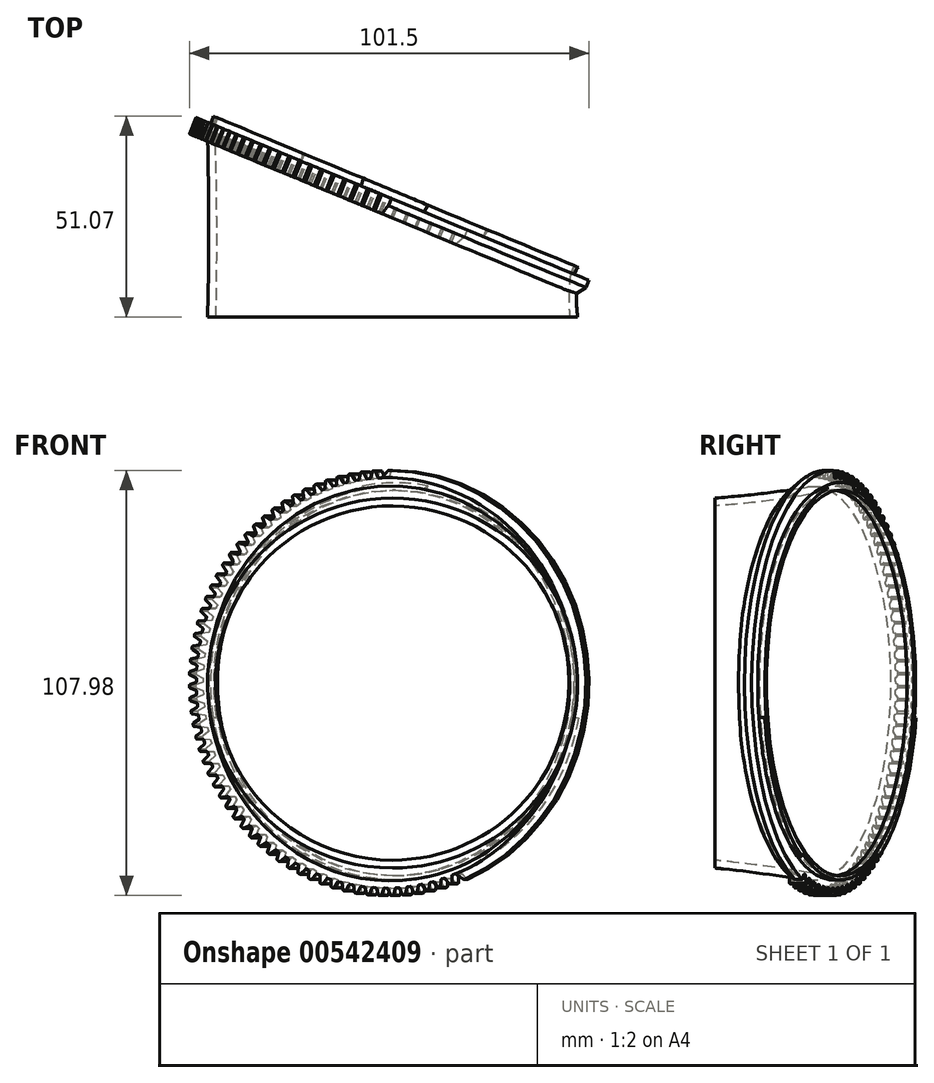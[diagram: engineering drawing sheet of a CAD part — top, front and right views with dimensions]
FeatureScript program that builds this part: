
annotation { "Feature Type Name" : "Feature", "Feature Type Description" : "" }
export const myFeature = defineFeature(function(context is Context, id is Id, definition is map)
    precondition{}
    {
        {
            var Q0;
            Q0=qCreatedBy(makeId("Front.planeOp"),FACE);
            var sketch = newSketch(context, id + "F0", { "sketchPlane" : qUnion([Q0])});
            skCircle(sketch, "E0", {"center": v(0, 0) * mm, "radius": 47 * mm});
            skSolve(sketch);
        }
        {
            var Q0;
            Q0=qCreatedBy(makeId("Top.planeOp"),FACE);
            var sketch = newSketch(context, id + "F1", { "sketchPlane" : qUnion([Q0])});
            skLineSegment(sketch, "E1", {"start": v(23.1, 20.43) * mm, "end": v(-23.1, 39.57) * mm});
            skLineSegment(sketch, "E2", {"start": v(25, 0) * mm, "end": v(-25, 0) * mm});
            skLineSegment(sketch, "E3", {"start": v(0, 30) * mm, "end": v(0, 0) * mm});
            skPoint(sketch, "E4", {"position": v(0, 30) * mm});
            skSolve(sketch);
        }
        {
            var Q0;
            Q0=sQuery(id+"F1.wireOp",EDGE,"E1");
            cPlane(context, id + "F2", {"entities" : qUnion([Q0]), "cplaneType" : CPlaneType.LINE_ANGLE, "offset" : 25 * mm, "angle" : 0 * degree, "width" : 150 * mm, "height" : 150 * mm});
        }
        {
            var Q0;
            Q0=qCreatedBy(id+"F2.planeOp",FACE);
            var sketch = newSketch(context, id + "F3", { "sketchPlane" : qUnion([Q0])});
            skCircle(sketch, "E5", {"center": v(-11.48, 0) * mm, "radius": 51 * mm});
            skSolve(sketch);
        }
        {
            var Q0;
            Q0=makeQuery(id+"F0.imprint","IMPRINT",FACE,{"disambiguationData":[TD([[makeQuery(id+"F0.imprint","IMPRINT",EDGE,{"derivedFrom":sQuery(id+"F0.wireOp",EDGE,"E0")}),1.0]])]});
            var Q1;
            Q1=makeQuery(id+"F3.imprint","IMPRINT",FACE,{"disambiguationData":[TD([[makeQuery(id+"F3.imprint","IMPRINT",EDGE,{"derivedFrom":sQuery(id+"F3.wireOp",EDGE,"E5")}),1.0]])]});
            loft(context, id + "F4", {"sheetProfilesArray" : [{ "sheetProfileEntities" : qUnion([Q0]) }, { "sheetProfileEntities" : qUnion([Q1]) }]});
        }
        {
            var Q0;
            Q0=makeQuery(id+"F4.opLoft","CAP_FACE",FACE,{"disambiguationData":[OSD([makeQuery(id+"F3.imprint","IMPRINT",FACE,{"disambiguationData":[TD([[makeQuery(id+"F3.imprint","IMPRINT",EDGE,{"derivedFrom":sQuery(id+"F3.wireOp",EDGE,"E5")}),1.0]])]})])],"isStart":true});
            var sketch = newSketch(context, id + "F5", { "sketchPlane" : qUnion([Q0])});
            skCircle(sketch, "E6", {"center": v(11.48, 0) * mm, "radius": 49 * mm});
            skSolve(sketch);
        }
        {
            var Q0;
            Q0=makeQuery(id+"F4.opLoft","CAP_FACE",FACE,{"disambiguationData":[OSD([makeQuery(id+"F0.imprint","IMPRINT",FACE,{"disambiguationData":[TD([[makeQuery(id+"F0.imprint","IMPRINT",EDGE,{"derivedFrom":sQuery(id+"F0.wireOp",EDGE,"E0")}),1.0]])]})])],"isStart":true});
            var sketch = newSketch(context, id + "F6", { "sketchPlane" : qUnion([Q0])});
            skCircle(sketch, "E7", {"center": v(0, 0) * mm, "radius": 45 * mm});
            skSolve(sketch);
        }
        {
            var Q0;
            Q0=makeQuery(id+"F4.opLoft","CAP_FACE",FACE,{"disambiguationData":[OSD([makeQuery(id+"F3.imprint","IMPRINT",FACE,{"disambiguationData":[TD([[makeQuery(id+"F3.imprint","IMPRINT",EDGE,{"derivedFrom":sQuery(id+"F3.wireOp",EDGE,"E5")}),1.0]])]})])],"isStart":true});
            var sketch = newSketch(context, id + "F7", { "sketchPlane" : qUnion([Q0])});
            skCircle(sketch, "E8", {"center": v(11.48, 0) * mm, "radius": 54 * mm});
            skCircle(sketch, "E9", {"center": v(11.48, 0) * mm, "radius": 50.9 * mm});
            skSolve(sketch);
        }
        {
            var Q0;
            Q0=makeQuery(id+"F7.imprint","IMPRINT",FACE,{"disambiguationData":[TD([[makeQuery(id+"F7.imprint","IMPRINT",EDGE,{"derivedFrom":sQuery(id+"F7.wireOp",EDGE,"E8")}),1.0]])]});
            var Q1;
            Q1=makeQuery(id+"F7.imprint","IMPRINT",FACE,{"disambiguationData":[TD([[makeQuery(id+"F7.imprint","IMPRINT",EDGE,{"derivedFrom":sQuery(id+"F7.wireOp",EDGE,"E9")}),-1.0]])]});
            var Q2;
            Q2=makeQuery(id+"F7.imprint","IMPRINT",FACE,{"disambiguationData":[TD([[makeQuery(id+"F7.imprint","IMPRINT",EDGE,{"derivedFrom":sQuery(id+"F7.wireOp",EDGE,"E9")}),1.0]])]});
            extrude(context, id + "F8", {"entities" : qUnion([Q0, Q1, Q2]), "operationType" : NewBodyOperationType.ADD, "oppositeDirection" : true, "depth" : 4.5 * mm, "offsetDistance" : 25 * mm});
        }
        {
            var Q0;
            Q0=makeQuery(id+"F8.boolean.opBoolean","MERGE",FACE,{"derivedFrom":[makeQuery(id+"F4.opLoft","CAP_FACE",FACE,{"disambiguationData":[OSD([makeQuery(id+"F3.imprint","IMPRINT",FACE,{"disambiguationData":[TD([[makeQuery(id+"F3.imprint","IMPRINT",EDGE,{"derivedFrom":sQuery(id+"F3.wireOp",EDGE,"E5")}),1.0]])]})])],"isStart":true}),makeQuery(id+"F8.opExtrude","CAP_FACE",FACE,{"disambiguationData":[OSD([sQuery(id+"F7.wireOp",EDGE,"E8"),sQuery(id+"F7.wireOp",EDGE,"E9")])],"isStart":true})]});
            var sketch = newSketch(context, id + "F9", { "sketchPlane" : qUnion([Q0])});
            skCircle(sketch, "E10", {"center": v(11.48, 0) * mm, "radius": 51 * mm});
            skCircle(sketch, "E11", {"center": v(11.48, 0) * mm, "radius": 49 * mm});
            skSolve(sketch);
        }
        {
            var Q1;
            Q1=makeQuery(id+"F6.imprint","IMPRINT",FACE,{"disambiguationData":[TD([[makeQuery(id+"F6.imprint","IMPRINT",EDGE,{"derivedFrom":sQuery(id+"F6.wireOp",EDGE,"E7")}),1.0]])]});
            var Q2;
            Q2=makeQuery(id+"F5.imprint","IMPRINT",FACE,{"disambiguationData":[TD([[makeQuery(id+"F5.imprint","IMPRINT",EDGE,{"derivedFrom":sQuery(id+"F5.wireOp",EDGE,"E6")}),1.0]])]});
            loft(context, id + "F10", {"operationType" : NewBodyOperationType.REMOVE, "sheetProfilesArray" : [{ "sheetProfileEntities" : qUnion([Q1]) }, { "sheetProfileEntities" : qUnion([Q2]) }]});
        }
        {
            var Q0;
            Q0=makeQuery(id+"F9.imprint","IMPRINT",FACE,{"disambiguationData":[TD([[makeQuery(id+"F9.imprint","IMPRINT",EDGE,{"derivedFrom":sQuery(id+"F9.wireOp",EDGE,"E10")}),1.0]])]});
            extrude(context, id + "F11", {"entities" : qUnion([Q0]), "operationType" : NewBodyOperationType.ADD, "depth" : 2 * mm, "offsetDistance" : 25 * mm});
        }
        {
            var Q0;
            Q0=makeQuery(id+"F11.opExtrude","CAP_EDGE",EDGE,{"disambiguationData":[OSD([sQuery(id+"F9.wireOp",EDGE,"E10")])],"isStart":false});
            chamfer(context, id + "F12", {"entities" : qUnion([Q0]), "chamferType" : ChamferType.OFFSET_ANGLE, "width" : 2 * mm, "oppositeDirection" : true, "angle" : 5 * degree, "tangentPropagation" : true});
        }
        {
            var Q0;
            Q0=makeQuery(id+"F8.boolean.opBoolean","MERGE",FACE,{"derivedFrom":[makeQuery(id+"F4.opLoft","CAP_FACE",FACE,{"disambiguationData":[OSD([makeQuery(id+"F3.imprint","IMPRINT",FACE,{"disambiguationData":[TD([[makeQuery(id+"F3.imprint","IMPRINT",EDGE,{"derivedFrom":sQuery(id+"F3.wireOp",EDGE,"E5")}),1.0]])]})])],"isStart":true}),makeQuery(id+"F8.opExtrude","CAP_FACE",FACE,{"disambiguationData":[OSD([sQuery(id+"F7.wireOp",EDGE,"E8"),sQuery(id+"F7.wireOp",EDGE,"E9")])],"isStart":true})]});
            var sketch = newSketch(context, id + "F13", { "sketchPlane" : qUnion([Q0])});
            skLineSegment(sketch, "E12", {"start": v(11.48, 0) * mm, "end": v(11.48, 54) * mm});
            skLineSegment(sketch, "E13", {"start": v(11.48, 0) * mm, "end": v(14.8, 53.9) * mm});
            skLineSegment(sketch, "E14", {"start": v(11.48, 54) * mm, "end": v(11.74, 54) * mm});
            skLineSegment(sketch, "E15", {"start": v(14.8, 53.9) * mm, "end": v(14.54, 53.91) * mm});
            skLineSegment(sketch, "E16", {"start": v(12.7, 52.09) * mm, "end": v(13.47, 52.07) * mm});
            skLineSegment(sketch, "E17", {"start": v(11.93, 53.87) * mm, "end": v(12.5, 52.22) * mm});
            skLineSegment(sketch, "E18", {"start": v(13.66, 52.2) * mm, "end": v(14.34, 53.8) * mm});
            skPoint(sketch, "E19.visualSharp", {"position": v(11.88, 54) * mm});
            skArc(sketch, "E19.filletArc", {"start": v(11.93, 53.87) * mm, "mid": v(11.85, 53.96) * mm, "end": v(11.74, 54) * mm});
            skPoint(sketch, "E20.visualSharp", {"position": v(12.56, 52.09) * mm});
            skArc(sketch, "E20.filletArc", {"start": v(12.5, 52.22) * mm, "mid": v(12.58, 52.12) * mm, "end": v(12.7, 52.09) * mm});
            skPoint(sketch, "E21.visualSharp", {"position": v(13.6, 52.07) * mm});
            skArc(sketch, "E21.filletArc", {"start": v(13.47, 52.07) * mm, "mid": v(13.58, 52.1) * mm, "end": v(13.66, 52.2) * mm});
            skPoint(sketch, "E22.visualSharp", {"position": v(14.4, 53.92) * mm});
            skArc(sketch, "E22.filletArc", {"start": v(14.54, 53.91) * mm, "mid": v(14.42, 53.88) * mm, "end": v(14.34, 53.8) * mm});
            skLineSegment(sketch, "E23", {"start": v(11.74, 54) * mm, "end": v(14.54, 53.91) * mm});
            skLineSegment(sketch, "E24.1.0", {"start": v(11.5, 54) * mm, "end": v(11.25, 54) * mm});
            skPoint(sketch, "E24.1.1", {"position": v(9.38, 52.06) * mm});
            skLineSegment(sketch, "E24.1.2", {"start": v(8.64, 53.8) * mm, "end": v(9.32, 52.19) * mm});
            skPoint(sketch, "E24.1.3", {"position": v(10.43, 52.1) * mm});
            skPoint(sketch, "E24.1.4", {"position": v(8.59, 53.92) * mm});
            skLineSegment(sketch, "E24.1.5", {"start": v(8.19, 53.9) * mm, "end": v(8.45, 53.92) * mm});
            skLineSegment(sketch, "E24.1.6", {"start": v(9.52, 52.06) * mm, "end": v(10.3, 52.1) * mm});
            skPoint(sketch, "E24.1.7", {"position": v(11.1, 54) * mm});
            skLineSegment(sketch, "E24.1.8", {"start": v(8.45, 53.92) * mm, "end": v(11.25, 54) * mm});
            skLineSegment(sketch, "E24.1.9", {"start": v(10.47, 52.23) * mm, "end": v(11.06, 53.87) * mm});
            skArc(sketch, "E24.1.10", {"start": v(9.32, 52.19) * mm, "mid": v(9.4, 52.1) * mm, "end": v(9.52, 52.06) * mm});
            skArc(sketch, "E24.1.11", {"start": v(10.3, 52.1) * mm, "mid": v(10.4, 52.13) * mm, "end": v(10.47, 52.23) * mm});
            skArc(sketch, "E24.1.12", {"start": v(11.25, 54) * mm, "mid": v(11.13, 53.96) * mm, "end": v(11.06, 53.87) * mm});
            skArc(sketch, "E24.1.13", {"start": v(8.64, 53.8) * mm, "mid": v(8.56, 53.89) * mm, "end": v(8.45, 53.92) * mm});
            skLineSegment(sketch, "E24.2.0", {"start": v(8.21, 53.9) * mm, "end": v(7.95, 53.89) * mm});
            skPoint(sketch, "E24.2.1", {"position": v(6.2, 51.83) * mm});
            skLineSegment(sketch, "E24.2.2", {"start": v(5.37, 53.52) * mm, "end": v(6.15, 51.96) * mm});
            skPoint(sketch, "E24.2.3", {"position": v(7.25, 51.94) * mm});
            skPoint(sketch, "E24.2.4", {"position": v(5.3, 53.65) * mm});
            skLineSegment(sketch, "E24.2.5", {"start": v(4.9, 53.6) * mm, "end": v(5.17, 53.63) * mm});
            skLineSegment(sketch, "E24.2.6", {"start": v(6.35, 51.85) * mm, "end": v(7.12, 51.93) * mm});
            skPoint(sketch, "E24.2.7", {"position": v(7.81, 53.88) * mm});
            skLineSegment(sketch, "E24.2.8", {"start": v(5.17, 53.63) * mm, "end": v(7.95, 53.89) * mm});
            skLineSegment(sketch, "E24.2.9", {"start": v(7.3, 52.07) * mm, "end": v(7.77, 53.74) * mm});
            skArc(sketch, "E24.2.10", {"start": v(6.15, 51.96) * mm, "mid": v(6.23, 51.87) * mm, "end": v(6.35, 51.85) * mm});
            skArc(sketch, "E24.2.11", {"start": v(7.12, 51.93) * mm, "mid": v(7.23, 51.97) * mm, "end": v(7.3, 52.07) * mm});
            skArc(sketch, "E24.2.12", {"start": v(7.95, 53.89) * mm, "mid": v(7.84, 53.84) * mm, "end": v(7.77, 53.74) * mm});
            skArc(sketch, "E24.2.13", {"start": v(5.37, 53.52) * mm, "mid": v(5.28, 53.6) * mm, "end": v(5.17, 53.63) * mm});
            skLineSegment(sketch, "E24.3.0", {"start": v(4.93, 53.6) * mm, "end": v(4.68, 53.57) * mm});
            skPoint(sketch, "E24.3.1", {"position": v(3.06, 51.41) * mm});
            skLineSegment(sketch, "E24.3.2", {"start": v(2.12, 53.05) * mm, "end": v(2.99, 51.53) * mm});
            skPoint(sketch, "E24.3.3", {"position": v(4.1, 51.58) * mm});
            skPoint(sketch, "E24.3.4", {"position": v(2.05, 53.17) * mm});
            skLineSegment(sketch, "E24.3.5", {"start": v(1.65, 53.1) * mm, "end": v(1.9, 53.15) * mm});
            skLineSegment(sketch, "E24.3.6", {"start": v(3.2, 51.44) * mm, "end": v(3.96, 51.56) * mm});
            skPoint(sketch, "E24.3.7", {"position": v(4.53, 53.55) * mm});
            skLineSegment(sketch, "E24.3.8", {"start": v(1.9, 53.15) * mm, "end": v(4.68, 53.57) * mm});
            skLineSegment(sketch, "E24.3.9", {"start": v(4.12, 51.72) * mm, "end": v(4.5, 53.42) * mm});
            skArc(sketch, "E24.3.10", {"start": v(2.99, 51.53) * mm, "mid": v(3.08, 51.45) * mm, "end": v(3.2, 51.44) * mm});
            skArc(sketch, "E24.3.11", {"start": v(3.96, 51.56) * mm, "mid": v(4.07, 51.61) * mm, "end": v(4.12, 51.72) * mm});
            skArc(sketch, "E24.3.12", {"start": v(4.68, 53.57) * mm, "mid": v(4.56, 53.52) * mm, "end": v(4.5, 53.42) * mm});
            skArc(sketch, "E24.3.13", {"start": v(2.12, 53.05) * mm, "mid": v(2.03, 53.13) * mm, "end": v(1.9, 53.15) * mm});
            skLineSegment(sketch, "E24.4.0", {"start": v(1.68, 53.1) * mm, "end": v(1.42, 53.06) * mm});
            skPoint(sketch, "E24.4.1", {"position": v(-0.06, 50.8) * mm});
            skLineSegment(sketch, "E24.4.2", {"start": v(-1.1, 52.38) * mm, "end": v(-0.14, 50.92) * mm});
            skPoint(sketch, "E24.4.3", {"position": v(0.96, 51.04) * mm});
            skPoint(sketch, "E24.4.4", {"position": v(-1.18, 52.5) * mm});
            skLineSegment(sketch, "E24.4.5", {"start": v(-1.57, 52.4) * mm, "end": v(-1.31, 52.46) * mm});
            skLineSegment(sketch, "E24.4.6", {"start": v(0.07, 50.84) * mm, "end": v(0.83, 51) * mm});
            skPoint(sketch, "E24.4.7", {"position": v(1.28, 53.03) * mm});
            skLineSegment(sketch, "E24.4.8", {"start": v(-1.31, 52.46) * mm, "end": v(1.42, 53.06) * mm});
            skLineSegment(sketch, "E24.4.9", {"start": v(0.99, 51.17) * mm, "end": v(1.26, 52.9) * mm});
            skArc(sketch, "E24.4.10", {"start": v(-0.14, 50.92) * mm, "mid": v(-0.04, 50.85) * mm, "end": v(0.07, 50.84) * mm});
            skArc(sketch, "E24.4.11", {"start": v(0.83, 51) * mm, "mid": v(0.93, 51.07) * mm, "end": v(0.99, 51.17) * mm});
            skArc(sketch, "E24.4.12", {"start": v(1.42, 53.06) * mm, "mid": v(1.32, 53) * mm, "end": v(1.26, 52.9) * mm});
            skArc(sketch, "E24.4.13", {"start": v(-1.1, 52.38) * mm, "mid": v(-1.2, 52.46) * mm, "end": v(-1.31, 52.46) * mm});
            skLineSegment(sketch, "E24.5.0", {"start": v(-1.54, 52.4) * mm, "end": v(-1.8, 52.34) * mm});
            skPoint(sketch, "E24.5.1", {"position": v(-3.14, 50) * mm});
            skLineSegment(sketch, "E24.5.2", {"start": v(-4.27, 51.51) * mm, "end": v(-3.22, 50.12) * mm});
            skPoint(sketch, "E24.5.3", {"position": v(-2.13, 50.3) * mm});
            skPoint(sketch, "E24.5.4", {"position": v(-4.35, 51.63) * mm});
            skLineSegment(sketch, "E24.5.5", {"start": v(-4.74, 51.5) * mm, "end": v(-4.49, 51.59) * mm});
            skLineSegment(sketch, "E24.5.6", {"start": v(-3, 50.05) * mm, "end": v(-2.26, 50.26) * mm});
            skPoint(sketch, "E24.5.7", {"position": v(-1.93, 52.3) * mm});
            skLineSegment(sketch, "E24.5.8", {"start": v(-4.49, 51.59) * mm, "end": v(-1.8, 52.34) * mm});
            skLineSegment(sketch, "E24.5.9", {"start": v(-2.11, 50.44) * mm, "end": v(-1.94, 52.17) * mm});
            skArc(sketch, "E24.5.10", {"start": v(-3.22, 50.12) * mm, "mid": v(-3.12, 50.05) * mm, "end": v(-3, 50.05) * mm});
            skArc(sketch, "E24.5.11", {"start": v(-2.26, 50.26) * mm, "mid": v(-2.16, 50.33) * mm, "end": v(-2.11, 50.44) * mm});
            skArc(sketch, "E24.5.12", {"start": v(-1.8, 52.34) * mm, "mid": v(-1.9, 52.28) * mm, "end": v(-1.94, 52.17) * mm});
            skArc(sketch, "E24.5.13", {"start": v(-4.27, 51.51) * mm, "mid": v(-4.37, 51.58) * mm, "end": v(-4.49, 51.59) * mm});
            skLineSegment(sketch, "E24.6.0", {"start": v(-4.71, 51.51) * mm, "end": v(-4.96, 51.44) * mm});
            skPoint(sketch, "E24.6.1", {"position": v(-6.16, 49.02) * mm});
            skLineSegment(sketch, "E24.6.2", {"start": v(-7.38, 50.46) * mm, "end": v(-6.25, 49.13) * mm});
            skPoint(sketch, "E24.6.3", {"position": v(-5.17, 49.38) * mm});
            skPoint(sketch, "E24.6.4", {"position": v(-7.47, 50.57) * mm});
            skLineSegment(sketch, "E24.6.5", {"start": v(-7.85, 50.42) * mm, "end": v(-7.6, 50.52) * mm});
            skLineSegment(sketch, "E24.6.6", {"start": v(-6.03, 49.07) * mm, "end": v(-5.3, 49.33) * mm});
            skPoint(sketch, "E24.6.7", {"position": v(-5.1, 51.4) * mm});
            skLineSegment(sketch, "E24.6.8", {"start": v(-7.6, 50.52) * mm, "end": v(-4.96, 51.44) * mm});
            skLineSegment(sketch, "E24.6.9", {"start": v(-5.16, 49.51) * mm, "end": v(-5.1, 51.25) * mm});
            skArc(sketch, "E24.6.10", {"start": v(-6.25, 49.13) * mm, "mid": v(-6.15, 49.07) * mm, "end": v(-6.03, 49.07) * mm});
            skArc(sketch, "E24.6.11", {"start": v(-5.3, 49.33) * mm, "mid": v(-5.2, 49.4) * mm, "end": v(-5.16, 49.51) * mm});
            skArc(sketch, "E24.6.12", {"start": v(-4.96, 51.44) * mm, "mid": v(-5.06, 51.37) * mm, "end": v(-5.1, 51.25) * mm});
            skArc(sketch, "E24.6.13", {"start": v(-7.38, 50.46) * mm, "mid": v(-7.48, 50.52) * mm, "end": v(-7.6, 50.52) * mm});
            skLineSegment(sketch, "E24.7.0", {"start": v(-7.82, 50.43) * mm, "end": v(-8.07, 50.34) * mm});
            skPoint(sketch, "E24.7.1", {"position": v(-9.11, 47.86) * mm});
            skLineSegment(sketch, "E24.7.2", {"start": v(-10.42, 49.21) * mm, "end": v(-9.2, 47.96) * mm});
            skPoint(sketch, "E24.7.3", {"position": v(-8.15, 48.27) * mm});
            skPoint(sketch, "E24.7.4", {"position": v(-10.52, 49.32) * mm});
            skLineSegment(sketch, "E24.7.5", {"start": v(-10.88, 49.15) * mm, "end": v(-10.65, 49.26) * mm});
            skLineSegment(sketch, "E24.7.6", {"start": v(-8.99, 47.91) * mm, "end": v(-8.27, 48.22) * mm});
            skPoint(sketch, "E24.7.7", {"position": v(-8.2, 50.29) * mm});
            skLineSegment(sketch, "E24.7.8", {"start": v(-10.65, 49.26) * mm, "end": v(-8.07, 50.34) * mm});
            skLineSegment(sketch, "E24.7.9", {"start": v(-8.15, 48.4) * mm, "end": v(-8.2, 50.15) * mm});
            skArc(sketch, "E24.7.10", {"start": v(-9.2, 47.96) * mm, "mid": v(-9.1, 47.9) * mm, "end": v(-8.99, 47.91) * mm});
            skArc(sketch, "E24.7.11", {"start": v(-8.27, 48.22) * mm, "mid": v(-8.18, 48.3) * mm, "end": v(-8.15, 48.4) * mm});
            skArc(sketch, "E24.7.12", {"start": v(-8.07, 50.34) * mm, "mid": v(-8.16, 50.26) * mm, "end": v(-8.2, 50.15) * mm});
            skArc(sketch, "E24.7.13", {"start": v(-10.42, 49.21) * mm, "mid": v(-10.53, 49.27) * mm, "end": v(-10.65, 49.26) * mm});
            skLineSegment(sketch, "E24.8.0", {"start": v(-10.86, 49.16) * mm, "end": v(-11.1, 49.05) * mm});
            skPoint(sketch, "E24.8.1", {"position": v(-12, 46.51) * mm});
            skLineSegment(sketch, "E24.8.2", {"start": v(-13.38, 47.79) * mm, "end": v(-12.1, 46.6) * mm});
            skPoint(sketch, "E24.8.3", {"position": v(-11.05, 46.99) * mm});
            skPoint(sketch, "E24.8.4", {"position": v(-13.49, 47.88) * mm});
            skLineSegment(sketch, "E24.8.5", {"start": v(-13.84, 47.7) * mm, "end": v(-13.61, 47.82) * mm});
            skLineSegment(sketch, "E24.8.6", {"start": v(-11.87, 46.57) * mm, "end": v(-11.18, 46.93) * mm});
            skPoint(sketch, "E24.8.7", {"position": v(-11.23, 49) * mm});
            skLineSegment(sketch, "E24.8.8", {"start": v(-13.61, 47.82) * mm, "end": v(-11.1, 49.05) * mm});
            skLineSegment(sketch, "E24.8.9", {"start": v(-11.07, 47.12) * mm, "end": v(-11.21, 48.85) * mm});
            skArc(sketch, "E24.8.10", {"start": v(-12.1, 46.6) * mm, "mid": v(-11.99, 46.56) * mm, "end": v(-11.87, 46.57) * mm});
            skArc(sketch, "E24.8.11", {"start": v(-11.18, 46.93) * mm, "mid": v(-11.1, 47) * mm, "end": v(-11.07, 47.12) * mm});
            skArc(sketch, "E24.8.12", {"start": v(-11.1, 49.05) * mm, "mid": v(-11.19, 48.97) * mm, "end": v(-11.21, 48.85) * mm});
            skArc(sketch, "E24.8.13", {"start": v(-13.38, 47.79) * mm, "mid": v(-13.5, 47.84) * mm, "end": v(-13.61, 47.82) * mm});
            skLineSegment(sketch, "E24.9.0", {"start": v(-13.82, 47.7) * mm, "end": v(-14.05, 47.59) * mm});
            skPoint(sketch, "E24.9.1", {"position": v(-14.79, 45) * mm});
            skLineSegment(sketch, "E24.9.2", {"start": v(-16.25, 46.18) * mm, "end": v(-14.9, 45.08) * mm});
            skPoint(sketch, "E24.9.3", {"position": v(-13.88, 45.52) * mm});
            skPoint(sketch, "E24.9.4", {"position": v(-16.36, 46.27) * mm});
            skLineSegment(sketch, "E24.9.5", {"start": v(-16.7, 46.06) * mm, "end": v(-16.48, 46.2) * mm});
            skLineSegment(sketch, "E24.9.6", {"start": v(-14.67, 45.06) * mm, "end": v(-14, 45.46) * mm});
            skPoint(sketch, "E24.9.7", {"position": v(-14.17, 47.52) * mm});
            skLineSegment(sketch, "E24.9.8", {"start": v(-16.48, 46.2) * mm, "end": v(-14.05, 47.59) * mm});
            skLineSegment(sketch, "E24.9.9", {"start": v(-13.9, 45.66) * mm, "end": v(-14.15, 47.38) * mm});
            skArc(sketch, "E24.9.10", {"start": v(-14.9, 45.08) * mm, "mid": v(-14.78, 45.04) * mm, "end": v(-14.67, 45.06) * mm});
            skArc(sketch, "E24.9.11", {"start": v(-14, 45.46) * mm, "mid": v(-13.91, 45.54) * mm, "end": v(-13.9, 45.66) * mm});
            skArc(sketch, "E24.9.12", {"start": v(-14.05, 47.59) * mm, "mid": v(-14.13, 47.5) * mm, "end": v(-14.15, 47.38) * mm});
            skArc(sketch, "E24.9.13", {"start": v(-16.25, 46.18) * mm, "mid": v(-16.36, 46.23) * mm, "end": v(-16.48, 46.2) * mm});
            skLineSegment(sketch, "E24.10.0", {"start": v(-16.68, 46.08) * mm, "end": v(-16.9, 45.94) * mm});
            skPoint(sketch, "E24.10.1", {"position": v(-17.48, 43.3) * mm});
            skLineSegment(sketch, "E24.10.2", {"start": v(-19.01, 44.4) * mm, "end": v(-17.6, 43.4) * mm});
            skPoint(sketch, "E24.10.3", {"position": v(-16.6, 43.9) * mm});
            skPoint(sketch, "E24.10.4", {"position": v(-19.13, 44.49) * mm});
            skLineSegment(sketch, "E24.10.5", {"start": v(-19.46, 44.26) * mm, "end": v(-19.24, 44.4) * mm});
            skLineSegment(sketch, "E24.10.6", {"start": v(-17.36, 43.39) * mm, "end": v(-16.72, 43.82) * mm});
            skPoint(sketch, "E24.10.7", {"position": v(-17.02, 45.87) * mm});
            skLineSegment(sketch, "E24.10.8", {"start": v(-19.24, 44.4) * mm, "end": v(-16.9, 45.94) * mm});
            skLineSegment(sketch, "E24.10.9", {"start": v(-16.63, 44.03) * mm, "end": v(-17, 45.73) * mm});
            skArc(sketch, "E24.10.10", {"start": v(-17.6, 43.4) * mm, "mid": v(-17.48, 43.35) * mm, "end": v(-17.36, 43.39) * mm});
            skArc(sketch, "E24.10.11", {"start": v(-16.72, 43.82) * mm, "mid": v(-16.64, 43.9) * mm, "end": v(-16.63, 44.03) * mm});
            skArc(sketch, "E24.10.12", {"start": v(-16.9, 45.94) * mm, "mid": v(-16.98, 45.85) * mm, "end": v(-17, 45.73) * mm});
            skArc(sketch, "E24.10.13", {"start": v(-19.01, 44.4) * mm, "mid": v(-19.13, 44.44) * mm, "end": v(-19.24, 44.4) * mm});
            skLineSegment(sketch, "E24.11.0", {"start": v(-19.44, 44.27) * mm, "end": v(-19.65, 44.13) * mm});
            skPoint(sketch, "E24.11.1", {"position": v(-20.07, 41.46) * mm});
            skLineSegment(sketch, "E24.11.2", {"start": v(-21.66, 42.47) * mm, "end": v(-20.18, 41.54) * mm});
            skPoint(sketch, "E24.11.3", {"position": v(-19.23, 42.1) * mm});
            skPoint(sketch, "E24.11.4", {"position": v(-21.78, 42.54) * mm});
            skLineSegment(sketch, "E24.11.5", {"start": v(-22.1, 42.3) * mm, "end": v(-21.9, 42.45) * mm});
            skLineSegment(sketch, "E24.11.6", {"start": v(-19.96, 41.55) * mm, "end": v(-19.34, 42.02) * mm});
            skPoint(sketch, "E24.11.7", {"position": v(-19.76, 44.04) * mm});
            skLineSegment(sketch, "E24.11.8", {"start": v(-21.9, 42.45) * mm, "end": v(-19.65, 44.13) * mm});
            skLineSegment(sketch, "E24.11.9", {"start": v(-19.27, 42.23) * mm, "end": v(-19.73, 43.9) * mm});
            skArc(sketch, "E24.11.10", {"start": v(-20.18, 41.54) * mm, "mid": v(-20.07, 41.5) * mm, "end": v(-19.96, 41.55) * mm});
            skArc(sketch, "E24.11.11", {"start": v(-19.34, 42.02) * mm, "mid": v(-19.27, 42.11) * mm, "end": v(-19.27, 42.23) * mm});
            skArc(sketch, "E24.11.12", {"start": v(-19.65, 44.13) * mm, "mid": v(-19.72, 44.03) * mm, "end": v(-19.73, 43.9) * mm});
            skArc(sketch, "E24.11.13", {"start": v(-21.66, 42.47) * mm, "mid": v(-21.78, 42.5) * mm, "end": v(-21.9, 42.45) * mm});
            skLineSegment(sketch, "E24.12.0", {"start": v(-22.08, 42.3) * mm, "end": v(-22.28, 42.15) * mm});
            skPoint(sketch, "E24.12.1", {"position": v(-22.53, 39.46) * mm});
            skLineSegment(sketch, "E24.12.2", {"start": v(-24.19, 40.37) * mm, "end": v(-22.66, 39.53) * mm});
            skPoint(sketch, "E24.12.3", {"position": v(-21.74, 40.15) * mm});
            skPoint(sketch, "E24.12.4", {"position": v(-24.31, 40.43) * mm});
            skLineSegment(sketch, "E24.12.5", {"start": v(-24.61, 40.17) * mm, "end": v(-24.42, 40.34) * mm});
            skLineSegment(sketch, "E24.12.6", {"start": v(-22.43, 39.55) * mm, "end": v(-21.84, 40.06) * mm});
            skPoint(sketch, "E24.12.7", {"position": v(-22.4, 42.06) * mm});
            skLineSegment(sketch, "E24.12.8", {"start": v(-24.42, 40.34) * mm, "end": v(-22.28, 42.15) * mm});
            skLineSegment(sketch, "E24.12.9", {"start": v(-21.78, 40.28) * mm, "end": v(-22.35, 41.92) * mm});
            skArc(sketch, "E24.12.10", {"start": v(-22.66, 39.53) * mm, "mid": v(-22.54, 39.5) * mm, "end": v(-22.43, 39.55) * mm});
            skArc(sketch, "E24.12.11", {"start": v(-21.84, 40.06) * mm, "mid": v(-21.78, 40.16) * mm, "end": v(-21.78, 40.28) * mm});
            skArc(sketch, "E24.12.12", {"start": v(-22.28, 42.15) * mm, "mid": v(-22.35, 42.05) * mm, "end": v(-22.35, 41.92) * mm});
            skArc(sketch, "E24.12.13", {"start": v(-24.19, 40.37) * mm, "mid": v(-24.3, 40.39) * mm, "end": v(-24.42, 40.34) * mm});
            skLineSegment(sketch, "E24.13.0", {"start": v(-24.6, 40.18) * mm, "end": v(-24.79, 40) * mm});
            skPoint(sketch, "E24.13.1", {"position": v(-24.88, 37.32) * mm});
            skLineSegment(sketch, "E24.13.2", {"start": v(-26.58, 38.12) * mm, "end": v(-25, 37.38) * mm});
            skPoint(sketch, "E24.13.3", {"position": v(-24.12, 38.05) * mm});
            skPoint(sketch, "E24.13.4", {"position": v(-26.71, 38.18) * mm});
            skLineSegment(sketch, "E24.13.5", {"start": v(-27, 37.9) * mm, "end": v(-26.81, 38.08) * mm});
            skLineSegment(sketch, "E24.13.6", {"start": v(-24.78, 37.41) * mm, "end": v(-24.22, 37.96) * mm});
            skPoint(sketch, "E24.13.7", {"position": v(-24.9, 39.91) * mm});
            skLineSegment(sketch, "E24.13.8", {"start": v(-26.81, 38.08) * mm, "end": v(-24.79, 40) * mm});
            skLineSegment(sketch, "E24.13.9", {"start": v(-24.18, 38.17) * mm, "end": v(-24.84, 39.78) * mm});
            skArc(sketch, "E24.13.10", {"start": v(-25, 37.38) * mm, "mid": v(-24.88, 37.36) * mm, "end": v(-24.78, 37.41) * mm});
            skArc(sketch, "E24.13.11", {"start": v(-24.22, 37.96) * mm, "mid": v(-24.17, 38.06) * mm, "end": v(-24.18, 38.17) * mm});
            skArc(sketch, "E24.13.12", {"start": v(-24.79, 40) * mm, "mid": v(-24.85, 39.9) * mm, "end": v(-24.84, 39.78) * mm});
            skArc(sketch, "E24.13.13", {"start": v(-26.58, 38.12) * mm, "mid": v(-26.7, 38.13) * mm, "end": v(-26.81, 38.08) * mm});
            skLineSegment(sketch, "E24.14.0", {"start": v(-26.98, 37.9) * mm, "end": v(-27.16, 37.72) * mm});
            skPoint(sketch, "E24.14.1", {"position": v(-27.08, 35.03) * mm});
            skLineSegment(sketch, "E24.14.2", {"start": v(-28.84, 35.72) * mm, "end": v(-27.21, 35.08) * mm});
            skPoint(sketch, "E24.14.3", {"position": v(-26.38, 35.8) * mm});
            skPoint(sketch, "E24.14.4", {"position": v(-28.97, 35.78) * mm});
            skLineSegment(sketch, "E24.14.5", {"start": v(-29.23, 35.48) * mm, "end": v(-29.06, 35.67) * mm});
            skLineSegment(sketch, "E24.14.6", {"start": v(-27, 35.13) * mm, "end": v(-26.47, 35.7) * mm});
            skPoint(sketch, "E24.14.7", {"position": v(-27.26, 37.62) * mm});
            skLineSegment(sketch, "E24.14.8", {"start": v(-29.06, 35.67) * mm, "end": v(-27.16, 37.72) * mm});
            skLineSegment(sketch, "E24.14.9", {"start": v(-26.44, 35.93) * mm, "end": v(-27.2, 37.5) * mm});
            skArc(sketch, "E24.14.10", {"start": v(-27.21, 35.08) * mm, "mid": v(-27.1, 35.07) * mm, "end": v(-27, 35.13) * mm});
            skArc(sketch, "E24.14.11", {"start": v(-26.47, 35.7) * mm, "mid": v(-26.42, 35.81) * mm, "end": v(-26.44, 35.93) * mm});
            skArc(sketch, "E24.14.12", {"start": v(-27.16, 37.72) * mm, "mid": v(-27.21, 37.62) * mm, "end": v(-27.2, 37.5) * mm});
            skArc(sketch, "E24.14.13", {"start": v(-28.84, 35.72) * mm, "mid": v(-28.96, 35.73) * mm, "end": v(-29.06, 35.67) * mm});
            skLineSegment(sketch, "E24.15.0", {"start": v(-29.22, 35.5) * mm, "end": v(-29.39, 35.3) * mm});
            skPoint(sketch, "E24.15.1", {"position": v(-29.15, 32.61) * mm});
            skLineSegment(sketch, "E24.15.2", {"start": v(-30.94, 33.2) * mm, "end": v(-29.28, 32.66) * mm});
            skPoint(sketch, "E24.15.3", {"position": v(-28.5, 33.43) * mm});
            skPoint(sketch, "E24.15.4", {"position": v(-31.07, 33.24) * mm});
            skLineSegment(sketch, "E24.15.5", {"start": v(-31.32, 32.93) * mm, "end": v(-31.16, 33.13) * mm});
            skLineSegment(sketch, "E24.15.6", {"start": v(-29.06, 32.72) * mm, "end": v(-28.58, 33.33) * mm});
            skPoint(sketch, "E24.15.7", {"position": v(-29.48, 35.2) * mm});
            skLineSegment(sketch, "E24.15.8", {"start": v(-31.16, 33.13) * mm, "end": v(-29.39, 35.3) * mm});
            skLineSegment(sketch, "E24.15.9", {"start": v(-28.56, 33.55) * mm, "end": v(-29.41, 35.07) * mm});
            skArc(sketch, "E24.15.10", {"start": v(-29.28, 32.66) * mm, "mid": v(-29.16, 32.66) * mm, "end": v(-29.06, 32.72) * mm});
            skArc(sketch, "E24.15.11", {"start": v(-28.58, 33.33) * mm, "mid": v(-28.53, 33.44) * mm, "end": v(-28.56, 33.55) * mm});
            skArc(sketch, "E24.15.12", {"start": v(-29.39, 35.3) * mm, "mid": v(-29.43, 35.19) * mm, "end": v(-29.41, 35.07) * mm});
            skArc(sketch, "E24.15.13", {"start": v(-30.94, 33.2) * mm, "mid": v(-31.06, 33.2) * mm, "end": v(-31.16, 33.13) * mm});
            skLineSegment(sketch, "E24.16.0", {"start": v(-31.3, 32.95) * mm, "end": v(-31.46, 32.74) * mm});
            skPoint(sketch, "E24.16.1", {"position": v(-31.06, 30.08) * mm});
            skLineSegment(sketch, "E24.16.2", {"start": v(-32.89, 30.55) * mm, "end": v(-31.2, 30.11) * mm});
            skPoint(sketch, "E24.16.3", {"position": v(-30.45, 30.93) * mm});
            skPoint(sketch, "E24.16.4", {"position": v(-33.02, 30.59) * mm});
            skLineSegment(sketch, "E24.16.5", {"start": v(-33.25, 30.26) * mm, "end": v(-33.1, 30.47) * mm});
            skLineSegment(sketch, "E24.16.6", {"start": v(-30.98, 30.19) * mm, "end": v(-30.53, 30.82) * mm});
            skPoint(sketch, "E24.16.7", {"position": v(-31.55, 32.63) * mm});
            skLineSegment(sketch, "E24.16.8", {"start": v(-33.1, 30.47) * mm, "end": v(-31.46, 32.74) * mm});
            skLineSegment(sketch, "E24.16.9", {"start": v(-30.53, 31.05) * mm, "end": v(-31.47, 32.51) * mm});
            skArc(sketch, "E24.16.10", {"start": v(-31.2, 30.11) * mm, "mid": v(-31.08, 30.12) * mm, "end": v(-30.98, 30.19) * mm});
            skArc(sketch, "E24.16.11", {"start": v(-30.53, 30.82) * mm, "mid": v(-30.5, 30.94) * mm, "end": v(-30.53, 31.05) * mm});
            skArc(sketch, "E24.16.12", {"start": v(-31.46, 32.74) * mm, "mid": v(-31.5, 32.63) * mm, "end": v(-31.47, 32.51) * mm});
            skArc(sketch, "E24.16.13", {"start": v(-32.89, 30.55) * mm, "mid": v(-33, 30.55) * mm, "end": v(-33.1, 30.47) * mm});
            skLineSegment(sketch, "E24.17.0", {"start": v(-33.23, 30.28) * mm, "end": v(-33.38, 30.06) * mm});
            skPoint(sketch, "E24.17.1", {"position": v(-32.82, 27.43) * mm});
            skLineSegment(sketch, "E24.17.2", {"start": v(-34.67, 27.8) * mm, "end": v(-32.95, 27.45) * mm});
            skPoint(sketch, "E24.17.3", {"position": v(-32.26, 28.32) * mm});
            skPoint(sketch, "E24.17.4", {"position": v(-34.8, 27.82) * mm});
            skLineSegment(sketch, "E24.17.5", {"start": v(-35, 27.47) * mm, "end": v(-34.88, 27.7) * mm});
            skLineSegment(sketch, "E24.17.6", {"start": v(-32.74, 27.54) * mm, "end": v(-32.33, 28.2) * mm});
            skPoint(sketch, "E24.17.7", {"position": v(-33.46, 29.95) * mm});
            skLineSegment(sketch, "E24.17.8", {"start": v(-34.88, 27.7) * mm, "end": v(-33.38, 30.06) * mm});
            skLineSegment(sketch, "E24.17.9", {"start": v(-32.34, 28.43) * mm, "end": v(-33.37, 29.83) * mm});
            skArc(sketch, "E24.17.10", {"start": v(-32.95, 27.45) * mm, "mid": v(-32.83, 27.47) * mm, "end": v(-32.74, 27.54) * mm});
            skArc(sketch, "E24.17.11", {"start": v(-32.33, 28.2) * mm, "mid": v(-32.3, 28.32) * mm, "end": v(-32.34, 28.43) * mm});
            skArc(sketch, "E24.17.12", {"start": v(-33.38, 30.06) * mm, "mid": v(-33.41, 29.95) * mm, "end": v(-33.37, 29.83) * mm});
            skArc(sketch, "E24.17.13", {"start": v(-34.67, 27.8) * mm, "mid": v(-34.79, 27.78) * mm, "end": v(-34.88, 27.7) * mm});
            skLineSegment(sketch, "E24.18.0", {"start": v(-35, 27.5) * mm, "end": v(-35.13, 27.27) * mm});
            skPoint(sketch, "E24.18.1", {"position": v(-34.4, 24.68) * mm});
            skLineSegment(sketch, "E24.18.2", {"start": v(-36.27, 24.93) * mm, "end": v(-34.54, 24.7) * mm});
            skPoint(sketch, "E24.18.3", {"position": v(-33.9, 25.6) * mm});
            skPoint(sketch, "E24.18.4", {"position": v(-36.41, 24.94) * mm});
            skLineSegment(sketch, "E24.18.5", {"start": v(-36.6, 24.59) * mm, "end": v(-36.48, 24.82) * mm});
            skLineSegment(sketch, "E24.18.6", {"start": v(-34.34, 24.8) * mm, "end": v(-33.97, 25.48) * mm});
            skPoint(sketch, "E24.18.7", {"position": v(-35.2, 27.15) * mm});
            skLineSegment(sketch, "E24.18.8", {"start": v(-36.48, 24.82) * mm, "end": v(-35.13, 27.27) * mm});
            skLineSegment(sketch, "E24.18.9", {"start": v(-34, 25.7) * mm, "end": v(-35.1, 27.04) * mm});
            skArc(sketch, "E24.18.10", {"start": v(-34.54, 24.7) * mm, "mid": v(-34.43, 24.71) * mm, "end": v(-34.34, 24.8) * mm});
            skArc(sketch, "E24.18.11", {"start": v(-33.97, 25.48) * mm, "mid": v(-33.95, 25.6) * mm, "end": v(-34, 25.7) * mm});
            skArc(sketch, "E24.18.12", {"start": v(-35.13, 27.27) * mm, "mid": v(-35.16, 27.15) * mm, "end": v(-35.1, 27.04) * mm});
            skArc(sketch, "E24.18.13", {"start": v(-36.27, 24.93) * mm, "mid": v(-36.4, 24.9) * mm, "end": v(-36.48, 24.82) * mm});
            skLineSegment(sketch, "E24.19.0", {"start": v(-36.59, 24.6) * mm, "end": v(-36.7, 24.38) * mm});
            skPoint(sketch, "E24.19.1", {"position": v(-35.82, 21.83) * mm});
            skLineSegment(sketch, "E24.19.2", {"start": v(-37.7, 21.97) * mm, "end": v(-35.96, 21.84) * mm});
            skPoint(sketch, "E24.19.3", {"position": v(-35.38, 22.79) * mm});
            skPoint(sketch, "E24.19.4", {"position": v(-37.85, 21.98) * mm});
            skLineSegment(sketch, "E24.19.5", {"start": v(-38, 21.61) * mm, "end": v(-37.9, 21.85) * mm});
            skLineSegment(sketch, "E24.19.6", {"start": v(-35.77, 21.96) * mm, "end": v(-35.44, 22.66) * mm});
            skPoint(sketch, "E24.19.7", {"position": v(-36.77, 24.25) * mm});
            skLineSegment(sketch, "E24.19.8", {"start": v(-37.9, 21.85) * mm, "end": v(-36.7, 24.38) * mm});
            skLineSegment(sketch, "E24.19.9", {"start": v(-35.48, 22.89) * mm, "end": v(-36.67, 24.15) * mm});
            skArc(sketch, "E24.19.10", {"start": v(-35.96, 21.84) * mm, "mid": v(-35.85, 21.87) * mm, "end": v(-35.77, 21.96) * mm});
            skArc(sketch, "E24.19.11", {"start": v(-35.44, 22.66) * mm, "mid": v(-35.42, 22.78) * mm, "end": v(-35.48, 22.89) * mm});
            skArc(sketch, "E24.19.12", {"start": v(-36.7, 24.38) * mm, "mid": v(-36.72, 24.26) * mm, "end": v(-36.67, 24.15) * mm});
            skArc(sketch, "E24.19.13", {"start": v(-37.7, 21.97) * mm, "mid": v(-37.82, 21.94) * mm, "end": v(-37.9, 21.85) * mm});
            skLineSegment(sketch, "E24.20.0", {"start": v(-38, 21.63) * mm, "end": v(-38.1, 21.4) * mm});
            skPoint(sketch, "E24.20.1", {"position": v(-37.07, 18.9) * mm});
            skLineSegment(sketch, "E24.20.2", {"start": v(-38.95, 18.93) * mm, "end": v(-37.2, 18.9) * mm});
            skPoint(sketch, "E24.20.3", {"position": v(-36.69, 19.89) * mm});
            skPoint(sketch, "E24.20.4", {"position": v(-39.1, 18.93) * mm});
            skLineSegment(sketch, "E24.20.5", {"start": v(-39.23, 18.56) * mm, "end": v(-39.14, 18.8) * mm});
            skLineSegment(sketch, "E24.20.6", {"start": v(-37.02, 19.04) * mm, "end": v(-36.74, 19.76) * mm});
            skPoint(sketch, "E24.20.7", {"position": v(-38.16, 21.27) * mm});
            skLineSegment(sketch, "E24.20.8", {"start": v(-39.14, 18.8) * mm, "end": v(-38.1, 21.4) * mm});
            skLineSegment(sketch, "E24.20.9", {"start": v(-36.78, 19.98) * mm, "end": v(-38.05, 21.17) * mm});
            skArc(sketch, "E24.20.10", {"start": v(-37.2, 18.9) * mm, "mid": v(-37.1, 18.94) * mm, "end": v(-37.02, 19.04) * mm});
            skArc(sketch, "E24.20.11", {"start": v(-36.74, 19.76) * mm, "mid": v(-36.73, 19.88) * mm, "end": v(-36.78, 19.98) * mm});
            skArc(sketch, "E24.20.12", {"start": v(-38.1, 21.4) * mm, "mid": v(-38.11, 21.28) * mm, "end": v(-38.05, 21.17) * mm});
            skArc(sketch, "E24.20.13", {"start": v(-38.95, 18.93) * mm, "mid": v(-39.07, 18.9) * mm, "end": v(-39.14, 18.8) * mm});
            skLineSegment(sketch, "E24.21.0", {"start": v(-39.22, 18.58) * mm, "end": v(-39.31, 18.33) * mm});
            skPoint(sketch, "E24.21.1", {"position": v(-38.13, 15.91) * mm});
            skLineSegment(sketch, "E24.21.2", {"start": v(-40.01, 15.82) * mm, "end": v(-38.27, 15.9) * mm});
            skPoint(sketch, "E24.21.3", {"position": v(-37.8, 16.91) * mm});
            skPoint(sketch, "E24.21.4", {"position": v(-40.15, 15.81) * mm});
            skLineSegment(sketch, "E24.21.5", {"start": v(-40.27, 15.43) * mm, "end": v(-40.2, 15.68) * mm});
            skLineSegment(sketch, "E24.21.6", {"start": v(-38.09, 16.04) * mm, "end": v(-37.85, 16.79) * mm});
            skPoint(sketch, "E24.21.7", {"position": v(-39.36, 18.2) * mm});
            skLineSegment(sketch, "E24.21.8", {"start": v(-40.2, 15.68) * mm, "end": v(-39.31, 18.33) * mm});
            skLineSegment(sketch, "E24.21.9", {"start": v(-37.91, 17) * mm, "end": v(-39.25, 18.11) * mm});
            skArc(sketch, "E24.21.10", {"start": v(-38.27, 15.9) * mm, "mid": v(-38.16, 15.95) * mm, "end": v(-38.09, 16.04) * mm});
            skArc(sketch, "E24.21.11", {"start": v(-37.85, 16.79) * mm, "mid": v(-37.85, 16.9) * mm, "end": v(-37.91, 17) * mm});
            skArc(sketch, "E24.21.12", {"start": v(-39.31, 18.33) * mm, "mid": v(-39.32, 18.21) * mm, "end": v(-39.25, 18.11) * mm});
            skArc(sketch, "E24.21.13", {"start": v(-40.01, 15.82) * mm, "mid": v(-40.13, 15.78) * mm, "end": v(-40.2, 15.68) * mm});
            skLineSegment(sketch, "E24.22.0", {"start": v(-40.26, 15.45) * mm, "end": v(-40.34, 15.2) * mm});
            skPoint(sketch, "E24.22.1", {"position": v(-39, 12.86) * mm});
            skLineSegment(sketch, "E24.22.2", {"start": v(-40.88, 12.65) * mm, "end": v(-39.15, 12.84) * mm});
            skPoint(sketch, "E24.22.3", {"position": v(-38.75, 13.88) * mm});
            skPoint(sketch, "E24.22.4", {"position": v(-41.02, 12.63) * mm});
            skLineSegment(sketch, "E24.22.5", {"start": v(-41.11, 12.25) * mm, "end": v(-41.05, 12.5) * mm});
            skLineSegment(sketch, "E24.22.6", {"start": v(-38.97, 13) * mm, "end": v(-38.78, 13.75) * mm});
            skPoint(sketch, "E24.22.7", {"position": v(-40.38, 15.07) * mm});
            skLineSegment(sketch, "E24.22.8", {"start": v(-41.05, 12.5) * mm, "end": v(-40.34, 15.2) * mm});
            skLineSegment(sketch, "E24.22.9", {"start": v(-38.86, 13.96) * mm, "end": v(-40.26, 14.98) * mm});
            skArc(sketch, "E24.22.10", {"start": v(-39.15, 12.84) * mm, "mid": v(-39.04, 12.9) * mm, "end": v(-38.97, 13) * mm});
            skArc(sketch, "E24.22.11", {"start": v(-38.78, 13.75) * mm, "mid": v(-38.79, 13.86) * mm, "end": v(-38.86, 13.96) * mm});
            skArc(sketch, "E24.22.12", {"start": v(-40.34, 15.2) * mm, "mid": v(-40.33, 15.08) * mm, "end": v(-40.26, 14.98) * mm});
            skArc(sketch, "E24.22.13", {"start": v(-40.88, 12.65) * mm, "mid": v(-41, 12.6) * mm, "end": v(-41.05, 12.5) * mm});
            skLineSegment(sketch, "E24.23.0", {"start": v(-41.1, 12.27) * mm, "end": v(-41.17, 12.02) * mm});
            skPoint(sketch, "E24.23.1", {"position": v(-39.7, 9.76) * mm});
            skLineSegment(sketch, "E24.23.2", {"start": v(-41.56, 9.43) * mm, "end": v(-39.83, 9.73) * mm});
            skPoint(sketch, "E24.23.3", {"position": v(-39.5, 10.79) * mm});
            skPoint(sketch, "E24.23.4", {"position": v(-41.7, 9.41) * mm});
            skLineSegment(sketch, "E24.23.5", {"start": v(-41.76, 9.02) * mm, "end": v(-41.72, 9.27) * mm});
            skLineSegment(sketch, "E24.23.6", {"start": v(-39.67, 9.9) * mm, "end": v(-39.53, 10.66) * mm});
            skPoint(sketch, "E24.23.7", {"position": v(-41.2, 11.88) * mm});
            skLineSegment(sketch, "E24.23.8", {"start": v(-41.72, 9.27) * mm, "end": v(-41.17, 12.02) * mm});
            skLineSegment(sketch, "E24.23.9", {"start": v(-39.61, 10.86) * mm, "end": v(-41.08, 11.8) * mm});
            skArc(sketch, "E24.23.10", {"start": v(-39.83, 9.73) * mm, "mid": v(-39.73, 9.79) * mm, "end": v(-39.67, 9.9) * mm});
            skArc(sketch, "E24.23.11", {"start": v(-39.53, 10.66) * mm, "mid": v(-39.54, 10.77) * mm, "end": v(-39.61, 10.86) * mm});
            skArc(sketch, "E24.23.12", {"start": v(-41.17, 12.02) * mm, "mid": v(-41.16, 11.9) * mm, "end": v(-41.08, 11.8) * mm});
            skArc(sketch, "E24.23.13", {"start": v(-41.56, 9.43) * mm, "mid": v(-41.66, 9.38) * mm, "end": v(-41.72, 9.27) * mm});
            skLineSegment(sketch, "E24.24.0", {"start": v(-41.76, 9.04) * mm, "end": v(-41.8, 8.78) * mm});
            skPoint(sketch, "E24.24.1", {"position": v(-40.2, 6.62) * mm});
            skLineSegment(sketch, "E24.24.2", {"start": v(-42.03, 6.18) * mm, "end": v(-40.33, 6.59) * mm});
            skPoint(sketch, "E24.24.3", {"position": v(-40.06, 7.66) * mm});
            skPoint(sketch, "E24.24.4", {"position": v(-42.17, 6.15) * mm});
            skLineSegment(sketch, "E24.24.5", {"start": v(-42.21, 5.75) * mm, "end": v(-42.18, 6.01) * mm});
            skLineSegment(sketch, "E24.24.6", {"start": v(-40.18, 6.76) * mm, "end": v(-40.08, 7.53) * mm});
            skPoint(sketch, "E24.24.7", {"position": v(-41.82, 8.65) * mm});
            skLineSegment(sketch, "E24.24.8", {"start": v(-42.18, 6.01) * mm, "end": v(-41.8, 8.78) * mm});
            skLineSegment(sketch, "E24.24.9", {"start": v(-40.18, 7.73) * mm, "end": v(-41.7, 8.58) * mm});
            skArc(sketch, "E24.24.10", {"start": v(-40.33, 6.59) * mm, "mid": v(-40.23, 6.65) * mm, "end": v(-40.18, 6.76) * mm});
            skArc(sketch, "E24.24.11", {"start": v(-40.08, 7.53) * mm, "mid": v(-40.1, 7.64) * mm, "end": v(-40.18, 7.73) * mm});
            skArc(sketch, "E24.24.12", {"start": v(-41.8, 8.78) * mm, "mid": v(-41.78, 8.66) * mm, "end": v(-41.7, 8.58) * mm});
            skArc(sketch, "E24.24.13", {"start": v(-42.03, 6.18) * mm, "mid": v(-42.14, 6.12) * mm, "end": v(-42.18, 6.01) * mm});
            skLineSegment(sketch, "E24.25.0", {"start": v(-42.2, 5.78) * mm, "end": v(-42.24, 5.52) * mm});
            skPoint(sketch, "E24.25.1", {"position": v(-40.5, 3.46) * mm});
            skLineSegment(sketch, "E24.25.2", {"start": v(-42.3, 2.91) * mm, "end": v(-40.64, 3.42) * mm});
            skPoint(sketch, "E24.25.3", {"position": v(-40.44, 4.5) * mm});
            skPoint(sketch, "E24.25.4", {"position": v(-42.44, 2.87) * mm});
            skLineSegment(sketch, "E24.25.5", {"start": v(-42.46, 2.47) * mm, "end": v(-42.45, 2.73) * mm});
            skLineSegment(sketch, "E24.25.6", {"start": v(-40.5, 3.6) * mm, "end": v(-40.44, 4.37) * mm});
            skPoint(sketch, "E24.25.7", {"position": v(-42.25, 5.38) * mm});
            skLineSegment(sketch, "E24.25.8", {"start": v(-42.45, 2.73) * mm, "end": v(-42.24, 5.52) * mm});
            skLineSegment(sketch, "E24.25.9", {"start": v(-40.56, 4.56) * mm, "end": v(-42.13, 5.32) * mm});
            skArc(sketch, "E24.25.10", {"start": v(-40.64, 3.42) * mm, "mid": v(-40.54, 3.48) * mm, "end": v(-40.5, 3.6) * mm});
            skArc(sketch, "E24.25.11", {"start": v(-40.44, 4.37) * mm, "mid": v(-40.47, 4.48) * mm, "end": v(-40.56, 4.56) * mm});
            skArc(sketch, "E24.25.12", {"start": v(-42.24, 5.52) * mm, "mid": v(-42.21, 5.4) * mm, "end": v(-42.13, 5.32) * mm});
            skArc(sketch, "E24.25.13", {"start": v(-42.3, 2.91) * mm, "mid": v(-42.4, 2.84) * mm, "end": v(-42.45, 2.73) * mm});
            skLineSegment(sketch, "E24.26.0", {"start": v(-42.46, 2.5) * mm, "end": v(-42.47, 2.23) * mm});
            skPoint(sketch, "E24.26.1", {"position": v(-40.62, 0.28) * mm});
            skLineSegment(sketch, "E24.26.2", {"start": v(-42.39, -0.37) * mm, "end": v(-40.75, 0.23) * mm});
            skPoint(sketch, "E24.26.3", {"position": v(-40.61, 1.33) * mm});
            skPoint(sketch, "E24.26.4", {"position": v(-42.52, -0.42) * mm});
            skLineSegment(sketch, "E24.26.5", {"start": v(-42.51, -0.82) * mm, "end": v(-42.52, -0.56) * mm});
            skLineSegment(sketch, "E24.26.6", {"start": v(-40.62, 0.42) * mm, "end": v(-40.61, 1.2) * mm});
            skPoint(sketch, "E24.26.7", {"position": v(-42.48, 2.1) * mm});
            skLineSegment(sketch, "E24.26.8", {"start": v(-42.52, -0.56) * mm, "end": v(-42.47, 2.23) * mm});
            skLineSegment(sketch, "E24.26.9", {"start": v(-40.74, 1.38) * mm, "end": v(-42.35, 2.04) * mm});
            skArc(sketch, "E24.26.10", {"start": v(-40.75, 0.23) * mm, "mid": v(-40.65, 0.3) * mm, "end": v(-40.62, 0.42) * mm});
            skArc(sketch, "E24.26.11", {"start": v(-40.61, 1.2) * mm, "mid": v(-40.65, 1.3) * mm, "end": v(-40.74, 1.38) * mm});
            skArc(sketch, "E24.26.12", {"start": v(-42.47, 2.23) * mm, "mid": v(-42.44, 2.12) * mm, "end": v(-42.35, 2.04) * mm});
            skArc(sketch, "E24.26.13", {"start": v(-42.39, -0.37) * mm, "mid": v(-42.48, -0.45) * mm, "end": v(-42.52, -0.56) * mm});
            skLineSegment(sketch, "E24.27.0", {"start": v(-42.51, -0.8) * mm, "end": v(-42.5, -1.06) * mm});
            skPoint(sketch, "E24.27.1", {"position": v(-40.54, -2.9) * mm});
            skLineSegment(sketch, "E24.27.2", {"start": v(-42.26, -3.66) * mm, "end": v(-40.67, -2.95) * mm});
            skPoint(sketch, "E24.27.3", {"position": v(-40.6, -1.85) * mm});
            skPoint(sketch, "E24.27.4", {"position": v(-42.4, -3.71) * mm});
            skLineSegment(sketch, "E24.27.5", {"start": v(-42.36, -4.11) * mm, "end": v(-42.38, -3.86) * mm});
            skLineSegment(sketch, "E24.27.6", {"start": v(-40.55, -2.76) * mm, "end": v(-40.59, -1.98) * mm});
            skPoint(sketch, "E24.27.7", {"position": v(-42.5, -1.2) * mm});
            skLineSegment(sketch, "E24.27.8", {"start": v(-42.38, -3.86) * mm, "end": v(-42.5, -1.06) * mm});
            skLineSegment(sketch, "E24.27.9", {"start": v(-40.73, -1.8) * mm, "end": v(-42.37, -1.25) * mm});
            skArc(sketch, "E24.27.10", {"start": v(-40.67, -2.95) * mm, "mid": v(-40.58, -2.87) * mm, "end": v(-40.55, -2.76) * mm});
            skArc(sketch, "E24.27.11", {"start": v(-40.59, -1.98) * mm, "mid": v(-40.63, -1.87) * mm, "end": v(-40.73, -1.8) * mm});
            skArc(sketch, "E24.27.12", {"start": v(-42.5, -1.06) * mm, "mid": v(-42.47, -1.17) * mm, "end": v(-42.37, -1.25) * mm});
            skArc(sketch, "E24.27.13", {"start": v(-42.26, -3.66) * mm, "mid": v(-42.35, -3.74) * mm, "end": v(-42.38, -3.86) * mm});
            skLineSegment(sketch, "E24.28.0", {"start": v(-42.36, -4.1) * mm, "end": v(-42.34, -4.35) * mm});
            skPoint(sketch, "E24.28.1", {"position": v(-40.27, -6.06) * mm});
            skLineSegment(sketch, "E24.28.2", {"start": v(-41.94, -6.93) * mm, "end": v(-40.39, -6.13) * mm});
            skPoint(sketch, "E24.28.3", {"position": v(-40.39, -5.02) * mm});
            skPoint(sketch, "E24.28.4", {"position": v(-42.07, -7) * mm});
            skLineSegment(sketch, "E24.28.5", {"start": v(-42.01, -7.39) * mm, "end": v(-42.05, -7.13) * mm});
            skLineSegment(sketch, "E24.28.6", {"start": v(-40.28, -5.92) * mm, "end": v(-40.37, -5.15) * mm});
            skPoint(sketch, "E24.28.7", {"position": v(-42.33, -4.49) * mm});
            skLineSegment(sketch, "E24.28.8", {"start": v(-42.05, -7.13) * mm, "end": v(-42.34, -4.35) * mm});
            skLineSegment(sketch, "E24.28.9", {"start": v(-40.52, -4.98) * mm, "end": v(-42.2, -4.53) * mm});
            skArc(sketch, "E24.28.10", {"start": v(-40.39, -6.13) * mm, "mid": v(-40.3, -6.04) * mm, "end": v(-40.28, -5.92) * mm});
            skArc(sketch, "E24.28.11", {"start": v(-40.37, -5.15) * mm, "mid": v(-40.42, -5.05) * mm, "end": v(-40.52, -4.98) * mm});
            skArc(sketch, "E24.28.12", {"start": v(-42.34, -4.35) * mm, "mid": v(-42.3, -4.46) * mm, "end": v(-42.2, -4.53) * mm});
            skArc(sketch, "E24.28.13", {"start": v(-41.94, -6.93) * mm, "mid": v(-42.03, -7.01) * mm, "end": v(-42.05, -7.13) * mm});
            skLineSegment(sketch, "E24.29.0", {"start": v(-42.01, -7.37) * mm, "end": v(-41.98, -7.62) * mm});
            skPoint(sketch, "E24.29.1", {"position": v(-39.8, -9.2) * mm});
            skLineSegment(sketch, "E24.29.2", {"start": v(-41.42, -10.17) * mm, "end": v(-39.92, -9.28) * mm});
            skPoint(sketch, "E24.29.3", {"position": v(-39.99, -8.17) * mm});
            skPoint(sketch, "E24.29.4", {"position": v(-41.54, -10.24) * mm});
            skLineSegment(sketch, "E24.29.5", {"start": v(-41.46, -10.64) * mm, "end": v(-41.51, -10.38) * mm});
            skLineSegment(sketch, "E24.29.6", {"start": v(-39.82, -9.07) * mm, "end": v(-39.96, -8.3) * mm});
            skPoint(sketch, "E24.29.7", {"position": v(-41.96, -7.76) * mm});
            skLineSegment(sketch, "E24.29.8", {"start": v(-41.51, -10.38) * mm, "end": v(-41.98, -7.62) * mm});
            skLineSegment(sketch, "E24.29.9", {"start": v(-40.12, -8.14) * mm, "end": v(-41.82, -7.8) * mm});
            skArc(sketch, "E24.29.10", {"start": v(-39.92, -9.28) * mm, "mid": v(-39.84, -9.19) * mm, "end": v(-39.82, -9.07) * mm});
            skArc(sketch, "E24.29.11", {"start": v(-39.96, -8.3) * mm, "mid": v(-40.02, -8.2) * mm, "end": v(-40.12, -8.14) * mm});
            skArc(sketch, "E24.29.12", {"start": v(-41.98, -7.62) * mm, "mid": v(-41.93, -7.73) * mm, "end": v(-41.82, -7.8) * mm});
            skArc(sketch, "E24.29.13", {"start": v(-41.42, -10.17) * mm, "mid": v(-41.5, -10.26) * mm, "end": v(-41.51, -10.38) * mm});
            skLineSegment(sketch, "E24.30.0", {"start": v(-41.47, -10.61) * mm, "end": v(-41.42, -10.87) * mm});
            skPoint(sketch, "E24.30.1", {"position": v(-39.14, -12.31) * mm});
            skLineSegment(sketch, "E24.30.2", {"start": v(-40.7, -13.38) * mm, "end": v(-39.26, -12.4) * mm});
            skPoint(sketch, "E24.30.3", {"position": v(-39.4, -11.3) * mm});
            skPoint(sketch, "E24.30.4", {"position": v(-40.82, -13.46) * mm});
            skLineSegment(sketch, "E24.30.5", {"start": v(-40.71, -13.84) * mm, "end": v(-40.78, -13.6) * mm});
            skLineSegment(sketch, "E24.30.6", {"start": v(-39.18, -12.18) * mm, "end": v(-39.36, -11.42) * mm});
            skPoint(sketch, "E24.30.7", {"position": v(-41.39, -11) * mm});
            skLineSegment(sketch, "E24.30.8", {"start": v(-40.78, -13.6) * mm, "end": v(-41.42, -10.87) * mm});
            skLineSegment(sketch, "E24.30.9", {"start": v(-39.53, -11.27) * mm, "end": v(-41.25, -11.03) * mm});
            skArc(sketch, "E24.30.10", {"start": v(-39.26, -12.4) * mm, "mid": v(-39.18, -12.3) * mm, "end": v(-39.18, -12.18) * mm});
            skArc(sketch, "E24.30.11", {"start": v(-39.36, -11.42) * mm, "mid": v(-39.42, -11.32) * mm, "end": v(-39.53, -11.27) * mm});
            skArc(sketch, "E24.30.12", {"start": v(-41.42, -10.87) * mm, "mid": v(-41.36, -10.97) * mm, "end": v(-41.25, -11.03) * mm});
            skArc(sketch, "E24.30.13", {"start": v(-40.7, -13.38) * mm, "mid": v(-40.78, -13.47) * mm, "end": v(-40.78, -13.6) * mm});
            skLineSegment(sketch, "E24.31.0", {"start": v(-40.72, -13.82) * mm, "end": v(-40.65, -14.07) * mm});
            skPoint(sketch, "E24.31.1", {"position": v(-38.3, -15.38) * mm});
            skLineSegment(sketch, "E24.31.2", {"start": v(-39.79, -16.53) * mm, "end": v(-38.4, -15.46) * mm});
            skPoint(sketch, "E24.31.3", {"position": v(-38.6, -14.37) * mm});
            skPoint(sketch, "E24.31.4", {"position": v(-39.9, -16.62) * mm});
            skLineSegment(sketch, "E24.31.5", {"start": v(-39.77, -17) * mm, "end": v(-39.86, -16.75) * mm});
            skLineSegment(sketch, "E24.31.6", {"start": v(-38.34, -15.25) * mm, "end": v(-38.57, -14.5) * mm});
            skPoint(sketch, "E24.31.7", {"position": v(-40.62, -14.2) * mm});
            skLineSegment(sketch, "E24.31.8", {"start": v(-39.86, -16.75) * mm, "end": v(-40.65, -14.07) * mm});
            skLineSegment(sketch, "E24.31.9", {"start": v(-38.74, -14.36) * mm, "end": v(-40.48, -14.22) * mm});
            skArc(sketch, "E24.31.10", {"start": v(-38.4, -15.46) * mm, "mid": v(-38.34, -15.36) * mm, "end": v(-38.34, -15.25) * mm});
            skArc(sketch, "E24.31.11", {"start": v(-38.57, -14.5) * mm, "mid": v(-38.63, -14.4) * mm, "end": v(-38.74, -14.36) * mm});
            skArc(sketch, "E24.31.12", {"start": v(-40.65, -14.07) * mm, "mid": v(-40.59, -14.17) * mm, "end": v(-40.48, -14.22) * mm});
            skArc(sketch, "E24.31.13", {"start": v(-39.79, -16.53) * mm, "mid": v(-39.86, -16.63) * mm, "end": v(-39.86, -16.75) * mm});
            skLineSegment(sketch, "E24.32.0", {"start": v(-39.78, -16.98) * mm, "end": v(-39.7, -17.22) * mm});
            skPoint(sketch, "E24.32.1", {"position": v(-37.27, -18.38) * mm});
            skLineSegment(sketch, "E24.32.2", {"start": v(-38.68, -19.63) * mm, "end": v(-37.37, -18.48) * mm});
            skPoint(sketch, "E24.32.3", {"position": v(-37.64, -17.4) * mm});
            skPoint(sketch, "E24.32.4", {"position": v(-38.8, -19.72) * mm});
            skLineSegment(sketch, "E24.32.5", {"start": v(-38.64, -20.1) * mm, "end": v(-38.74, -19.85) * mm});
            skLineSegment(sketch, "E24.32.6", {"start": v(-37.32, -18.25) * mm, "end": v(-37.6, -17.53) * mm});
            skPoint(sketch, "E24.32.7", {"position": v(-39.66, -17.36) * mm});
            skLineSegment(sketch, "E24.32.8", {"start": v(-38.74, -19.85) * mm, "end": v(-39.7, -17.22) * mm});
            skLineSegment(sketch, "E24.32.9", {"start": v(-37.77, -17.4) * mm, "end": v(-39.51, -17.36) * mm});
            skArc(sketch, "E24.32.10", {"start": v(-37.37, -18.48) * mm, "mid": v(-37.31, -18.37) * mm, "end": v(-37.32, -18.25) * mm});
            skArc(sketch, "E24.32.11", {"start": v(-37.6, -17.53) * mm, "mid": v(-37.66, -17.43) * mm, "end": v(-37.77, -17.4) * mm});
            skArc(sketch, "E24.32.12", {"start": v(-39.7, -17.22) * mm, "mid": v(-39.63, -17.32) * mm, "end": v(-39.51, -17.36) * mm});
            skArc(sketch, "E24.32.13", {"start": v(-38.68, -19.63) * mm, "mid": v(-38.75, -19.73) * mm, "end": v(-38.74, -19.85) * mm});
            skLineSegment(sketch, "E24.33.0", {"start": v(-38.65, -20.07) * mm, "end": v(-38.55, -20.31) * mm});
            skPoint(sketch, "E24.33.1", {"position": v(-36.06, -21.32) * mm});
            skLineSegment(sketch, "E24.33.2", {"start": v(-37.4, -22.65) * mm, "end": v(-36.15, -21.42) * mm});
            skPoint(sketch, "E24.33.3", {"position": v(-36.49, -20.36) * mm});
            skPoint(sketch, "E24.33.4", {"position": v(-37.5, -22.75) * mm});
            skLineSegment(sketch, "E24.33.5", {"start": v(-37.32, -23.11) * mm, "end": v(-37.43, -22.88) * mm});
            skLineSegment(sketch, "E24.33.6", {"start": v(-36.11, -21.2) * mm, "end": v(-36.43, -20.49) * mm});
            skPoint(sketch, "E24.33.7", {"position": v(-38.5, -20.44) * mm});
            skLineSegment(sketch, "E24.33.8", {"start": v(-37.43, -22.88) * mm, "end": v(-38.55, -20.31) * mm});
            skLineSegment(sketch, "E24.33.9", {"start": v(-36.62, -20.37) * mm, "end": v(-38.36, -20.44) * mm});
            skArc(sketch, "E24.33.10", {"start": v(-36.15, -21.42) * mm, "mid": v(-36.1, -21.31) * mm, "end": v(-36.11, -21.2) * mm});
            skArc(sketch, "E24.33.11", {"start": v(-36.43, -20.49) * mm, "mid": v(-36.5, -20.4) * mm, "end": v(-36.62, -20.37) * mm});
            skArc(sketch, "E24.33.12", {"start": v(-38.55, -20.31) * mm, "mid": v(-38.48, -20.4) * mm, "end": v(-38.36, -20.44) * mm});
            skArc(sketch, "E24.33.13", {"start": v(-37.4, -22.65) * mm, "mid": v(-37.45, -22.76) * mm, "end": v(-37.43, -22.88) * mm});
            skLineSegment(sketch, "E24.34.0", {"start": v(-37.33, -23.1) * mm, "end": v(-37.22, -23.32) * mm});
            skPoint(sketch, "E24.34.1", {"position": v(-34.67, -24.18) * mm});
            skLineSegment(sketch, "E24.34.2", {"start": v(-35.92, -25.59) * mm, "end": v(-34.76, -24.28) * mm});
            skPoint(sketch, "E24.34.3", {"position": v(-35.16, -23.25) * mm});
            skPoint(sketch, "E24.34.4", {"position": v(-36.02, -25.7) * mm});
            skLineSegment(sketch, "E24.34.5", {"start": v(-35.82, -26.04) * mm, "end": v(-35.95, -25.82) * mm});
            skLineSegment(sketch, "E24.34.6", {"start": v(-34.73, -24.06) * mm, "end": v(-35.1, -23.37) * mm});
            skPoint(sketch, "E24.34.7", {"position": v(-37.16, -23.45) * mm});
            skLineSegment(sketch, "E24.34.8", {"start": v(-35.95, -25.82) * mm, "end": v(-37.22, -23.32) * mm});
            skLineSegment(sketch, "E24.34.9", {"start": v(-35.3, -23.26) * mm, "end": v(-37.02, -23.44) * mm});
            skArc(sketch, "E24.34.10", {"start": v(-34.76, -24.28) * mm, "mid": v(-34.71, -24.17) * mm, "end": v(-34.73, -24.06) * mm});
            skArc(sketch, "E24.34.11", {"start": v(-35.1, -23.37) * mm, "mid": v(-35.18, -23.29) * mm, "end": v(-35.3, -23.26) * mm});
            skArc(sketch, "E24.34.12", {"start": v(-37.22, -23.32) * mm, "mid": v(-37.14, -23.41) * mm, "end": v(-37.02, -23.44) * mm});
            skArc(sketch, "E24.34.13", {"start": v(-35.92, -25.59) * mm, "mid": v(-35.97, -25.7) * mm, "end": v(-35.95, -25.82) * mm});
            skLineSegment(sketch, "E24.35.0", {"start": v(-35.84, -26.02) * mm, "end": v(-35.71, -26.25) * mm});
            skPoint(sketch, "E24.35.1", {"position": v(-33.1, -26.95) * mm});
            skLineSegment(sketch, "E24.35.2", {"start": v(-34.27, -28.43) * mm, "end": v(-33.2, -27.06) * mm});
            skPoint(sketch, "E24.35.3", {"position": v(-33.65, -26.05) * mm});
            skPoint(sketch, "E24.35.4", {"position": v(-34.36, -28.54) * mm});
            skLineSegment(sketch, "E24.35.5", {"start": v(-34.15, -28.88) * mm, "end": v(-34.29, -28.66) * mm});
            skLineSegment(sketch, "E24.35.6", {"start": v(-33.18, -26.83) * mm, "end": v(-33.58, -26.16) * mm});
            skPoint(sketch, "E24.35.7", {"position": v(-35.64, -26.37) * mm});
            skLineSegment(sketch, "E24.35.8", {"start": v(-34.29, -28.66) * mm, "end": v(-35.71, -26.25) * mm});
            skLineSegment(sketch, "E24.35.9", {"start": v(-33.79, -26.07) * mm, "end": v(-35.5, -26.35) * mm});
            skArc(sketch, "E24.35.10", {"start": v(-33.2, -27.06) * mm, "mid": v(-33.15, -26.95) * mm, "end": v(-33.18, -26.83) * mm});
            skArc(sketch, "E24.35.11", {"start": v(-33.58, -26.16) * mm, "mid": v(-33.67, -26.09) * mm, "end": v(-33.79, -26.07) * mm});
            skArc(sketch, "E24.35.12", {"start": v(-35.71, -26.25) * mm, "mid": v(-35.62, -26.33) * mm, "end": v(-35.5, -26.35) * mm});
            skArc(sketch, "E24.35.13", {"start": v(-34.27, -28.43) * mm, "mid": v(-34.32, -28.54) * mm, "end": v(-34.29, -28.66) * mm});
            skLineSegment(sketch, "E24.36.0", {"start": v(-34.16, -28.86) * mm, "end": v(-34.02, -29.08) * mm});
            skPoint(sketch, "E24.36.1", {"position": v(-31.38, -29.62) * mm});
            skLineSegment(sketch, "E24.36.2", {"start": v(-32.46, -31.17) * mm, "end": v(-31.46, -29.73) * mm});
            skPoint(sketch, "E24.36.3", {"position": v(-31.98, -28.75) * mm});
            skPoint(sketch, "E24.36.4", {"position": v(-32.54, -31.28) * mm});
            skLineSegment(sketch, "E24.36.5", {"start": v(-32.3, -31.6) * mm, "end": v(-32.45, -31.4) * mm});
            skLineSegment(sketch, "E24.36.6", {"start": v(-31.46, -29.5) * mm, "end": v(-31.9, -28.86) * mm});
            skPoint(sketch, "E24.36.7", {"position": v(-33.95, -29.2) * mm});
            skLineSegment(sketch, "E24.36.8", {"start": v(-32.45, -31.4) * mm, "end": v(-34.02, -29.08) * mm});
            skLineSegment(sketch, "E24.36.9", {"start": v(-32.11, -28.78) * mm, "end": v(-33.8, -29.17) * mm});
            skArc(sketch, "E24.36.10", {"start": v(-31.46, -29.73) * mm, "mid": v(-31.43, -29.62) * mm, "end": v(-31.46, -29.5) * mm});
            skArc(sketch, "E24.36.11", {"start": v(-31.9, -28.86) * mm, "mid": v(-32, -28.8) * mm, "end": v(-32.11, -28.78) * mm});
            skArc(sketch, "E24.36.12", {"start": v(-34.02, -29.08) * mm, "mid": v(-33.93, -29.16) * mm, "end": v(-33.8, -29.17) * mm});
            skArc(sketch, "E24.36.13", {"start": v(-32.46, -31.17) * mm, "mid": v(-32.5, -31.28) * mm, "end": v(-32.45, -31.4) * mm});
            skLineSegment(sketch, "E24.37.0", {"start": v(-32.32, -31.59) * mm, "end": v(-32.17, -31.8) * mm});
            skPoint(sketch, "E24.37.1", {"position": v(-29.5, -32.17) * mm});
            skLineSegment(sketch, "E24.37.2", {"start": v(-30.47, -33.79) * mm, "end": v(-29.57, -32.3) * mm});
            skPoint(sketch, "E24.37.3", {"position": v(-30.15, -31.35) * mm});
            skPoint(sketch, "E24.37.4", {"position": v(-30.55, -33.9) * mm});
            skLineSegment(sketch, "E24.37.5", {"start": v(-30.3, -34.22) * mm, "end": v(-30.46, -34.02) * mm});
            skLineSegment(sketch, "E24.37.6", {"start": v(-29.58, -32.07) * mm, "end": v(-30.06, -31.45) * mm});
            skPoint(sketch, "E24.37.7", {"position": v(-32.08, -31.91) * mm});
            skLineSegment(sketch, "E24.37.8", {"start": v(-30.46, -34.02) * mm, "end": v(-32.17, -31.8) * mm});
            skLineSegment(sketch, "E24.37.9", {"start": v(-30.28, -31.39) * mm, "end": v(-31.95, -31.87) * mm});
            skArc(sketch, "E24.37.10", {"start": v(-29.57, -32.3) * mm, "mid": v(-29.54, -32.18) * mm, "end": v(-29.58, -32.07) * mm});
            skArc(sketch, "E24.37.11", {"start": v(-30.06, -31.45) * mm, "mid": v(-30.16, -31.39) * mm, "end": v(-30.28, -31.39) * mm});
            skArc(sketch, "E24.37.12", {"start": v(-32.17, -31.8) * mm, "mid": v(-32.07, -31.87) * mm, "end": v(-31.95, -31.87) * mm});
            skArc(sketch, "E24.37.13", {"start": v(-30.47, -33.79) * mm, "mid": v(-30.5, -33.9) * mm, "end": v(-30.46, -34.02) * mm});
            skLineSegment(sketch, "E24.38.0", {"start": v(-30.3, -34.2) * mm, "end": v(-30.15, -34.4) * mm});
            skPoint(sketch, "E24.38.1", {"position": v(-27.46, -34.61) * mm});
            skLineSegment(sketch, "E24.38.2", {"start": v(-28.34, -36.28) * mm, "end": v(-27.52, -34.74) * mm});
            skPoint(sketch, "E24.38.3", {"position": v(-28.16, -33.83) * mm});
            skPoint(sketch, "E24.38.4", {"position": v(-28.4, -36.4) * mm});
            skLineSegment(sketch, "E24.38.5", {"start": v(-28.13, -36.7) * mm, "end": v(-28.3, -36.51) * mm});
            skLineSegment(sketch, "E24.38.6", {"start": v(-27.55, -34.5) * mm, "end": v(-28.07, -33.93) * mm});
            skPoint(sketch, "E24.38.7", {"position": v(-30.06, -34.5) * mm});
            skLineSegment(sketch, "E24.38.8", {"start": v(-28.3, -36.51) * mm, "end": v(-30.15, -34.4) * mm});
            skLineSegment(sketch, "E24.38.9", {"start": v(-28.29, -33.87) * mm, "end": v(-29.92, -34.46) * mm});
            skArc(sketch, "E24.38.10", {"start": v(-27.52, -34.74) * mm, "mid": v(-27.5, -34.62) * mm, "end": v(-27.55, -34.5) * mm});
            skArc(sketch, "E24.38.11", {"start": v(-28.07, -33.93) * mm, "mid": v(-28.17, -33.87) * mm, "end": v(-28.29, -33.87) * mm});
            skArc(sketch, "E24.38.12", {"start": v(-30.15, -34.4) * mm, "mid": v(-30.04, -34.47) * mm, "end": v(-29.92, -34.46) * mm});
            skArc(sketch, "E24.38.13", {"start": v(-28.34, -36.28) * mm, "mid": v(-28.36, -36.4) * mm, "end": v(-28.3, -36.51) * mm});
            skLineSegment(sketch, "E24.39.0", {"start": v(-28.15, -36.68) * mm, "end": v(-27.97, -36.87) * mm});
            skPoint(sketch, "E24.39.1", {"position": v(-25.28, -36.92) * mm});
            skLineSegment(sketch, "E24.39.2", {"start": v(-26.05, -38.64) * mm, "end": v(-25.33, -37.05) * mm});
            skPoint(sketch, "E24.39.3", {"position": v(-26.02, -36.18) * mm});
            skPoint(sketch, "E24.39.4", {"position": v(-26.1, -38.77) * mm});
            skLineSegment(sketch, "E24.39.5", {"start": v(-25.82, -39.05) * mm, "end": v(-26, -38.87) * mm});
            skLineSegment(sketch, "E24.39.6", {"start": v(-25.38, -36.83) * mm, "end": v(-25.93, -36.28) * mm});
            skPoint(sketch, "E24.39.7", {"position": v(-27.88, -36.98) * mm});
            skLineSegment(sketch, "E24.39.8", {"start": v(-26, -38.87) * mm, "end": v(-27.97, -36.87) * mm});
            skLineSegment(sketch, "E24.39.9", {"start": v(-26.15, -36.23) * mm, "end": v(-27.75, -36.92) * mm});
            skArc(sketch, "E24.39.10", {"start": v(-25.33, -37.05) * mm, "mid": v(-25.32, -36.93) * mm, "end": v(-25.38, -36.83) * mm});
            skArc(sketch, "E24.39.11", {"start": v(-25.93, -36.28) * mm, "mid": v(-26.03, -36.22) * mm, "end": v(-26.15, -36.23) * mm});
            skArc(sketch, "E24.39.12", {"start": v(-27.97, -36.87) * mm, "mid": v(-27.87, -36.93) * mm, "end": v(-27.75, -36.92) * mm});
            skArc(sketch, "E24.39.13", {"start": v(-26.05, -38.64) * mm, "mid": v(-26.06, -38.76) * mm, "end": v(-26, -38.87) * mm});
            skLineSegment(sketch, "E24.40.0", {"start": v(-25.84, -39.03) * mm, "end": v(-25.65, -39.2) * mm});
            skPoint(sketch, "E24.40.1", {"position": v(-22.96, -39.1) * mm});
            skLineSegment(sketch, "E24.40.2", {"start": v(-23.63, -40.86) * mm, "end": v(-23, -39.22) * mm});
            skPoint(sketch, "E24.40.3", {"position": v(-23.75, -38.4) * mm});
            skPoint(sketch, "E24.40.4", {"position": v(-23.68, -41) * mm});
            skLineSegment(sketch, "E24.40.5", {"start": v(-23.37, -41.25) * mm, "end": v(-23.57, -41.08) * mm});
            skLineSegment(sketch, "E24.40.6", {"start": v(-23.06, -39) * mm, "end": v(-23.65, -38.49) * mm});
            skPoint(sketch, "E24.40.7", {"position": v(-25.55, -39.3) * mm});
            skLineSegment(sketch, "E24.40.8", {"start": v(-23.57, -41.08) * mm, "end": v(-25.65, -39.2) * mm});
            skLineSegment(sketch, "E24.40.9", {"start": v(-23.87, -38.46) * mm, "end": v(-25.42, -39.24) * mm});
            skArc(sketch, "E24.40.10", {"start": v(-23, -39.22) * mm, "mid": v(-23, -39.1) * mm, "end": v(-23.06, -39) * mm});
            skArc(sketch, "E24.40.11", {"start": v(-23.65, -38.49) * mm, "mid": v(-23.75, -38.44) * mm, "end": v(-23.87, -38.46) * mm});
            skArc(sketch, "E24.40.12", {"start": v(-25.65, -39.2) * mm, "mid": v(-25.54, -39.26) * mm, "end": v(-25.42, -39.24) * mm});
            skArc(sketch, "E24.40.13", {"start": v(-23.63, -40.86) * mm, "mid": v(-23.63, -40.98) * mm, "end": v(-23.57, -41.08) * mm});
            skLineSegment(sketch, "E24.41.0", {"start": v(-23.39, -41.23) * mm, "end": v(-23.2, -41.4) * mm});
            skPoint(sketch, "E24.41.1", {"position": v(-20.51, -41.12) * mm});
            skLineSegment(sketch, "E24.41.2", {"start": v(-21.07, -42.92) * mm, "end": v(-20.55, -41.25) * mm});
            skPoint(sketch, "E24.41.3", {"position": v(-21.34, -40.48) * mm});
            skPoint(sketch, "E24.41.4", {"position": v(-21.11, -43.06) * mm});
            skLineSegment(sketch, "E24.41.5", {"start": v(-20.8, -43.3) * mm, "end": v(-21, -43.14) * mm});
            skLineSegment(sketch, "E24.41.6", {"start": v(-20.62, -41.04) * mm, "end": v(-21.23, -40.56) * mm});
            skPoint(sketch, "E24.41.7", {"position": v(-23.08, -41.5) * mm});
            skLineSegment(sketch, "E24.41.8", {"start": v(-21, -43.14) * mm, "end": v(-23.2, -41.4) * mm});
            skLineSegment(sketch, "E24.41.9", {"start": v(-21.46, -40.54) * mm, "end": v(-22.96, -41.42) * mm});
            skArc(sketch, "E24.41.10", {"start": v(-20.55, -41.25) * mm, "mid": v(-20.55, -41.13) * mm, "end": v(-20.62, -41.04) * mm});
            skArc(sketch, "E24.41.11", {"start": v(-21.23, -40.56) * mm, "mid": v(-21.34, -40.52) * mm, "end": v(-21.46, -40.54) * mm});
            skArc(sketch, "E24.41.12", {"start": v(-23.2, -41.4) * mm, "mid": v(-23.08, -41.45) * mm, "end": v(-22.96, -41.42) * mm});
            skArc(sketch, "E24.41.13", {"start": v(-21.07, -42.92) * mm, "mid": v(-21.07, -43.04) * mm, "end": v(-21, -43.14) * mm});
            skLineSegment(sketch, "E24.42.0", {"start": v(-20.8, -43.28) * mm, "end": v(-20.6, -43.44) * mm});
            skPoint(sketch, "E24.42.1", {"position": v(-17.94, -43) * mm});
            skLineSegment(sketch, "E24.42.2", {"start": v(-18.4, -44.83) * mm, "end": v(-17.98, -43.13) * mm});
            skPoint(sketch, "E24.42.3", {"position": v(-18.81, -42.4) * mm});
            skPoint(sketch, "E24.42.4", {"position": v(-18.43, -44.96) * mm});
            skLineSegment(sketch, "E24.42.5", {"start": v(-18.1, -45.18) * mm, "end": v(-18.3, -45.04) * mm});
            skLineSegment(sketch, "E24.42.6", {"start": v(-18.06, -42.92) * mm, "end": v(-18.7, -42.48) * mm});
            skPoint(sketch, "E24.42.7", {"position": v(-20.49, -43.52) * mm});
            skLineSegment(sketch, "E24.42.8", {"start": v(-18.3, -45.04) * mm, "end": v(-20.6, -43.44) * mm});
            skLineSegment(sketch, "E24.42.9", {"start": v(-18.92, -42.48) * mm, "end": v(-20.37, -43.44) * mm});
            skArc(sketch, "E24.42.10", {"start": v(-17.98, -43.13) * mm, "mid": v(-17.98, -43.01) * mm, "end": v(-18.06, -42.92) * mm});
            skArc(sketch, "E24.42.11", {"start": v(-18.7, -42.48) * mm, "mid": v(-18.81, -42.44) * mm, "end": v(-18.92, -42.48) * mm});
            skArc(sketch, "E24.42.12", {"start": v(-20.6, -43.44) * mm, "mid": v(-20.49, -43.48) * mm, "end": v(-20.37, -43.44) * mm});
            skArc(sketch, "E24.42.13", {"start": v(-18.4, -44.83) * mm, "mid": v(-18.38, -44.95) * mm, "end": v(-18.3, -45.04) * mm});
            skLineSegment(sketch, "E24.43.0", {"start": v(-18.11, -45.17) * mm, "end": v(-17.9, -45.31) * mm});
            skPoint(sketch, "E24.43.1", {"position": v(-15.27, -44.7) * mm});
            skLineSegment(sketch, "E24.43.2", {"start": v(-15.6, -46.56) * mm, "end": v(-15.3, -44.85) * mm});
            skPoint(sketch, "E24.43.3", {"position": v(-16.17, -44.17) * mm});
            skPoint(sketch, "E24.43.4", {"position": v(-15.63, -46.7) * mm});
            skLineSegment(sketch, "E24.43.5", {"start": v(-15.28, -46.9) * mm, "end": v(-15.5, -46.77) * mm});
            skLineSegment(sketch, "E24.43.6", {"start": v(-15.39, -44.64) * mm, "end": v(-16.05, -44.24) * mm});
            skPoint(sketch, "E24.43.7", {"position": v(-17.78, -45.39) * mm});
            skLineSegment(sketch, "E24.43.8", {"start": v(-15.5, -46.77) * mm, "end": v(-17.9, -45.31) * mm});
            skLineSegment(sketch, "E24.43.9", {"start": v(-16.28, -44.25) * mm, "end": v(-17.66, -45.3) * mm});
            skArc(sketch, "E24.43.10", {"start": v(-15.3, -44.85) * mm, "mid": v(-15.3, -44.73) * mm, "end": v(-15.39, -44.64) * mm});
            skArc(sketch, "E24.43.11", {"start": v(-16.05, -44.24) * mm, "mid": v(-16.17, -44.21) * mm, "end": v(-16.28, -44.25) * mm});
            skArc(sketch, "E24.43.12", {"start": v(-17.9, -45.31) * mm, "mid": v(-17.78, -45.34) * mm, "end": v(-17.66, -45.3) * mm});
            skArc(sketch, "E24.43.13", {"start": v(-15.6, -46.56) * mm, "mid": v(-15.59, -46.68) * mm, "end": v(-15.5, -46.77) * mm});
            skLineSegment(sketch, "E24.44.0", {"start": v(-15.3, -46.9) * mm, "end": v(-15.08, -47.02) * mm});
            skPoint(sketch, "E24.44.1", {"position": v(-12.5, -46.26) * mm});
            skLineSegment(sketch, "E24.44.2", {"start": v(-12.71, -48.13) * mm, "end": v(-12.5, -46.4) * mm});
            skPoint(sketch, "E24.44.3", {"position": v(-13.43, -45.77) * mm});
            skPoint(sketch, "E24.44.4", {"position": v(-12.73, -48.27) * mm});
            skLineSegment(sketch, "E24.44.5", {"start": v(-12.37, -48.45) * mm, "end": v(-12.6, -48.33) * mm});
            skLineSegment(sketch, "E24.44.6", {"start": v(-12.62, -46.2) * mm, "end": v(-13.3, -45.84) * mm});
            skPoint(sketch, "E24.44.7", {"position": v(-14.95, -47.09) * mm});
            skLineSegment(sketch, "E24.44.8", {"start": v(-12.6, -48.33) * mm, "end": v(-15.08, -47.02) * mm});
            skLineSegment(sketch, "E24.44.9", {"start": v(-13.53, -45.86) * mm, "end": v(-14.85, -47) * mm});
            skArc(sketch, "E24.44.10", {"start": v(-12.5, -46.4) * mm, "mid": v(-12.53, -46.28) * mm, "end": v(-12.62, -46.2) * mm});
            skArc(sketch, "E24.44.11", {"start": v(-13.3, -45.84) * mm, "mid": v(-13.42, -45.81) * mm, "end": v(-13.53, -45.86) * mm});
            skArc(sketch, "E24.44.12", {"start": v(-15.08, -47.02) * mm, "mid": v(-14.96, -47.04) * mm, "end": v(-14.85, -47) * mm});
            skArc(sketch, "E24.44.13", {"start": v(-12.71, -48.13) * mm, "mid": v(-12.7, -48.25) * mm, "end": v(-12.6, -48.33) * mm});
            skLineSegment(sketch, "E24.45.0", {"start": v(-12.4, -48.44) * mm, "end": v(-12.16, -48.55) * mm});
            skPoint(sketch, "E24.45.1", {"position": v(-9.63, -47.63) * mm});
            skLineSegment(sketch, "E24.45.2", {"start": v(-9.74, -49.51) * mm, "end": v(-9.64, -47.77) * mm});
            skPoint(sketch, "E24.45.3", {"position": v(-10.59, -47.2) * mm});
            skPoint(sketch, "E24.45.4", {"position": v(-9.74, -49.66) * mm});
            skLineSegment(sketch, "E24.45.5", {"start": v(-9.37, -49.81) * mm, "end": v(-9.61, -49.71) * mm});
            skLineSegment(sketch, "E24.45.6", {"start": v(-9.75, -47.58) * mm, "end": v(-10.47, -47.26) * mm});
            skPoint(sketch, "E24.45.7", {"position": v(-12.03, -48.61) * mm});
            skLineSegment(sketch, "E24.45.8", {"start": v(-9.61, -49.71) * mm, "end": v(-12.16, -48.55) * mm});
            skLineSegment(sketch, "E24.45.9", {"start": v(-10.69, -47.3) * mm, "end": v(-11.93, -48.51) * mm});
            skArc(sketch, "E24.45.10", {"start": v(-9.64, -47.77) * mm, "mid": v(-9.66, -47.65) * mm, "end": v(-9.75, -47.58) * mm});
            skArc(sketch, "E24.45.11", {"start": v(-10.47, -47.26) * mm, "mid": v(-10.58, -47.25) * mm, "end": v(-10.69, -47.3) * mm});
            skArc(sketch, "E24.45.12", {"start": v(-12.16, -48.55) * mm, "mid": v(-12.04, -48.57) * mm, "end": v(-11.93, -48.51) * mm});
            skArc(sketch, "E24.45.13", {"start": v(-9.74, -49.51) * mm, "mid": v(-9.7, -49.63) * mm, "end": v(-9.61, -49.71) * mm});
            skLineSegment(sketch, "E24.46.0", {"start": v(-9.4, -49.8) * mm, "end": v(-9.16, -49.9) * mm});
            skPoint(sketch, "E24.46.1", {"position": v(-6.68, -48.83) * mm});
            skLineSegment(sketch, "E24.46.2", {"start": v(-6.68, -50.72) * mm, "end": v(-6.68, -48.97) * mm});
            skPoint(sketch, "E24.46.3", {"position": v(-7.67, -48.46) * mm});
            skPoint(sketch, "E24.46.4", {"position": v(-6.68, -50.86) * mm});
            skLineSegment(sketch, "E24.46.5", {"start": v(-6.3, -50.99) * mm, "end": v(-6.54, -50.9) * mm});
            skLineSegment(sketch, "E24.46.6", {"start": v(-6.81, -48.78) * mm, "end": v(-7.54, -48.51) * mm});
            skPoint(sketch, "E24.46.7", {"position": v(-9.03, -49.96) * mm});
            skLineSegment(sketch, "E24.46.8", {"start": v(-6.54, -50.9) * mm, "end": v(-9.16, -49.9) * mm});
            skLineSegment(sketch, "E24.46.9", {"start": v(-7.76, -48.56) * mm, "end": v(-8.93, -49.85) * mm});
            skArc(sketch, "E24.46.10", {"start": v(-6.68, -48.97) * mm, "mid": v(-6.72, -48.86) * mm, "end": v(-6.81, -48.78) * mm});
            skArc(sketch, "E24.46.11", {"start": v(-7.54, -48.51) * mm, "mid": v(-7.66, -48.5) * mm, "end": v(-7.76, -48.56) * mm});
            skArc(sketch, "E24.46.12", {"start": v(-9.16, -49.9) * mm, "mid": v(-9.04, -49.91) * mm, "end": v(-8.93, -49.85) * mm});
            skArc(sketch, "E24.46.13", {"start": v(-6.68, -50.72) * mm, "mid": v(-6.64, -50.83) * mm, "end": v(-6.54, -50.9) * mm});
            skLineSegment(sketch, "E24.47.0", {"start": v(-6.32, -50.98) * mm, "end": v(-6.08, -51.07) * mm});
            skPoint(sketch, "E24.47.1", {"position": v(-3.67, -49.85) * mm});
            skLineSegment(sketch, "E24.47.2", {"start": v(-3.55, -51.73) * mm, "end": v(-3.67, -49.99) * mm});
            skPoint(sketch, "E24.47.3", {"position": v(-4.68, -49.54) * mm});
            skPoint(sketch, "E24.47.4", {"position": v(-3.54, -51.87) * mm});
            skLineSegment(sketch, "E24.47.5", {"start": v(-3.16, -51.98) * mm, "end": v(-3.4, -51.9) * mm});
            skLineSegment(sketch, "E24.47.6", {"start": v(-3.8, -49.8) * mm, "end": v(-4.55, -49.58) * mm});
            skPoint(sketch, "E24.47.7", {"position": v(-5.94, -51.11) * mm});
            skLineSegment(sketch, "E24.47.8", {"start": v(-3.4, -51.9) * mm, "end": v(-6.08, -51.07) * mm});
            skLineSegment(sketch, "E24.47.9", {"start": v(-4.76, -49.65) * mm, "end": v(-5.86, -51) * mm});
            skArc(sketch, "E24.47.10", {"start": v(-3.67, -49.99) * mm, "mid": v(-3.7, -49.87) * mm, "end": v(-3.8, -49.8) * mm});
            skArc(sketch, "E24.47.11", {"start": v(-4.55, -49.58) * mm, "mid": v(-4.67, -49.58) * mm, "end": v(-4.76, -49.65) * mm});
            skArc(sketch, "E24.47.12", {"start": v(-6.08, -51.07) * mm, "mid": v(-5.96, -51.07) * mm, "end": v(-5.86, -51) * mm});
            skArc(sketch, "E24.47.13", {"start": v(-3.55, -51.73) * mm, "mid": v(-3.5, -51.84) * mm, "end": v(-3.4, -51.9) * mm});
            skLineSegment(sketch, "E24.48.0", {"start": v(-3.18, -51.97) * mm, "end": v(-2.93, -52.04) * mm});
            skPoint(sketch, "E24.48.1", {"position": v(-0.6, -50.68) * mm});
            skLineSegment(sketch, "E24.48.2", {"start": v(-0.37, -52.55) * mm, "end": v(-0.59, -50.82) * mm});
            skPoint(sketch, "E24.48.3", {"position": v(-1.63, -50.43) * mm});
            skPoint(sketch, "E24.48.4", {"position": v(-0.35, -52.69) * mm});
            skLineSegment(sketch, "E24.48.5", {"start": v(0.04, -52.77) * mm, "end": v(-0.21, -52.72) * mm});
            skLineSegment(sketch, "E24.48.6", {"start": v(-0.74, -50.65) * mm, "end": v(-1.5, -50.47) * mm});
            skPoint(sketch, "E24.48.7", {"position": v(-2.8, -52.08) * mm});
            skLineSegment(sketch, "E24.48.8", {"start": v(-0.21, -52.72) * mm, "end": v(-2.93, -52.04) * mm});
            skLineSegment(sketch, "E24.48.9", {"start": v(-1.7, -50.54) * mm, "end": v(-2.71, -51.97) * mm});
            skArc(sketch, "E24.48.10", {"start": v(-0.59, -50.82) * mm, "mid": v(-0.64, -50.7) * mm, "end": v(-0.74, -50.65) * mm});
            skArc(sketch, "E24.48.11", {"start": v(-1.5, -50.47) * mm, "mid": v(-1.61, -50.47) * mm, "end": v(-1.7, -50.54) * mm});
            skArc(sketch, "E24.48.12", {"start": v(-2.93, -52.04) * mm, "mid": v(-2.8, -52.04) * mm, "end": v(-2.71, -51.97) * mm});
            skArc(sketch, "E24.48.13", {"start": v(-0.37, -52.55) * mm, "mid": v(-0.32, -52.66) * mm, "end": v(-0.21, -52.72) * mm});
            skLineSegment(sketch, "E24.49.0", {"start": v(0.02, -52.77) * mm, "end": v(0.27, -52.82) * mm});
            skPoint(sketch, "E24.49.1", {"position": v(2.5, -51.32) * mm});
            skLineSegment(sketch, "E24.49.2", {"start": v(2.86, -53.17) * mm, "end": v(2.53, -51.46) * mm});
            skPoint(sketch, "E24.49.3", {"position": v(1.47, -51.14) * mm});
            skPoint(sketch, "E24.49.4", {"position": v(2.88, -53.31) * mm});
            skLineSegment(sketch, "E24.49.5", {"start": v(3.28, -53.37) * mm, "end": v(3.02, -53.33) * mm});
            skLineSegment(sketch, "E24.49.6", {"start": v(2.37, -51.3) * mm, "end": v(1.6, -51.16) * mm});
            skPoint(sketch, "E24.49.7", {"position": v(0.4, -52.85) * mm});
            skLineSegment(sketch, "E24.49.8", {"start": v(3.02, -53.33) * mm, "end": v(0.27, -52.82) * mm});
            skLineSegment(sketch, "E24.49.9", {"start": v(1.4, -51.25) * mm, "end": v(0.48, -52.73) * mm});
            skArc(sketch, "E24.49.10", {"start": v(2.53, -51.46) * mm, "mid": v(2.47, -51.35) * mm, "end": v(2.37, -51.3) * mm});
            skArc(sketch, "E24.49.11", {"start": v(1.6, -51.16) * mm, "mid": v(1.49, -51.18) * mm, "end": v(1.4, -51.25) * mm});
            skArc(sketch, "E24.49.12", {"start": v(0.27, -52.82) * mm, "mid": v(0.39, -52.81) * mm, "end": v(0.48, -52.73) * mm});
            skArc(sketch, "E24.49.13", {"start": v(2.86, -53.17) * mm, "mid": v(2.91, -53.28) * mm, "end": v(3.02, -53.33) * mm});
            skLineSegment(sketch, "E24.50.0", {"start": v(3.25, -53.37) * mm, "end": v(3.5, -53.4) * mm});
            skPoint(sketch, "E24.50.1", {"position": v(5.65, -51.77) * mm});
            skLineSegment(sketch, "E24.50.2", {"start": v(6.11, -53.6) * mm, "end": v(5.68, -51.9) * mm});
            skPoint(sketch, "E24.50.3", {"position": v(4.6, -51.66) * mm});
            skPoint(sketch, "E24.50.4", {"position": v(6.15, -53.74) * mm});
            skLineSegment(sketch, "E24.50.5", {"start": v(6.55, -53.77) * mm, "end": v(6.29, -53.75) * mm});
            skLineSegment(sketch, "E24.50.6", {"start": v(5.51, -51.76) * mm, "end": v(4.74, -51.67) * mm});
            skPoint(sketch, "E24.50.7", {"position": v(3.65, -53.43) * mm});
            skLineSegment(sketch, "E24.50.8", {"start": v(6.29, -53.75) * mm, "end": v(3.5, -53.4) * mm});
            skLineSegment(sketch, "E24.50.9", {"start": v(4.54, -51.77) * mm, "end": v(3.72, -53.3) * mm});
            skArc(sketch, "E24.50.10", {"start": v(5.68, -51.9) * mm, "mid": v(5.62, -51.8) * mm, "end": v(5.51, -51.76) * mm});
            skArc(sketch, "E24.50.11", {"start": v(4.74, -51.67) * mm, "mid": v(4.63, -51.7) * mm, "end": v(4.54, -51.77) * mm});
            skArc(sketch, "E24.50.12", {"start": v(3.5, -53.4) * mm, "mid": v(3.63, -53.4) * mm, "end": v(3.72, -53.3) * mm});
            skArc(sketch, "E24.50.13", {"start": v(6.11, -53.6) * mm, "mid": v(6.18, -53.7) * mm, "end": v(6.29, -53.75) * mm});
            skLineSegment(sketch, "E24.51.0", {"start": v(6.52, -53.77) * mm, "end": v(6.78, -53.8) * mm});
            skPoint(sketch, "E24.51.1", {"position": v(8.82, -52.03) * mm});
            skLineSegment(sketch, "E24.51.2", {"start": v(9.4, -53.83) * mm, "end": v(8.86, -52.16) * mm});
            skPoint(sketch, "E24.51.3", {"position": v(7.77, -51.98) * mm});
            skPoint(sketch, "E24.51.4", {"position": v(9.43, -53.96) * mm});
            skLineSegment(sketch, "E24.51.5", {"start": v(9.83, -53.97) * mm, "end": v(9.58, -53.97) * mm});
            skLineSegment(sketch, "E24.51.6", {"start": v(8.68, -52.02) * mm, "end": v(7.9, -51.99) * mm});
            skPoint(sketch, "E24.51.7", {"position": v(6.92, -53.8) * mm});
            skLineSegment(sketch, "E24.51.8", {"start": v(9.58, -53.97) * mm, "end": v(6.78, -53.8) * mm});
            skLineSegment(sketch, "E24.51.9", {"start": v(7.71, -52.1) * mm, "end": v(6.98, -53.68) * mm});
            skArc(sketch, "E24.51.10", {"start": v(8.86, -52.16) * mm, "mid": v(8.8, -52.07) * mm, "end": v(8.68, -52.02) * mm});
            skArc(sketch, "E24.51.11", {"start": v(7.9, -51.99) * mm, "mid": v(7.79, -52.01) * mm, "end": v(7.71, -52.1) * mm});
            skArc(sketch, "E24.51.12", {"start": v(6.78, -53.8) * mm, "mid": v(6.9, -53.77) * mm, "end": v(6.98, -53.68) * mm});
            skArc(sketch, "E24.51.13", {"start": v(9.4, -53.83) * mm, "mid": v(9.46, -53.93) * mm, "end": v(9.58, -53.97) * mm});
            skLineSegment(sketch, "E24.52.0", {"start": v(9.81, -53.97) * mm, "end": v(10.07, -53.98) * mm});
            skPoint(sketch, "E24.52.1", {"position": v(12, -52.1) * mm});
            skLineSegment(sketch, "E24.52.2", {"start": v(12.68, -53.86) * mm, "end": v(12.04, -52.23) * mm});
            skPoint(sketch, "E24.52.3", {"position": v(10.94, -52.1) * mm});
            skPoint(sketch, "E24.52.4", {"position": v(12.73, -53.99) * mm});
            skLineSegment(sketch, "E24.52.5", {"start": v(13.13, -53.97) * mm, "end": v(12.87, -53.98) * mm});
            skLineSegment(sketch, "E24.52.6", {"start": v(11.86, -52.1) * mm, "end": v(11.08, -52.1) * mm});
            skPoint(sketch, "E24.52.7", {"position": v(10.21, -53.99) * mm});
            skLineSegment(sketch, "E24.52.8", {"start": v(12.87, -53.98) * mm, "end": v(10.07, -53.98) * mm});
            skLineSegment(sketch, "E24.52.9", {"start": v(10.9, -52.23) * mm, "end": v(10.26, -53.85) * mm});
            skArc(sketch, "E24.52.10", {"start": v(12.04, -52.23) * mm, "mid": v(11.97, -52.13) * mm, "end": v(11.86, -52.1) * mm});
            skArc(sketch, "E24.52.11", {"start": v(11.08, -52.1) * mm, "mid": v(10.97, -52.14) * mm, "end": v(10.9, -52.23) * mm});
            skArc(sketch, "E24.52.12", {"start": v(10.07, -53.98) * mm, "mid": v(10.19, -53.95) * mm, "end": v(10.26, -53.85) * mm});
            skArc(sketch, "E24.52.13", {"start": v(12.68, -53.86) * mm, "mid": v(12.75, -53.95) * mm, "end": v(12.87, -53.98) * mm});
            skLineSegment(sketch, "E24.53.0", {"start": v(13.1, -53.98) * mm, "end": v(13.36, -53.97) * mm});
            skPoint(sketch, "E24.53.1", {"position": v(15.17, -51.97) * mm});
            skLineSegment(sketch, "E24.53.2", {"start": v(15.96, -53.68) * mm, "end": v(15.23, -52.1) * mm});
            skPoint(sketch, "E24.53.3", {"position": v(14.12, -52.04) * mm});
            skPoint(sketch, "E24.53.4", {"position": v(16.02, -53.81) * mm});
            skLineSegment(sketch, "E24.53.5", {"start": v(16.41, -53.77) * mm, "end": v(16.16, -53.8) * mm});
            skLineSegment(sketch, "E24.53.6", {"start": v(15.03, -51.98) * mm, "end": v(14.26, -52.03) * mm});
            skPoint(sketch, "E24.53.7", {"position": v(13.5, -53.96) * mm});
            skLineSegment(sketch, "E24.53.8", {"start": v(16.16, -53.8) * mm, "end": v(13.36, -53.97) * mm});
            skLineSegment(sketch, "E24.53.9", {"start": v(14.08, -52.17) * mm, "end": v(13.55, -53.83) * mm});
            skArc(sketch, "E24.53.10", {"start": v(15.23, -52.1) * mm, "mid": v(15.15, -52) * mm, "end": v(15.03, -51.98) * mm});
            skArc(sketch, "E24.53.11", {"start": v(14.26, -52.03) * mm, "mid": v(14.15, -52.08) * mm, "end": v(14.08, -52.17) * mm});
            skArc(sketch, "E24.53.12", {"start": v(13.36, -53.97) * mm, "mid": v(13.48, -53.93) * mm, "end": v(13.55, -53.83) * mm});
            skArc(sketch, "E24.53.13", {"start": v(15.96, -53.68) * mm, "mid": v(16.04, -53.77) * mm, "end": v(16.16, -53.8) * mm});
            skLineSegment(sketch, "E24.54.0", {"start": v(16.4, -53.78) * mm, "end": v(16.65, -53.75) * mm});
            skPoint(sketch, "E24.54.1", {"position": v(18.33, -51.65) * mm});
            skLineSegment(sketch, "E24.54.2", {"start": v(19.22, -53.3) * mm, "end": v(18.4, -51.77) * mm});
            skPoint(sketch, "E24.54.3", {"position": v(17.29, -51.79) * mm});
            skPoint(sketch, "E24.54.4", {"position": v(19.29, -53.43) * mm});
            skLineSegment(sketch, "E24.54.5", {"start": v(19.68, -53.37) * mm, "end": v(19.43, -53.41) * mm});
            skLineSegment(sketch, "E24.54.6", {"start": v(18.2, -51.67) * mm, "end": v(17.42, -51.77) * mm});
            skPoint(sketch, "E24.54.7", {"position": v(16.79, -53.74) * mm});
            skLineSegment(sketch, "E24.54.8", {"start": v(19.43, -53.41) * mm, "end": v(16.65, -53.75) * mm});
            skLineSegment(sketch, "E24.54.9", {"start": v(17.26, -51.92) * mm, "end": v(16.82, -53.6) * mm});
            skArc(sketch, "E24.54.10", {"start": v(18.4, -51.77) * mm, "mid": v(18.31, -51.69) * mm, "end": v(18.2, -51.67) * mm});
            skArc(sketch, "E24.54.11", {"start": v(17.42, -51.77) * mm, "mid": v(17.32, -51.82) * mm, "end": v(17.26, -51.92) * mm});
            skArc(sketch, "E24.54.12", {"start": v(16.65, -53.75) * mm, "mid": v(16.76, -53.7) * mm, "end": v(16.82, -53.6) * mm});
            skArc(sketch, "E24.54.13", {"start": v(19.22, -53.3) * mm, "mid": v(19.3, -53.4) * mm, "end": v(19.43, -53.41) * mm});
            skLineSegment(sketch, "E24.55.0", {"start": v(19.66, -53.38) * mm, "end": v(19.92, -53.34) * mm});
            skPoint(sketch, "E24.55.1", {"position": v(21.47, -51.13) * mm});
            skLineSegment(sketch, "E24.55.2", {"start": v(22.46, -52.74) * mm, "end": v(21.54, -51.25) * mm});
            skPoint(sketch, "E24.55.3", {"position": v(20.44, -51.34) * mm});
            skPoint(sketch, "E24.55.4", {"position": v(22.53, -52.86) * mm});
            skLineSegment(sketch, "E24.55.5", {"start": v(22.92, -52.77) * mm, "end": v(22.67, -52.83) * mm});
            skLineSegment(sketch, "E24.55.6", {"start": v(21.33, -51.16) * mm, "end": v(20.57, -51.3) * mm});
            skPoint(sketch, "E24.55.7", {"position": v(20.06, -53.32) * mm});
            skLineSegment(sketch, "E24.55.8", {"start": v(22.67, -52.83) * mm, "end": v(19.92, -53.34) * mm});
            skLineSegment(sketch, "E24.55.9", {"start": v(20.4, -51.47) * mm, "end": v(20.08, -53.18) * mm});
            skArc(sketch, "E24.55.10", {"start": v(21.54, -51.25) * mm, "mid": v(21.45, -51.17) * mm, "end": v(21.33, -51.16) * mm});
            skArc(sketch, "E24.55.11", {"start": v(20.57, -51.3) * mm, "mid": v(20.46, -51.36) * mm, "end": v(20.4, -51.47) * mm});
            skArc(sketch, "E24.55.12", {"start": v(19.92, -53.34) * mm, "mid": v(20.02, -53.28) * mm, "end": v(20.08, -53.18) * mm});
            skArc(sketch, "E24.55.13", {"start": v(22.46, -52.74) * mm, "mid": v(22.55, -52.82) * mm, "end": v(22.67, -52.83) * mm});
            skLineSegment(sketch, "E24.56.0", {"start": v(22.9, -52.78) * mm, "end": v(23.15, -52.72) * mm});
            skPoint(sketch, "E24.56.1", {"position": v(24.57, -50.43) * mm});
            skLineSegment(sketch, "E24.56.2", {"start": v(25.65, -51.97) * mm, "end": v(24.65, -50.54) * mm});
            skPoint(sketch, "E24.56.3", {"position": v(23.55, -50.7) * mm});
            skPoint(sketch, "E24.56.4", {"position": v(25.73, -52.09) * mm});
            skLineSegment(sketch, "E24.56.5", {"start": v(26.12, -51.98) * mm, "end": v(25.87, -52.05) * mm});
            skLineSegment(sketch, "E24.56.6", {"start": v(24.43, -50.46) * mm, "end": v(23.68, -50.66) * mm});
            skPoint(sketch, "E24.56.7", {"position": v(23.3, -52.7) * mm});
            skLineSegment(sketch, "E24.56.8", {"start": v(25.87, -52.05) * mm, "end": v(23.15, -52.72) * mm});
            skLineSegment(sketch, "E24.56.9", {"start": v(23.53, -50.83) * mm, "end": v(23.3, -52.55) * mm});
            skArc(sketch, "E24.56.10", {"start": v(24.65, -50.54) * mm, "mid": v(24.55, -50.47) * mm, "end": v(24.43, -50.46) * mm});
            skArc(sketch, "E24.56.11", {"start": v(23.68, -50.66) * mm, "mid": v(23.58, -50.72) * mm, "end": v(23.53, -50.83) * mm});
            skArc(sketch, "E24.56.12", {"start": v(23.15, -52.72) * mm, "mid": v(23.26, -52.66) * mm, "end": v(23.3, -52.55) * mm});
            skArc(sketch, "E24.56.13", {"start": v(25.65, -51.97) * mm, "mid": v(25.75, -52.04) * mm, "end": v(25.87, -52.05) * mm});
            skLineSegment(sketch, "E24.57.0", {"start": v(26.1, -51.98) * mm, "end": v(26.35, -51.91) * mm});
            skPoint(sketch, "E24.57.1", {"position": v(27.62, -49.54) * mm});
            skLineSegment(sketch, "E24.57.2", {"start": v(28.8, -51.01) * mm, "end": v(27.7, -49.65) * mm});
            skPoint(sketch, "E24.57.3", {"position": v(26.62, -49.86) * mm});
            skPoint(sketch, "E24.57.4", {"position": v(28.88, -51.12) * mm});
            skLineSegment(sketch, "E24.57.5", {"start": v(29.26, -50.99) * mm, "end": v(29.02, -51.07) * mm});
            skLineSegment(sketch, "E24.57.6", {"start": v(27.48, -49.58) * mm, "end": v(26.74, -49.82) * mm});
            skPoint(sketch, "E24.57.7", {"position": v(26.48, -51.88) * mm});
            skLineSegment(sketch, "E24.57.8", {"start": v(29.02, -51.07) * mm, "end": v(26.35, -51.91) * mm});
            skLineSegment(sketch, "E24.57.9", {"start": v(26.6, -50) * mm, "end": v(26.5, -51.74) * mm});
            skArc(sketch, "E24.57.10", {"start": v(27.7, -49.65) * mm, "mid": v(27.6, -49.58) * mm, "end": v(27.48, -49.58) * mm});
            skArc(sketch, "E24.57.11", {"start": v(26.74, -49.82) * mm, "mid": v(26.65, -49.89) * mm, "end": v(26.6, -50) * mm});
            skArc(sketch, "E24.57.12", {"start": v(26.35, -51.91) * mm, "mid": v(26.45, -51.85) * mm, "end": v(26.5, -51.74) * mm});
            skArc(sketch, "E24.57.13", {"start": v(28.8, -51.01) * mm, "mid": v(28.9, -51.08) * mm, "end": v(29.02, -51.07) * mm});
            skLineSegment(sketch, "E24.58.0", {"start": v(29.24, -51) * mm, "end": v(29.48, -50.91) * mm});
            skPoint(sketch, "E24.58.1", {"position": v(30.6, -48.46) * mm});
            skLineSegment(sketch, "E24.58.2", {"start": v(31.87, -49.86) * mm, "end": v(30.7, -48.57) * mm});
            skPoint(sketch, "E24.58.3", {"position": v(29.63, -48.85) * mm});
            skPoint(sketch, "E24.58.4", {"position": v(31.97, -49.96) * mm});
            skLineSegment(sketch, "E24.58.5", {"start": v(32.34, -49.81) * mm, "end": v(32.1, -49.91) * mm});
            skLineSegment(sketch, "E24.58.6", {"start": v(30.48, -48.51) * mm, "end": v(29.75, -48.8) * mm});
            skPoint(sketch, "E24.58.7", {"position": v(29.62, -50.87) * mm});
            skLineSegment(sketch, "E24.58.8", {"start": v(32.1, -49.91) * mm, "end": v(29.48, -50.91) * mm});
            skLineSegment(sketch, "E24.58.9", {"start": v(29.63, -48.98) * mm, "end": v(29.62, -50.72) * mm});
            skArc(sketch, "E24.58.10", {"start": v(30.7, -48.57) * mm, "mid": v(30.6, -48.5) * mm, "end": v(30.48, -48.51) * mm});
            skArc(sketch, "E24.58.11", {"start": v(29.75, -48.8) * mm, "mid": v(29.66, -48.87) * mm, "end": v(29.63, -48.98) * mm});
            skArc(sketch, "E24.58.12", {"start": v(29.48, -50.91) * mm, "mid": v(29.58, -50.84) * mm, "end": v(29.62, -50.72) * mm});
            skArc(sketch, "E24.58.13", {"start": v(31.87, -49.86) * mm, "mid": v(31.98, -49.92) * mm, "end": v(32.1, -49.91) * mm});
            skLineSegment(sketch, "E24.59.0", {"start": v(32.31, -49.82) * mm, "end": v(32.55, -49.72) * mm});
            skPoint(sketch, "E24.59.1", {"position": v(33.52, -47.2) * mm});
            skLineSegment(sketch, "E24.59.2", {"start": v(34.87, -48.52) * mm, "end": v(33.62, -47.3) * mm});
            skPoint(sketch, "E24.59.3", {"position": v(32.57, -47.65) * mm});
            skPoint(sketch, "E24.59.4", {"position": v(34.97, -48.62) * mm});
            skLineSegment(sketch, "E24.59.5", {"start": v(35.33, -48.45) * mm, "end": v(35.1, -48.56) * mm});
            skLineSegment(sketch, "E24.59.6", {"start": v(33.4, -47.27) * mm, "end": v(32.7, -47.6) * mm});
            skPoint(sketch, "E24.59.7", {"position": v(32.68, -49.67) * mm});
            skLineSegment(sketch, "E24.59.8", {"start": v(35.1, -48.56) * mm, "end": v(32.55, -49.72) * mm});
            skLineSegment(sketch, "E24.59.9", {"start": v(32.58, -47.79) * mm, "end": v(32.68, -49.52) * mm});
            skArc(sketch, "E24.59.10", {"start": v(33.62, -47.3) * mm, "mid": v(33.52, -47.25) * mm, "end": v(33.4, -47.27) * mm});
            skArc(sketch, "E24.59.11", {"start": v(32.7, -47.6) * mm, "mid": v(32.6, -47.67) * mm, "end": v(32.58, -47.79) * mm});
            skArc(sketch, "E24.59.12", {"start": v(32.55, -49.72) * mm, "mid": v(32.64, -49.64) * mm, "end": v(32.68, -49.52) * mm});
            skArc(sketch, "E24.59.13", {"start": v(34.87, -48.52) * mm, "mid": v(34.98, -48.58) * mm, "end": v(35.1, -48.56) * mm});
            skLineSegment(sketch, "E24.60.0", {"start": v(35.31, -48.46) * mm, "end": v(35.54, -48.34) * mm});
            skPoint(sketch, "E24.60.1", {"position": v(36.36, -45.77) * mm});
            skLineSegment(sketch, "E24.60.2", {"start": v(37.79, -47) * mm, "end": v(36.47, -45.87) * mm});
            skPoint(sketch, "E24.60.3", {"position": v(35.44, -46.28) * mm});
            skPoint(sketch, "E24.60.4", {"position": v(37.9, -47.1) * mm});
            skLineSegment(sketch, "E24.60.5", {"start": v(38.24, -46.9) * mm, "end": v(38.02, -47.03) * mm});
            skLineSegment(sketch, "E24.60.6", {"start": v(36.24, -45.84) * mm, "end": v(35.56, -46.21) * mm});
            skPoint(sketch, "E24.60.7", {"position": v(35.67, -48.28) * mm});
            skLineSegment(sketch, "E24.60.8", {"start": v(38.02, -47.03) * mm, "end": v(35.54, -48.34) * mm});
            skLineSegment(sketch, "E24.60.9", {"start": v(35.45, -46.41) * mm, "end": v(35.65, -48.14) * mm});
            skArc(sketch, "E24.60.10", {"start": v(36.47, -45.87) * mm, "mid": v(36.36, -45.82) * mm, "end": v(36.24, -45.84) * mm});
            skArc(sketch, "E24.60.11", {"start": v(35.56, -46.21) * mm, "mid": v(35.47, -46.3) * mm, "end": v(35.45, -46.41) * mm});
            skArc(sketch, "E24.60.12", {"start": v(35.54, -48.34) * mm, "mid": v(35.63, -48.26) * mm, "end": v(35.65, -48.14) * mm});
            skArc(sketch, "E24.60.13", {"start": v(37.79, -47) * mm, "mid": v(37.9, -47.06) * mm, "end": v(38.02, -47.03) * mm});
            skLineSegment(sketch, "E24.61.0", {"start": v(38.22, -46.91) * mm, "end": v(38.45, -46.79) * mm});
            skPoint(sketch, "E24.61.1", {"position": v(39.1, -44.17) * mm});
            skLineSegment(sketch, "E24.61.2", {"start": v(40.6, -45.32) * mm, "end": v(39.22, -44.26) * mm});
            skPoint(sketch, "E24.61.3", {"position": v(38.21, -44.73) * mm});
            skPoint(sketch, "E24.61.4", {"position": v(40.72, -45.4) * mm});
            skLineSegment(sketch, "E24.61.5", {"start": v(41.05, -45.18) * mm, "end": v(40.84, -45.32) * mm});
            skLineSegment(sketch, "E24.61.6", {"start": v(38.99, -44.25) * mm, "end": v(38.33, -44.66) * mm});
            skPoint(sketch, "E24.61.7", {"position": v(38.57, -46.72) * mm});
            skLineSegment(sketch, "E24.61.8", {"start": v(40.84, -45.32) * mm, "end": v(38.45, -46.79) * mm});
            skLineSegment(sketch, "E24.61.9", {"start": v(38.24, -44.86) * mm, "end": v(38.54, -46.58) * mm});
            skArc(sketch, "E24.61.10", {"start": v(39.22, -44.26) * mm, "mid": v(39.1, -44.22) * mm, "end": v(38.99, -44.25) * mm});
            skArc(sketch, "E24.61.11", {"start": v(38.33, -44.66) * mm, "mid": v(38.25, -44.75) * mm, "end": v(38.24, -44.86) * mm});
            skArc(sketch, "E24.61.12", {"start": v(38.45, -46.79) * mm, "mid": v(38.53, -46.7) * mm, "end": v(38.54, -46.58) * mm});
            skArc(sketch, "E24.61.13", {"start": v(40.6, -45.32) * mm, "mid": v(40.72, -45.36) * mm, "end": v(40.84, -45.32) * mm});
            skLineSegment(sketch, "E24.62.0", {"start": v(41.03, -45.2) * mm, "end": v(41.25, -45.05) * mm});
            skPoint(sketch, "E24.62.1", {"position": v(41.75, -42.4) * mm});
            skLineSegment(sketch, "E24.62.2", {"start": v(43.31, -43.46) * mm, "end": v(41.86, -42.48) * mm});
            skPoint(sketch, "E24.62.3", {"position": v(40.9, -43.02) * mm});
            skPoint(sketch, "E24.62.4", {"position": v(43.43, -43.54) * mm});
            skLineSegment(sketch, "E24.62.5", {"start": v(43.75, -43.3) * mm, "end": v(43.54, -43.45) * mm});
            skLineSegment(sketch, "E24.62.6", {"start": v(41.63, -42.49) * mm, "end": v(41, -42.94) * mm});
            skPoint(sketch, "E24.62.7", {"position": v(41.37, -44.98) * mm});
            skLineSegment(sketch, "E24.62.8", {"start": v(43.54, -43.45) * mm, "end": v(41.25, -45.05) * mm});
            skLineSegment(sketch, "E24.62.9", {"start": v(40.92, -43.15) * mm, "end": v(41.33, -44.84) * mm});
            skArc(sketch, "E24.62.10", {"start": v(41.86, -42.48) * mm, "mid": v(41.75, -42.45) * mm, "end": v(41.63, -42.49) * mm});
            skArc(sketch, "E24.62.11", {"start": v(41, -42.94) * mm, "mid": v(40.93, -43.03) * mm, "end": v(40.92, -43.15) * mm});
            skArc(sketch, "E24.62.12", {"start": v(41.25, -45.05) * mm, "mid": v(41.33, -44.96) * mm, "end": v(41.33, -44.84) * mm});
            skArc(sketch, "E24.62.13", {"start": v(43.31, -43.46) * mm, "mid": v(43.43, -43.5) * mm, "end": v(43.54, -43.45) * mm});
            skLineSegment(sketch, "E24.63.0", {"start": v(43.73, -43.31) * mm, "end": v(43.94, -43.16) * mm});
            skPoint(sketch, "E24.63.1", {"position": v(44.28, -40.48) * mm});
            skLineSegment(sketch, "E24.63.2", {"start": v(45.9, -41.44) * mm, "end": v(44.4, -40.55) * mm});
            skPoint(sketch, "E24.63.3", {"position": v(43.46, -41.14) * mm});
            skPoint(sketch, "E24.63.4", {"position": v(46.03, -41.5) * mm});
            skLineSegment(sketch, "E24.63.5", {"start": v(46.33, -41.25) * mm, "end": v(46.13, -41.42) * mm});
            skLineSegment(sketch, "E24.63.6", {"start": v(44.17, -40.57) * mm, "end": v(43.56, -41.06) * mm});
            skPoint(sketch, "E24.63.7", {"position": v(44.05, -43.07) * mm});
            skLineSegment(sketch, "E24.63.8", {"start": v(46.13, -41.42) * mm, "end": v(43.94, -43.16) * mm});
            skLineSegment(sketch, "E24.63.9", {"start": v(43.5, -41.27) * mm, "end": v(44.01, -42.94) * mm});
            skArc(sketch, "E24.63.10", {"start": v(44.4, -40.55) * mm, "mid": v(44.28, -40.53) * mm, "end": v(44.17, -40.57) * mm});
            skArc(sketch, "E24.63.11", {"start": v(43.56, -41.06) * mm, "mid": v(43.5, -41.16) * mm, "end": v(43.5, -41.27) * mm});
            skArc(sketch, "E24.63.12", {"start": v(43.94, -43.16) * mm, "mid": v(44.01, -43.06) * mm, "end": v(44.01, -42.94) * mm});
            skArc(sketch, "E24.63.13", {"start": v(45.9, -41.44) * mm, "mid": v(46.02, -41.46) * mm, "end": v(46.13, -41.42) * mm});
            skLineSegment(sketch, "E24.64.0", {"start": v(46.31, -41.26) * mm, "end": v(46.51, -41.1) * mm});
            skPoint(sketch, "E24.64.1", {"position": v(46.68, -38.4) * mm});
            skLineSegment(sketch, "E24.64.2", {"start": v(48.37, -39.26) * mm, "end": v(46.8, -38.47) * mm});
            skPoint(sketch, "E24.64.3", {"position": v(45.9, -39.12) * mm});
            skPoint(sketch, "E24.64.4", {"position": v(48.5, -39.32) * mm});
            skLineSegment(sketch, "E24.64.5", {"start": v(48.78, -39.05) * mm, "end": v(48.6, -39.23) * mm});
            skLineSegment(sketch, "E24.64.6", {"start": v(46.58, -38.5) * mm, "end": v(46, -39.03) * mm});
            skPoint(sketch, "E24.64.7", {"position": v(46.62, -41) * mm});
            skLineSegment(sketch, "E24.64.8", {"start": v(48.6, -39.23) * mm, "end": v(46.51, -41.1) * mm});
            skLineSegment(sketch, "E24.64.9", {"start": v(45.96, -39.24) * mm, "end": v(46.57, -40.87) * mm});
            skArc(sketch, "E24.64.10", {"start": v(46.8, -38.47) * mm, "mid": v(46.69, -38.45) * mm, "end": v(46.58, -38.5) * mm});
            skArc(sketch, "E24.64.11", {"start": v(46, -39.03) * mm, "mid": v(45.95, -39.13) * mm, "end": v(45.96, -39.24) * mm});
            skArc(sketch, "E24.64.12", {"start": v(46.51, -41.1) * mm, "mid": v(46.58, -41) * mm, "end": v(46.57, -40.87) * mm});
            skArc(sketch, "E24.64.13", {"start": v(48.37, -39.26) * mm, "mid": v(48.49, -39.28) * mm, "end": v(48.6, -39.23) * mm});
            skLineSegment(sketch, "E24.65.0", {"start": v(48.76, -39.06) * mm, "end": v(48.95, -38.88) * mm});
            skPoint(sketch, "E24.65.1", {"position": v(48.96, -36.2) * mm});
            skLineSegment(sketch, "E24.65.2", {"start": v(50.7, -36.94) * mm, "end": v(49.09, -36.25) * mm});
            skPoint(sketch, "E24.65.3", {"position": v(48.23, -36.95) * mm});
            skPoint(sketch, "E24.65.4", {"position": v(50.82, -37) * mm});
            skLineSegment(sketch, "E24.65.5", {"start": v(51.1, -36.7) * mm, "end": v(50.92, -36.9) * mm});
            skLineSegment(sketch, "E24.65.6", {"start": v(48.86, -36.29) * mm, "end": v(48.32, -36.85) * mm});
            skPoint(sketch, "E24.65.7", {"position": v(49.05, -38.79) * mm});
            skLineSegment(sketch, "E24.65.8", {"start": v(50.92, -36.9) * mm, "end": v(48.95, -38.88) * mm});
            skLineSegment(sketch, "E24.65.9", {"start": v(48.28, -37.07) * mm, "end": v(49, -38.66) * mm});
            skArc(sketch, "E24.65.10", {"start": v(49.09, -36.25) * mm, "mid": v(48.97, -36.23) * mm, "end": v(48.86, -36.29) * mm});
            skArc(sketch, "E24.65.11", {"start": v(48.32, -36.85) * mm, "mid": v(48.27, -36.95) * mm, "end": v(48.28, -37.07) * mm});
            skArc(sketch, "E24.65.12", {"start": v(48.95, -38.88) * mm, "mid": v(49, -38.78) * mm, "end": v(49, -38.66) * mm});
            skArc(sketch, "E24.65.13", {"start": v(50.7, -36.94) * mm, "mid": v(50.81, -36.95) * mm, "end": v(50.92, -36.9) * mm});
            skLineSegment(sketch, "E24.66.0", {"start": v(51.08, -36.72) * mm, "end": v(51.25, -36.53) * mm});
            skPoint(sketch, "E24.66.1", {"position": v(51.1, -33.84) * mm});
            skLineSegment(sketch, "E24.66.2", {"start": v(52.87, -34.48) * mm, "end": v(51.23, -33.89) * mm});
            skPoint(sketch, "E24.66.3", {"position": v(50.41, -34.64) * mm});
            skPoint(sketch, "E24.66.4", {"position": v(53, -34.53) * mm});
            skLineSegment(sketch, "E24.66.5", {"start": v(53.26, -34.22) * mm, "end": v(53.1, -34.42) * mm});
            skLineSegment(sketch, "E24.66.6", {"start": v(51, -33.94) * mm, "end": v(50.5, -34.53) * mm});
            skPoint(sketch, "E24.66.7", {"position": v(51.35, -36.42) * mm});
            skLineSegment(sketch, "E24.66.8", {"start": v(53.1, -34.42) * mm, "end": v(51.25, -36.53) * mm});
            skLineSegment(sketch, "E24.66.9", {"start": v(50.48, -34.76) * mm, "end": v(51.28, -36.3) * mm});
            skArc(sketch, "E24.66.10", {"start": v(51.23, -33.89) * mm, "mid": v(51.1, -33.88) * mm, "end": v(51, -33.94) * mm});
            skArc(sketch, "E24.66.11", {"start": v(50.5, -34.53) * mm, "mid": v(50.45, -34.64) * mm, "end": v(50.48, -34.76) * mm});
            skArc(sketch, "E24.66.12", {"start": v(51.25, -36.53) * mm, "mid": v(51.3, -36.42) * mm, "end": v(51.28, -36.3) * mm});
            skArc(sketch, "E24.66.13", {"start": v(52.87, -34.48) * mm, "mid": v(53, -34.48) * mm, "end": v(53.1, -34.42) * mm});
            skLineSegment(sketch, "E24.67.0", {"start": v(53.24, -34.24) * mm, "end": v(53.4, -34.04) * mm});
            skPoint(sketch, "E24.67.1", {"position": v(53.09, -31.36) * mm});
            skLineSegment(sketch, "E24.67.2", {"start": v(54.9, -31.9) * mm, "end": v(53.22, -31.4) * mm});
            skPoint(sketch, "E24.67.3", {"position": v(52.45, -32.2) * mm});
            skPoint(sketch, "E24.67.4", {"position": v(55.03, -31.93) * mm});
            skLineSegment(sketch, "E24.67.5", {"start": v(55.26, -31.6) * mm, "end": v(55.11, -31.82) * mm});
            skLineSegment(sketch, "E24.67.6", {"start": v(53, -31.47) * mm, "end": v(52.53, -32.1) * mm});
            skPoint(sketch, "E24.67.7", {"position": v(53.5, -33.93) * mm});
            skLineSegment(sketch, "E24.67.8", {"start": v(55.11, -31.82) * mm, "end": v(53.4, -34.04) * mm});
            skLineSegment(sketch, "E24.67.9", {"start": v(52.52, -32.32) * mm, "end": v(53.42, -33.8) * mm});
            skArc(sketch, "E24.67.10", {"start": v(53.22, -31.4) * mm, "mid": v(53.1, -31.4) * mm, "end": v(53, -31.47) * mm});
            skArc(sketch, "E24.67.11", {"start": v(52.53, -32.1) * mm, "mid": v(52.5, -32.2) * mm, "end": v(52.52, -32.32) * mm});
            skArc(sketch, "E24.67.12", {"start": v(53.4, -34.04) * mm, "mid": v(53.45, -33.92) * mm, "end": v(53.42, -33.8) * mm});
            skArc(sketch, "E24.67.13", {"start": v(54.9, -31.9) * mm, "mid": v(55.02, -31.89) * mm, "end": v(55.11, -31.82) * mm});
            skLineSegment(sketch, "E24.68.0", {"start": v(55.25, -31.63) * mm, "end": v(55.4, -31.42) * mm});
            skPoint(sketch, "E24.68.1", {"position": v(54.92, -28.77) * mm});
            skLineSegment(sketch, "E24.68.2", {"start": v(56.76, -29.19) * mm, "end": v(55.05, -28.8) * mm});
            skPoint(sketch, "E24.68.3", {"position": v(54.34, -29.64) * mm});
            skPoint(sketch, "E24.68.4", {"position": v(56.9, -29.22) * mm});
            skLineSegment(sketch, "E24.68.5", {"start": v(57.1, -28.88) * mm, "end": v(56.97, -29.1) * mm});
            skLineSegment(sketch, "E24.68.6", {"start": v(54.84, -28.88) * mm, "end": v(54.41, -29.53) * mm});
            skPoint(sketch, "E24.68.7", {"position": v(55.48, -31.3) * mm});
            skLineSegment(sketch, "E24.68.8", {"start": v(56.97, -29.1) * mm, "end": v(55.4, -31.42) * mm});
            skLineSegment(sketch, "E24.68.9", {"start": v(54.42, -29.75) * mm, "end": v(55.4, -31.19) * mm});
            skArc(sketch, "E24.68.10", {"start": v(55.05, -28.8) * mm, "mid": v(54.94, -28.8) * mm, "end": v(54.84, -28.88) * mm});
            skArc(sketch, "E24.68.11", {"start": v(54.41, -29.53) * mm, "mid": v(54.38, -29.64) * mm, "end": v(54.42, -29.75) * mm});
            skArc(sketch, "E24.68.12", {"start": v(55.4, -31.42) * mm, "mid": v(55.44, -31.3) * mm, "end": v(55.4, -31.19) * mm});
            skArc(sketch, "E24.68.13", {"start": v(56.76, -29.19) * mm, "mid": v(56.88, -29.18) * mm, "end": v(56.97, -29.1) * mm});
            skLineSegment(sketch, "E24.69.0", {"start": v(57.1, -28.9) * mm, "end": v(57.24, -28.68) * mm});
            skPoint(sketch, "E24.69.1", {"position": v(56.6, -26.06) * mm});
            skLineSegment(sketch, "E24.69.2", {"start": v(58.45, -26.37) * mm, "end": v(56.73, -26.09) * mm});
            skPoint(sketch, "E24.69.3", {"position": v(56.07, -26.97) * mm});
            skPoint(sketch, "E24.69.4", {"position": v(58.6, -26.4) * mm});
            skLineSegment(sketch, "E24.69.5", {"start": v(58.79, -26.04) * mm, "end": v(58.66, -26.27) * mm});
            skLineSegment(sketch, "E24.69.6", {"start": v(56.52, -26.18) * mm, "end": v(56.13, -26.86) * mm});
            skPoint(sketch, "E24.69.7", {"position": v(57.31, -28.56) * mm});
            skLineSegment(sketch, "E24.69.8", {"start": v(58.66, -26.27) * mm, "end": v(57.24, -28.68) * mm});
            skLineSegment(sketch, "E24.69.9", {"start": v(56.15, -27.08) * mm, "end": v(57.22, -28.45) * mm});
            skArc(sketch, "E24.69.10", {"start": v(56.73, -26.09) * mm, "mid": v(56.61, -26.1) * mm, "end": v(56.52, -26.18) * mm});
            skArc(sketch, "E24.69.11", {"start": v(56.13, -26.86) * mm, "mid": v(56.1, -26.97) * mm, "end": v(56.15, -27.08) * mm});
            skArc(sketch, "E24.69.12", {"start": v(57.24, -28.68) * mm, "mid": v(57.27, -28.56) * mm, "end": v(57.22, -28.45) * mm});
            skArc(sketch, "E24.69.13", {"start": v(58.45, -26.37) * mm, "mid": v(58.57, -26.35) * mm, "end": v(58.66, -26.27) * mm});
            skLineSegment(sketch, "E24.70.0", {"start": v(58.77, -26.06) * mm, "end": v(58.9, -25.84) * mm});
            skPoint(sketch, "E24.70.1", {"position": v(58.1, -23.26) * mm});
            skLineSegment(sketch, "E24.70.2", {"start": v(59.97, -23.46) * mm, "end": v(58.24, -23.28) * mm});
            skPoint(sketch, "E24.70.3", {"position": v(57.63, -24.2) * mm});
            skPoint(sketch, "E24.70.4", {"position": v(60.11, -23.47) * mm});
            skLineSegment(sketch, "E24.70.5", {"start": v(60.28, -23.11) * mm, "end": v(60.17, -23.34) * mm});
            skLineSegment(sketch, "E24.70.6", {"start": v(58.04, -23.39) * mm, "end": v(57.69, -24.08) * mm});
            skPoint(sketch, "E24.70.7", {"position": v(58.97, -25.71) * mm});
            skLineSegment(sketch, "E24.70.8", {"start": v(60.17, -23.34) * mm, "end": v(58.9, -25.84) * mm});
            skLineSegment(sketch, "E24.70.9", {"start": v(57.72, -24.3) * mm, "end": v(58.87, -25.6) * mm});
            skArc(sketch, "E24.70.10", {"start": v(58.24, -23.28) * mm, "mid": v(58.12, -23.3) * mm, "end": v(58.04, -23.39) * mm});
            skArc(sketch, "E24.70.11", {"start": v(57.69, -24.08) * mm, "mid": v(57.67, -24.2) * mm, "end": v(57.72, -24.3) * mm});
            skArc(sketch, "E24.70.12", {"start": v(58.9, -25.84) * mm, "mid": v(58.92, -25.72) * mm, "end": v(58.87, -25.6) * mm});
            skArc(sketch, "E24.70.13", {"start": v(59.97, -23.46) * mm, "mid": v(60.1, -23.43) * mm, "end": v(60.17, -23.34) * mm});
            skLineSegment(sketch, "E24.71.0", {"start": v(60.27, -23.13) * mm, "end": v(60.39, -22.9) * mm});
            skPoint(sketch, "E24.71.1", {"position": v(59.43, -20.38) * mm});
            skLineSegment(sketch, "E24.71.2", {"start": v(61.31, -20.46) * mm, "end": v(59.57, -20.39) * mm});
            skPoint(sketch, "E24.71.3", {"position": v(59.02, -21.35) * mm});
            skPoint(sketch, "E24.71.4", {"position": v(61.45, -20.46) * mm});
            skLineSegment(sketch, "E24.71.5", {"start": v(61.6, -20.1) * mm, "end": v(61.5, -20.33) * mm});
            skLineSegment(sketch, "E24.71.6", {"start": v(59.38, -20.5) * mm, "end": v(59.07, -21.22) * mm});
            skPoint(sketch, "E24.71.7", {"position": v(60.45, -22.77) * mm});
            skLineSegment(sketch, "E24.71.8", {"start": v(61.5, -20.33) * mm, "end": v(60.39, -22.9) * mm});
            skLineSegment(sketch, "E24.71.9", {"start": v(59.11, -21.44) * mm, "end": v(60.35, -22.67) * mm});
            skArc(sketch, "E24.71.10", {"start": v(59.57, -20.39) * mm, "mid": v(59.45, -20.42) * mm, "end": v(59.38, -20.5) * mm});
            skArc(sketch, "E24.71.11", {"start": v(59.07, -21.22) * mm, "mid": v(59.06, -21.34) * mm, "end": v(59.11, -21.44) * mm});
            skArc(sketch, "E24.71.12", {"start": v(60.39, -22.9) * mm, "mid": v(60.4, -22.78) * mm, "end": v(60.35, -22.67) * mm});
            skArc(sketch, "E24.71.13", {"start": v(61.31, -20.46) * mm, "mid": v(61.43, -20.43) * mm, "end": v(61.5, -20.33) * mm});
            skLineSegment(sketch, "E24.72.0", {"start": v(61.6, -20.11) * mm, "end": v(61.7, -19.87) * mm});
            skPoint(sketch, "E24.72.1", {"position": v(60.58, -17.42) * mm});
            skLineSegment(sketch, "E24.72.2", {"start": v(62.47, -17.38) * mm, "end": v(60.72, -17.42) * mm});
            skPoint(sketch, "E24.72.3", {"position": v(60.23, -18.4) * mm});
            skPoint(sketch, "E24.72.4", {"position": v(62.6, -17.38) * mm});
            skLineSegment(sketch, "E24.72.5", {"start": v(62.73, -17) * mm, "end": v(62.65, -17.25) * mm});
            skLineSegment(sketch, "E24.72.6", {"start": v(60.54, -17.55) * mm, "end": v(60.28, -18.28) * mm});
            skPoint(sketch, "E24.72.7", {"position": v(61.74, -19.74) * mm});
            skLineSegment(sketch, "E24.72.8", {"start": v(62.65, -17.25) * mm, "end": v(61.7, -19.87) * mm});
            skLineSegment(sketch, "E24.72.9", {"start": v(60.33, -18.5) * mm, "end": v(61.64, -19.65) * mm});
            skArc(sketch, "E24.72.10", {"start": v(60.72, -17.42) * mm, "mid": v(60.6, -17.45) * mm, "end": v(60.54, -17.55) * mm});
            skArc(sketch, "E24.72.11", {"start": v(60.28, -18.28) * mm, "mid": v(60.27, -18.4) * mm, "end": v(60.33, -18.5) * mm});
            skArc(sketch, "E24.72.12", {"start": v(61.7, -19.87) * mm, "mid": v(61.7, -19.75) * mm, "end": v(61.64, -19.65) * mm});
            skArc(sketch, "E24.72.13", {"start": v(62.47, -17.38) * mm, "mid": v(62.58, -17.34) * mm, "end": v(62.65, -17.25) * mm});
            skLineSegment(sketch, "E24.73.0", {"start": v(62.73, -17.02) * mm, "end": v(62.8, -16.78) * mm});
            skPoint(sketch, "E24.73.1", {"position": v(61.55, -14.4) * mm});
            skLineSegment(sketch, "E24.73.2", {"start": v(63.43, -14.24) * mm, "end": v(61.7, -14.38) * mm});
            skPoint(sketch, "E24.73.3", {"position": v(61.26, -15.4) * mm});
            skPoint(sketch, "E24.73.4", {"position": v(63.57, -14.23) * mm});
            skLineSegment(sketch, "E24.73.5", {"start": v(63.68, -13.84) * mm, "end": v(63.6, -14.1) * mm});
            skLineSegment(sketch, "E24.73.6", {"start": v(61.51, -14.53) * mm, "end": v(61.3, -15.27) * mm});
            skPoint(sketch, "E24.73.7", {"position": v(62.85, -16.64) * mm});
            skLineSegment(sketch, "E24.73.8", {"start": v(63.6, -14.1) * mm, "end": v(62.8, -16.78) * mm});
            skLineSegment(sketch, "E24.73.9", {"start": v(61.37, -15.49) * mm, "end": v(62.74, -16.56) * mm});
            skArc(sketch, "E24.73.10", {"start": v(61.7, -14.38) * mm, "mid": v(61.58, -14.43) * mm, "end": v(61.51, -14.53) * mm});
            skArc(sketch, "E24.73.11", {"start": v(61.3, -15.27) * mm, "mid": v(61.3, -15.4) * mm, "end": v(61.37, -15.49) * mm});
            skArc(sketch, "E24.73.12", {"start": v(62.8, -16.78) * mm, "mid": v(62.81, -16.66) * mm, "end": v(62.74, -16.56) * mm});
            skArc(sketch, "E24.73.13", {"start": v(63.43, -14.24) * mm, "mid": v(63.54, -14.2) * mm, "end": v(63.6, -14.1) * mm});
            skLineSegment(sketch, "E24.74.0", {"start": v(63.67, -13.87) * mm, "end": v(63.74, -13.62) * mm});
            skPoint(sketch, "E24.74.1", {"position": v(62.34, -11.31) * mm});
            skLineSegment(sketch, "E24.74.2", {"start": v(64.2, -11.05) * mm, "end": v(62.47, -11.3) * mm});
            skPoint(sketch, "E24.74.3", {"position": v(62.1, -12.34) * mm});
            skPoint(sketch, "E24.74.4", {"position": v(64.34, -11.03) * mm});
            skLineSegment(sketch, "E24.74.5", {"start": v(64.42, -10.64) * mm, "end": v(64.37, -10.89) * mm});
            skLineSegment(sketch, "E24.74.6", {"start": v(62.3, -11.45) * mm, "end": v(62.14, -12.2) * mm});
            skPoint(sketch, "E24.74.7", {"position": v(63.77, -13.48) * mm});
            skLineSegment(sketch, "E24.74.8", {"start": v(64.37, -10.89) * mm, "end": v(63.74, -13.62) * mm});
            skLineSegment(sketch, "E24.74.9", {"start": v(62.22, -12.42) * mm, "end": v(63.66, -13.4) * mm});
            skArc(sketch, "E24.74.10", {"start": v(62.47, -11.3) * mm, "mid": v(62.37, -11.35) * mm, "end": v(62.3, -11.45) * mm});
            skArc(sketch, "E24.74.11", {"start": v(62.14, -12.2) * mm, "mid": v(62.15, -12.32) * mm, "end": v(62.22, -12.42) * mm});
            skArc(sketch, "E24.74.12", {"start": v(63.74, -13.62) * mm, "mid": v(63.73, -13.5) * mm, "end": v(63.66, -13.4) * mm});
            skArc(sketch, "E24.74.13", {"start": v(64.2, -11.05) * mm, "mid": v(64.31, -11) * mm, "end": v(64.37, -10.89) * mm});
            skLineSegment(sketch, "E24.75.0", {"start": v(64.42, -10.66) * mm, "end": v(64.47, -10.4) * mm});
            skPoint(sketch, "E24.75.1", {"position": v(62.93, -8.2) * mm});
            skLineSegment(sketch, "E24.75.2", {"start": v(64.78, -7.81) * mm, "end": v(63.07, -8.16) * mm});
            skPoint(sketch, "E24.75.3", {"position": v(62.77, -9.23) * mm});
            skPoint(sketch, "E24.75.4", {"position": v(64.92, -7.78) * mm});
            skLineSegment(sketch, "E24.75.5", {"start": v(64.97, -7.39) * mm, "end": v(64.94, -7.64) * mm});
            skLineSegment(sketch, "E24.75.6", {"start": v(62.91, -8.33) * mm, "end": v(62.79, -9.1) * mm});
            skPoint(sketch, "E24.75.7", {"position": v(64.5, -10.27) * mm});
            skLineSegment(sketch, "E24.75.8", {"start": v(64.94, -7.64) * mm, "end": v(64.47, -10.4) * mm});
            skLineSegment(sketch, "E24.75.9", {"start": v(62.88, -9.3) * mm, "end": v(64.38, -10.2) * mm});
            skArc(sketch, "E24.75.10", {"start": v(63.07, -8.16) * mm, "mid": v(62.96, -8.22) * mm, "end": v(62.91, -8.33) * mm});
            skArc(sketch, "E24.75.11", {"start": v(62.79, -9.1) * mm, "mid": v(62.8, -9.21) * mm, "end": v(62.88, -9.3) * mm});
            skArc(sketch, "E24.75.12", {"start": v(64.47, -10.4) * mm, "mid": v(64.46, -10.28) * mm, "end": v(64.38, -10.2) * mm});
            skArc(sketch, "E24.75.13", {"start": v(64.78, -7.81) * mm, "mid": v(64.89, -7.75) * mm, "end": v(64.94, -7.64) * mm});
            skLineSegment(sketch, "E24.76.0", {"start": v(64.97, -7.41) * mm, "end": v(65, -7.16) * mm});
            skPoint(sketch, "E24.76.1", {"position": v(63.34, -5.04) * mm});
            skLineSegment(sketch, "E24.76.2", {"start": v(65.16, -4.55) * mm, "end": v(63.47, -5) * mm});
            skPoint(sketch, "E24.76.3", {"position": v(63.23, -6.09) * mm});
            skPoint(sketch, "E24.76.4", {"position": v(65.3, -4.51) * mm});
            skLineSegment(sketch, "E24.76.5", {"start": v(65.32, -4.11) * mm, "end": v(65.3, -4.37) * mm});
            skLineSegment(sketch, "E24.76.6", {"start": v(63.32, -5.18) * mm, "end": v(63.25, -5.95) * mm});
            skPoint(sketch, "E24.76.7", {"position": v(65.02, -7.02) * mm});
            skLineSegment(sketch, "E24.76.8", {"start": v(65.3, -4.37) * mm, "end": v(65, -7.16) * mm});
            skLineSegment(sketch, "E24.76.9", {"start": v(63.35, -6.15) * mm, "end": v(64.9, -6.95) * mm});
            skArc(sketch, "E24.76.10", {"start": v(63.47, -5) * mm, "mid": v(63.37, -5.07) * mm, "end": v(63.32, -5.18) * mm});
            skArc(sketch, "E24.76.11", {"start": v(63.25, -5.95) * mm, "mid": v(63.27, -6.07) * mm, "end": v(63.35, -6.15) * mm});
            skArc(sketch, "E24.76.12", {"start": v(65, -7.16) * mm, "mid": v(64.98, -7.04) * mm, "end": v(64.9, -6.95) * mm});
            skArc(sketch, "E24.76.13", {"start": v(65.16, -4.55) * mm, "mid": v(65.26, -4.48) * mm, "end": v(65.3, -4.37) * mm});
            skLineSegment(sketch, "E24.77.0", {"start": v(65.32, -4.14) * mm, "end": v(65.34, -3.88) * mm});
            skPoint(sketch, "E24.77.1", {"position": v(63.55, -1.87) * mm});
            skLineSegment(sketch, "E24.77.2", {"start": v(65.33, -1.27) * mm, "end": v(63.68, -1.83) * mm});
            skPoint(sketch, "E24.77.3", {"position": v(63.5, -2.92) * mm});
            skPoint(sketch, "E24.77.4", {"position": v(65.47, -1.22) * mm});
            skLineSegment(sketch, "E24.77.5", {"start": v(65.47, -0.82) * mm, "end": v(65.47, -1.08) * mm});
            skLineSegment(sketch, "E24.77.6", {"start": v(63.54, -2) * mm, "end": v(63.51, -2.78) * mm});
            skPoint(sketch, "E24.77.7", {"position": v(65.35, -3.74) * mm});
            skLineSegment(sketch, "E24.77.8", {"start": v(65.47, -1.08) * mm, "end": v(65.34, -3.88) * mm});
            skLineSegment(sketch, "E24.77.9", {"start": v(63.63, -2.97) * mm, "end": v(65.22, -3.68) * mm});
            skArc(sketch, "E24.77.10", {"start": v(63.68, -1.83) * mm, "mid": v(63.58, -1.9) * mm, "end": v(63.54, -2) * mm});
            skArc(sketch, "E24.77.11", {"start": v(63.51, -2.78) * mm, "mid": v(63.54, -2.9) * mm, "end": v(63.63, -2.97) * mm});
            skArc(sketch, "E24.77.12", {"start": v(65.34, -3.88) * mm, "mid": v(65.31, -3.76) * mm, "end": v(65.22, -3.68) * mm});
            skArc(sketch, "E24.77.13", {"start": v(65.33, -1.27) * mm, "mid": v(65.43, -1.2) * mm, "end": v(65.47, -1.08) * mm});
            skLineSegment(sketch, "E24.78.0", {"start": v(65.47, -0.85) * mm, "end": v(65.48, -0.59) * mm});
            skPoint(sketch, "E24.78.1", {"position": v(63.56, 1.3) * mm});
            skLineSegment(sketch, "E24.78.2", {"start": v(65.31, 2.02) * mm, "end": v(63.7, 1.36) * mm});
            skPoint(sketch, "E24.78.3", {"position": v(63.6, 0.26) * mm});
            skPoint(sketch, "E24.78.4", {"position": v(65.44, 2.07) * mm});
            skLineSegment(sketch, "E24.78.5", {"start": v(65.42, 2.47) * mm, "end": v(65.44, 2.21) * mm});
            skLineSegment(sketch, "E24.78.6", {"start": v(63.57, 1.17) * mm, "end": v(63.59, 0.4) * mm});
            skPoint(sketch, "E24.78.7", {"position": v(65.48, -0.45) * mm});
            skLineSegment(sketch, "E24.78.8", {"start": v(65.44, 2.21) * mm, "end": v(65.48, -0.59) * mm});
            skLineSegment(sketch, "E24.78.9", {"start": v(63.72, 0.21) * mm, "end": v(65.35, -0.4) * mm});
            skArc(sketch, "E24.78.10", {"start": v(63.7, 1.36) * mm, "mid": v(63.6, 1.28) * mm, "end": v(63.57, 1.17) * mm});
            skArc(sketch, "E24.78.11", {"start": v(63.59, 0.4) * mm, "mid": v(63.62, 0.28) * mm, "end": v(63.72, 0.21) * mm});
            skArc(sketch, "E24.78.12", {"start": v(65.48, -0.59) * mm, "mid": v(65.44, -0.47) * mm, "end": v(65.35, -0.4) * mm});
            skArc(sketch, "E24.78.13", {"start": v(65.31, 2.02) * mm, "mid": v(65.4, 2.1) * mm, "end": v(65.44, 2.21) * mm});
            skLineSegment(sketch, "E24.79.0", {"start": v(65.43, 2.45) * mm, "end": v(65.41, 2.7) * mm});
            skPoint(sketch, "E24.79.1", {"position": v(63.39, 4.48) * mm});
            skLineSegment(sketch, "E24.79.2", {"start": v(65.09, 5.3) * mm, "end": v(63.51, 4.54) * mm});
            skPoint(sketch, "E24.79.3", {"position": v(63.48, 3.43) * mm});
            skPoint(sketch, "E24.79.4", {"position": v(65.22, 5.36) * mm});
            skLineSegment(sketch, "E24.79.5", {"start": v(65.17, 5.75) * mm, "end": v(65.2, 5.5) * mm});
            skLineSegment(sketch, "E24.79.6", {"start": v(63.4, 4.34) * mm, "end": v(63.47, 3.57) * mm});
            skPoint(sketch, "E24.79.7", {"position": v(65.4, 2.85) * mm});
            skLineSegment(sketch, "E24.79.8", {"start": v(65.2, 5.5) * mm, "end": v(65.41, 2.7) * mm});
            skLineSegment(sketch, "E24.79.9", {"start": v(63.6, 3.4) * mm, "end": v(65.27, 2.89) * mm});
            skArc(sketch, "E24.79.10", {"start": v(63.51, 4.54) * mm, "mid": v(63.42, 4.46) * mm, "end": v(63.4, 4.34) * mm});
            skArc(sketch, "E24.79.11", {"start": v(63.47, 3.57) * mm, "mid": v(63.51, 3.46) * mm, "end": v(63.6, 3.4) * mm});
            skArc(sketch, "E24.79.12", {"start": v(65.41, 2.7) * mm, "mid": v(65.37, 2.82) * mm, "end": v(65.27, 2.89) * mm});
            skArc(sketch, "E24.79.13", {"start": v(65.09, 5.3) * mm, "mid": v(65.18, 5.38) * mm, "end": v(65.2, 5.5) * mm});
            skLineSegment(sketch, "E24.80.0", {"start": v(65.18, 5.73) * mm, "end": v(65.15, 5.99) * mm});
            skPoint(sketch, "E24.80.1", {"position": v(63.02, 7.64) * mm});
            skLineSegment(sketch, "E24.80.2", {"start": v(64.67, 8.55) * mm, "end": v(63.14, 7.7) * mm});
            skPoint(sketch, "E24.80.3", {"position": v(63.17, 6.6) * mm});
            skPoint(sketch, "E24.80.4", {"position": v(64.79, 8.62) * mm});
            skLineSegment(sketch, "E24.80.5", {"start": v(64.72, 9.02) * mm, "end": v(64.77, 8.76) * mm});
            skLineSegment(sketch, "E24.80.6", {"start": v(63.04, 7.5) * mm, "end": v(63.15, 6.73) * mm});
            skPoint(sketch, "E24.80.7", {"position": v(65.13, 6.13) * mm});
            skLineSegment(sketch, "E24.80.8", {"start": v(64.77, 8.76) * mm, "end": v(65.15, 5.99) * mm});
            skLineSegment(sketch, "E24.80.9", {"start": v(63.3, 6.57) * mm, "end": v(65, 6.16) * mm});
            skArc(sketch, "E24.80.10", {"start": v(63.14, 7.7) * mm, "mid": v(63.06, 7.62) * mm, "end": v(63.04, 7.5) * mm});
            skArc(sketch, "E24.80.11", {"start": v(63.15, 6.73) * mm, "mid": v(63.2, 6.63) * mm, "end": v(63.3, 6.57) * mm});
            skArc(sketch, "E24.80.12", {"start": v(65.15, 5.99) * mm, "mid": v(65.1, 6.1) * mm, "end": v(65, 6.16) * mm});
            skArc(sketch, "E24.80.13", {"start": v(64.67, 8.55) * mm, "mid": v(64.75, 8.64) * mm, "end": v(64.77, 8.76) * mm});
            skLineSegment(sketch, "E24.81.0", {"start": v(64.73, 9) * mm, "end": v(64.68, 9.25) * mm});
            skPoint(sketch, "E24.81.1", {"position": v(62.46, 10.77) * mm});
            skLineSegment(sketch, "E24.81.2", {"start": v(64.05, 11.78) * mm, "end": v(62.57, 10.84) * mm});
            skPoint(sketch, "E24.81.3", {"position": v(62.67, 9.74) * mm});
            skPoint(sketch, "E24.81.4", {"position": v(64.16, 11.86) * mm});
            skLineSegment(sketch, "E24.81.5", {"start": v(64.07, 12.25) * mm, "end": v(64.13, 12) * mm});
            skLineSegment(sketch, "E24.81.6", {"start": v(62.48, 10.63) * mm, "end": v(62.65, 9.87) * mm});
            skPoint(sketch, "E24.81.7", {"position": v(64.66, 9.39) * mm});
            skLineSegment(sketch, "E24.81.8", {"start": v(64.13, 12) * mm, "end": v(64.68, 9.25) * mm});
            skLineSegment(sketch, "E24.81.9", {"start": v(62.8, 9.71) * mm, "end": v(64.52, 9.41) * mm});
            skArc(sketch, "E24.81.10", {"start": v(62.57, 10.84) * mm, "mid": v(62.5, 10.75) * mm, "end": v(62.48, 10.63) * mm});
            skArc(sketch, "E24.81.11", {"start": v(62.65, 9.87) * mm, "mid": v(62.7, 9.77) * mm, "end": v(62.8, 9.71) * mm});
            skArc(sketch, "E24.81.12", {"start": v(64.68, 9.25) * mm, "mid": v(64.63, 9.36) * mm, "end": v(64.52, 9.41) * mm});
            skArc(sketch, "E24.81.13", {"start": v(64.05, 11.78) * mm, "mid": v(64.12, 11.87) * mm, "end": v(64.13, 12) * mm});
            skLineSegment(sketch, "E24.82.0", {"start": v(64.08, 12.22) * mm, "end": v(64.02, 12.47) * mm});
            skPoint(sketch, "E24.82.1", {"position": v(61.7, 13.85) * mm});
            skLineSegment(sketch, "E24.82.2", {"start": v(63.23, 14.96) * mm, "end": v(61.82, 13.93) * mm});
            skPoint(sketch, "E24.82.3", {"position": v(61.98, 12.84) * mm});
            skPoint(sketch, "E24.82.4", {"position": v(63.34, 15.05) * mm});
            skLineSegment(sketch, "E24.82.5", {"start": v(63.23, 15.43) * mm, "end": v(63.3, 15.18) * mm});
            skLineSegment(sketch, "E24.82.6", {"start": v(61.74, 13.72) * mm, "end": v(61.95, 12.97) * mm});
            skPoint(sketch, "E24.82.7", {"position": v(63.99, 12.61) * mm});
            skLineSegment(sketch, "E24.82.8", {"start": v(63.3, 15.18) * mm, "end": v(64.02, 12.47) * mm});
            skLineSegment(sketch, "E24.82.9", {"start": v(62.12, 12.82) * mm, "end": v(63.85, 12.63) * mm});
            skArc(sketch, "E24.82.10", {"start": v(61.82, 13.93) * mm, "mid": v(61.75, 13.84) * mm, "end": v(61.74, 13.72) * mm});
            skArc(sketch, "E24.82.11", {"start": v(61.95, 12.97) * mm, "mid": v(62.01, 12.87) * mm, "end": v(62.12, 12.82) * mm});
            skArc(sketch, "E24.82.12", {"start": v(64.02, 12.47) * mm, "mid": v(63.96, 12.58) * mm, "end": v(63.85, 12.63) * mm});
            skArc(sketch, "E24.82.13", {"start": v(63.23, 14.96) * mm, "mid": v(63.3, 15.06) * mm, "end": v(63.3, 15.18) * mm});
            skLineSegment(sketch, "E24.83.0", {"start": v(63.24, 15.4) * mm, "end": v(63.16, 15.65) * mm});
            skPoint(sketch, "E24.83.1", {"position": v(60.77, 16.89) * mm});
            skLineSegment(sketch, "E24.83.2", {"start": v(62.22, 18.09) * mm, "end": v(60.87, 16.98) * mm});
            skPoint(sketch, "E24.83.3", {"position": v(61.1, 15.9) * mm});
            skPoint(sketch, "E24.83.4", {"position": v(62.33, 18.18) * mm});
            skLineSegment(sketch, "E24.83.5", {"start": v(62.2, 18.56) * mm, "end": v(62.28, 18.31) * mm});
            skLineSegment(sketch, "E24.83.6", {"start": v(60.81, 16.76) * mm, "end": v(61.06, 16.02) * mm});
            skPoint(sketch, "E24.83.7", {"position": v(63.12, 15.79) * mm});
            skLineSegment(sketch, "E24.83.8", {"start": v(62.28, 18.31) * mm, "end": v(63.16, 15.65) * mm});
            skLineSegment(sketch, "E24.83.9", {"start": v(61.24, 15.89) * mm, "end": v(62.98, 15.8) * mm});
            skArc(sketch, "E24.83.10", {"start": v(60.87, 16.98) * mm, "mid": v(60.8, 16.88) * mm, "end": v(60.81, 16.76) * mm});
            skArc(sketch, "E24.83.11", {"start": v(61.06, 16.02) * mm, "mid": v(61.13, 15.93) * mm, "end": v(61.24, 15.89) * mm});
            skArc(sketch, "E24.83.12", {"start": v(63.16, 15.65) * mm, "mid": v(63.1, 15.75) * mm, "end": v(62.98, 15.8) * mm});
            skArc(sketch, "E24.83.13", {"start": v(62.22, 18.09) * mm, "mid": v(62.29, 18.2) * mm, "end": v(62.28, 18.31) * mm});
            skLineSegment(sketch, "E24.84.0", {"start": v(62.2, 18.53) * mm, "end": v(62.11, 18.78) * mm});
            skPoint(sketch, "E24.84.1", {"position": v(59.65, 19.86) * mm});
            skLineSegment(sketch, "E24.84.2", {"start": v(61.02, 21.15) * mm, "end": v(59.75, 19.96) * mm});
            skPoint(sketch, "E24.84.3", {"position": v(60.05, 18.9) * mm});
            skPoint(sketch, "E24.84.4", {"position": v(61.13, 21.25) * mm});
            skLineSegment(sketch, "E24.84.5", {"start": v(60.97, 21.61) * mm, "end": v(61.07, 21.38) * mm});
            skLineSegment(sketch, "E24.84.6", {"start": v(59.7, 19.73) * mm, "end": v(60, 19.02) * mm});
            skPoint(sketch, "E24.84.7", {"position": v(62.06, 18.9) * mm});
            skLineSegment(sketch, "E24.84.8", {"start": v(61.07, 21.38) * mm, "end": v(62.11, 18.78) * mm});
            skLineSegment(sketch, "E24.84.9", {"start": v(60.18, 18.9) * mm, "end": v(61.92, 18.9) * mm});
            skArc(sketch, "E24.84.10", {"start": v(59.75, 19.96) * mm, "mid": v(59.69, 19.85) * mm, "end": v(59.7, 19.73) * mm});
            skArc(sketch, "E24.84.11", {"start": v(60, 19.02) * mm, "mid": v(60.07, 18.93) * mm, "end": v(60.18, 18.9) * mm});
            skArc(sketch, "E24.84.12", {"start": v(62.11, 18.78) * mm, "mid": v(62.04, 18.87) * mm, "end": v(61.92, 18.9) * mm});
            skArc(sketch, "E24.84.13", {"start": v(61.02, 21.15) * mm, "mid": v(61.08, 21.25) * mm, "end": v(61.07, 21.38) * mm});
            skLineSegment(sketch, "E24.85.0", {"start": v(60.98, 21.6) * mm, "end": v(60.87, 21.83) * mm});
            skPoint(sketch, "E24.85.1", {"position": v(58.35, 22.76) * mm});
            skLineSegment(sketch, "E24.85.2", {"start": v(59.64, 24.13) * mm, "end": v(58.44, 22.86) * mm});
            skPoint(sketch, "E24.85.3", {"position": v(58.8, 21.82) * mm});
            skPoint(sketch, "E24.85.4", {"position": v(59.74, 24.23) * mm});
            skLineSegment(sketch, "E24.85.5", {"start": v(59.56, 24.59) * mm, "end": v(59.68, 24.36) * mm});
            skLineSegment(sketch, "E24.85.6", {"start": v(58.4, 22.64) * mm, "end": v(58.75, 21.94) * mm});
            skPoint(sketch, "E24.85.7", {"position": v(60.82, 21.96) * mm});
            skLineSegment(sketch, "E24.85.8", {"start": v(59.68, 24.36) * mm, "end": v(60.87, 21.83) * mm});
            skLineSegment(sketch, "E24.85.9", {"start": v(58.94, 21.83) * mm, "end": v(60.68, 21.95) * mm});
            skArc(sketch, "E24.85.10", {"start": v(58.44, 22.86) * mm, "mid": v(58.39, 22.75) * mm, "end": v(58.4, 22.64) * mm});
            skArc(sketch, "E24.85.11", {"start": v(58.75, 21.94) * mm, "mid": v(58.83, 21.85) * mm, "end": v(58.94, 21.83) * mm});
            skArc(sketch, "E24.85.12", {"start": v(60.87, 21.83) * mm, "mid": v(60.8, 21.92) * mm, "end": v(60.68, 21.95) * mm});
            skArc(sketch, "E24.85.13", {"start": v(59.64, 24.13) * mm, "mid": v(59.7, 24.24) * mm, "end": v(59.68, 24.36) * mm});
            skLineSegment(sketch, "E24.86.0", {"start": v(59.57, 24.57) * mm, "end": v(59.45, 24.8) * mm});
            skPoint(sketch, "E24.86.1", {"position": v(56.87, 25.58) * mm});
            skLineSegment(sketch, "E24.86.2", {"start": v(58.08, 27.02) * mm, "end": v(56.96, 25.68) * mm});
            skPoint(sketch, "E24.86.3", {"position": v(57.39, 24.66) * mm});
            skPoint(sketch, "E24.86.4", {"position": v(58.17, 27.13) * mm});
            skLineSegment(sketch, "E24.86.5", {"start": v(57.97, 27.47) * mm, "end": v(58.1, 27.25) * mm});
            skLineSegment(sketch, "E24.86.6", {"start": v(56.94, 25.46) * mm, "end": v(57.32, 24.78) * mm});
            skPoint(sketch, "E24.86.7", {"position": v(59.39, 24.92) * mm});
            skLineSegment(sketch, "E24.86.8", {"start": v(58.1, 27.25) * mm, "end": v(59.45, 24.8) * mm});
            skLineSegment(sketch, "E24.86.9", {"start": v(57.52, 24.68) * mm, "end": v(59.25, 24.9) * mm});
            skArc(sketch, "E24.86.10", {"start": v(56.96, 25.68) * mm, "mid": v(56.91, 25.57) * mm, "end": v(56.94, 25.46) * mm});
            skArc(sketch, "E24.86.11", {"start": v(57.32, 24.78) * mm, "mid": v(57.4, 24.7) * mm, "end": v(57.52, 24.68) * mm});
            skArc(sketch, "E24.86.12", {"start": v(59.45, 24.8) * mm, "mid": v(59.37, 24.88) * mm, "end": v(59.25, 24.9) * mm});
            skArc(sketch, "E24.86.13", {"start": v(58.08, 27.02) * mm, "mid": v(58.13, 27.13) * mm, "end": v(58.1, 27.25) * mm});
            skLineSegment(sketch, "E24.87.0", {"start": v(57.98, 27.45) * mm, "end": v(57.85, 27.68) * mm});
            skPoint(sketch, "E24.87.1", {"position": v(55.23, 28.3) * mm});
            skLineSegment(sketch, "E24.87.2", {"start": v(56.35, 29.81) * mm, "end": v(55.3, 28.4) * mm});
            skPoint(sketch, "E24.87.3", {"position": v(55.8, 27.41) * mm});
            skPoint(sketch, "E24.87.4", {"position": v(56.43, 29.93) * mm});
            skLineSegment(sketch, "E24.87.5", {"start": v(56.2, 30.26) * mm, "end": v(56.35, 30.04) * mm});
            skLineSegment(sketch, "E24.87.6", {"start": v(55.3, 28.18) * mm, "end": v(55.72, 27.53) * mm});
            skPoint(sketch, "E24.87.7", {"position": v(57.78, 27.8) * mm});
            skLineSegment(sketch, "E24.87.8", {"start": v(56.35, 30.04) * mm, "end": v(57.85, 27.68) * mm});
            skLineSegment(sketch, "E24.87.9", {"start": v(55.93, 27.44) * mm, "end": v(57.64, 27.77) * mm});
            skArc(sketch, "E24.87.10", {"start": v(55.3, 28.4) * mm, "mid": v(55.27, 28.3) * mm, "end": v(55.3, 28.18) * mm});
            skArc(sketch, "E24.87.11", {"start": v(55.72, 27.53) * mm, "mid": v(55.81, 27.45) * mm, "end": v(55.93, 27.44) * mm});
            skArc(sketch, "E24.87.12", {"start": v(57.85, 27.68) * mm, "mid": v(57.76, 27.76) * mm, "end": v(57.64, 27.77) * mm});
            skArc(sketch, "E24.87.13", {"start": v(56.35, 29.81) * mm, "mid": v(56.39, 29.93) * mm, "end": v(56.35, 30.04) * mm});
            skLineSegment(sketch, "E24.88.0", {"start": v(56.22, 30.24) * mm, "end": v(56.08, 30.45) * mm});
            skPoint(sketch, "E24.88.1", {"position": v(53.42, 30.91) * mm});
            skLineSegment(sketch, "E24.88.2", {"start": v(54.45, 32.5) * mm, "end": v(53.5, 31.03) * mm});
            skPoint(sketch, "E24.88.3", {"position": v(54.04, 30.06) * mm});
            skPoint(sketch, "E24.88.4", {"position": v(54.52, 32.61) * mm});
            skLineSegment(sketch, "E24.88.5", {"start": v(54.28, 32.93) * mm, "end": v(54.44, 32.72) * mm});
            skLineSegment(sketch, "E24.88.6", {"start": v(53.5, 30.8) * mm, "end": v(53.96, 30.17) * mm});
            skPoint(sketch, "E24.88.7", {"position": v(56, 30.57) * mm});
            skLineSegment(sketch, "E24.88.8", {"start": v(54.44, 32.72) * mm, "end": v(56.08, 30.45) * mm});
            skLineSegment(sketch, "E24.88.9", {"start": v(54.18, 30.1) * mm, "end": v(55.86, 30.53) * mm});
            skArc(sketch, "E24.88.10", {"start": v(53.5, 31.03) * mm, "mid": v(53.46, 30.91) * mm, "end": v(53.5, 30.8) * mm});
            skArc(sketch, "E24.88.11", {"start": v(53.96, 30.17) * mm, "mid": v(54.06, 30.1) * mm, "end": v(54.18, 30.1) * mm});
            skArc(sketch, "E24.88.12", {"start": v(56.08, 30.45) * mm, "mid": v(55.98, 30.53) * mm, "end": v(55.86, 30.53) * mm});
            skArc(sketch, "E24.88.13", {"start": v(54.45, 32.5) * mm, "mid": v(54.48, 32.6) * mm, "end": v(54.44, 32.72) * mm});
            skLineSegment(sketch, "E24.89.0", {"start": v(54.3, 32.9) * mm, "end": v(54.14, 33.11) * mm});
            skPoint(sketch, "E24.89.1", {"position": v(51.46, 33.4) * mm});
            skLineSegment(sketch, "E24.89.2", {"start": v(52.39, 35.05) * mm, "end": v(51.53, 33.53) * mm});
            skPoint(sketch, "E24.89.3", {"position": v(52.13, 32.6) * mm});
            skPoint(sketch, "E24.89.4", {"position": v(52.46, 35.17) * mm});
            skLineSegment(sketch, "E24.89.5", {"start": v(52.2, 35.48) * mm, "end": v(52.36, 35.28) * mm});
            skLineSegment(sketch, "E24.89.6", {"start": v(51.55, 33.3) * mm, "end": v(52.05, 32.7) * mm});
            skPoint(sketch, "E24.89.7", {"position": v(54.05, 33.23) * mm});
            skLineSegment(sketch, "E24.89.8", {"start": v(52.36, 35.28) * mm, "end": v(54.14, 33.11) * mm});
            skLineSegment(sketch, "E24.89.9", {"start": v(52.26, 32.64) * mm, "end": v(53.92, 33.18) * mm});
            skArc(sketch, "E24.89.10", {"start": v(51.53, 33.53) * mm, "mid": v(51.5, 33.41) * mm, "end": v(51.55, 33.3) * mm});
            skArc(sketch, "E24.89.11", {"start": v(52.05, 32.7) * mm, "mid": v(52.14, 32.64) * mm, "end": v(52.26, 32.64) * mm});
            skArc(sketch, "E24.89.12", {"start": v(54.14, 33.11) * mm, "mid": v(54.04, 33.18) * mm, "end": v(53.92, 33.18) * mm});
            skArc(sketch, "E24.89.13", {"start": v(52.39, 35.05) * mm, "mid": v(52.41, 35.17) * mm, "end": v(52.36, 35.28) * mm});
            skLineSegment(sketch, "E24.90.0", {"start": v(52.2, 35.46) * mm, "end": v(52.04, 35.65) * mm});
            skPoint(sketch, "E24.90.1", {"position": v(49.35, 35.78) * mm});
            skLineSegment(sketch, "E24.90.2", {"start": v(50.17, 37.48) * mm, "end": v(49.4, 35.9) * mm});
            skPoint(sketch, "E24.90.3", {"position": v(50.07, 35.02) * mm});
            skPoint(sketch, "E24.90.4", {"position": v(50.23, 37.6) * mm});
            skLineSegment(sketch, "E24.90.5", {"start": v(49.95, 37.9) * mm, "end": v(50.14, 37.7) * mm});
            skLineSegment(sketch, "E24.90.6", {"start": v(49.44, 35.68) * mm, "end": v(49.98, 35.12) * mm});
            skPoint(sketch, "E24.90.7", {"position": v(51.95, 35.76) * mm});
            skLineSegment(sketch, "E24.90.8", {"start": v(50.14, 37.7) * mm, "end": v(52.04, 35.65) * mm});
            skLineSegment(sketch, "E24.90.9", {"start": v(50.2, 35.07) * mm, "end": v(51.81, 35.7) * mm});
            skArc(sketch, "E24.90.10", {"start": v(49.4, 35.9) * mm, "mid": v(49.39, 35.8) * mm, "end": v(49.44, 35.68) * mm});
            skArc(sketch, "E24.90.11", {"start": v(49.98, 35.12) * mm, "mid": v(50.08, 35.06) * mm, "end": v(50.2, 35.07) * mm});
            skArc(sketch, "E24.90.12", {"start": v(52.04, 35.65) * mm, "mid": v(51.93, 35.72) * mm, "end": v(51.81, 35.7) * mm});
            skArc(sketch, "E24.90.13", {"start": v(50.17, 37.48) * mm, "mid": v(50.2, 37.6) * mm, "end": v(50.14, 37.7) * mm});
            skLineSegment(sketch, "E24.91.0", {"start": v(49.97, 37.87) * mm, "end": v(49.79, 38.06) * mm});
            skPoint(sketch, "E24.91.1", {"position": v(47.1, 38.03) * mm});
            skLineSegment(sketch, "E24.91.2", {"start": v(47.82, 39.77) * mm, "end": v(47.15, 38.15) * mm});
            skPoint(sketch, "E24.91.3", {"position": v(47.86, 37.3) * mm});
            skPoint(sketch, "E24.91.4", {"position": v(47.87, 39.9) * mm});
            skLineSegment(sketch, "E24.91.5", {"start": v(47.57, 40.17) * mm, "end": v(47.77, 40) * mm});
            skLineSegment(sketch, "E24.91.6", {"start": v(47.2, 37.93) * mm, "end": v(47.76, 37.4) * mm});
            skPoint(sketch, "E24.91.7", {"position": v(49.7, 38.16) * mm});
            skLineSegment(sketch, "E24.91.8", {"start": v(47.77, 40) * mm, "end": v(49.79, 38.06) * mm});
            skLineSegment(sketch, "E24.91.9", {"start": v(47.98, 37.37) * mm, "end": v(49.56, 38.1) * mm});
            skArc(sketch, "E24.91.10", {"start": v(47.15, 38.15) * mm, "mid": v(47.14, 38.04) * mm, "end": v(47.2, 37.93) * mm});
            skArc(sketch, "E24.91.11", {"start": v(47.76, 37.4) * mm, "mid": v(47.87, 37.35) * mm, "end": v(47.98, 37.37) * mm});
            skArc(sketch, "E24.91.12", {"start": v(49.79, 38.06) * mm, "mid": v(49.68, 38.12) * mm, "end": v(49.56, 38.1) * mm});
            skArc(sketch, "E24.91.13", {"start": v(47.82, 39.77) * mm, "mid": v(47.83, 39.89) * mm, "end": v(47.77, 40) * mm});
            skLineSegment(sketch, "E24.92.0", {"start": v(47.6, 40.15) * mm, "end": v(47.4, 40.32) * mm});
            skPoint(sketch, "E24.92.1", {"position": v(44.71, 40.13) * mm});
            skLineSegment(sketch, "E24.92.2", {"start": v(45.32, 41.9) * mm, "end": v(44.76, 40.26) * mm});
            skPoint(sketch, "E24.92.3", {"position": v(45.52, 39.46) * mm});
            skPoint(sketch, "E24.92.4", {"position": v(45.37, 42.04) * mm});
            skLineSegment(sketch, "E24.92.5", {"start": v(45.06, 42.3) * mm, "end": v(45.26, 42.13) * mm});
            skLineSegment(sketch, "E24.92.6", {"start": v(44.82, 40.04) * mm, "end": v(45.42, 39.54) * mm});
            skPoint(sketch, "E24.92.7", {"position": v(47.3, 40.42) * mm});
            skLineSegment(sketch, "E24.92.8", {"start": v(45.26, 42.13) * mm, "end": v(47.4, 40.32) * mm});
            skLineSegment(sketch, "E24.92.9", {"start": v(45.64, 39.52) * mm, "end": v(47.17, 40.35) * mm});
            skArc(sketch, "E24.92.10", {"start": v(44.76, 40.26) * mm, "mid": v(44.75, 40.14) * mm, "end": v(44.82, 40.04) * mm});
            skArc(sketch, "E24.92.11", {"start": v(45.42, 39.54) * mm, "mid": v(45.52, 39.5) * mm, "end": v(45.64, 39.52) * mm});
            skArc(sketch, "E24.92.12", {"start": v(47.4, 40.32) * mm, "mid": v(47.29, 40.37) * mm, "end": v(47.17, 40.35) * mm});
            skArc(sketch, "E24.92.13", {"start": v(45.32, 41.9) * mm, "mid": v(45.33, 42.03) * mm, "end": v(45.26, 42.13) * mm});
            skLineSegment(sketch, "E24.93.0", {"start": v(45.08, 42.28) * mm, "end": v(44.87, 42.44) * mm});
            skPoint(sketch, "E24.93.1", {"position": v(42.2, 42.08) * mm});
            skLineSegment(sketch, "E24.93.2", {"start": v(42.7, 43.9) * mm, "end": v(42.24, 42.21) * mm});
            skPoint(sketch, "E24.93.3", {"position": v(43.05, 41.46) * mm});
            skPoint(sketch, "E24.93.4", {"position": v(42.74, 44.03) * mm});
            skLineSegment(sketch, "E24.93.5", {"start": v(42.42, 44.26) * mm, "end": v(42.63, 44.11) * mm});
            skLineSegment(sketch, "E24.93.6", {"start": v(42.31, 42) * mm, "end": v(42.94, 41.54) * mm});
            skPoint(sketch, "E24.93.7", {"position": v(44.76, 42.53) * mm});
            skLineSegment(sketch, "E24.93.8", {"start": v(42.63, 44.11) * mm, "end": v(44.87, 42.44) * mm});
            skLineSegment(sketch, "E24.93.9", {"start": v(43.17, 41.53) * mm, "end": v(44.64, 42.45) * mm});
            skArc(sketch, "E24.93.10", {"start": v(42.24, 42.21) * mm, "mid": v(42.24, 42.1) * mm, "end": v(42.31, 42) * mm});
            skArc(sketch, "E24.93.11", {"start": v(42.94, 41.54) * mm, "mid": v(43.05, 41.5) * mm, "end": v(43.17, 41.53) * mm});
            skArc(sketch, "E24.93.12", {"start": v(44.87, 42.44) * mm, "mid": v(44.76, 42.48) * mm, "end": v(44.64, 42.45) * mm});
            skArc(sketch, "E24.93.13", {"start": v(42.7, 43.9) * mm, "mid": v(42.7, 44.02) * mm, "end": v(42.63, 44.11) * mm});
            skLineSegment(sketch, "E24.94.0", {"start": v(42.44, 44.25) * mm, "end": v(42.22, 44.4) * mm});
            skPoint(sketch, "E24.94.1", {"position": v(39.58, 43.87) * mm});
            skLineSegment(sketch, "E24.94.2", {"start": v(39.97, 45.72) * mm, "end": v(39.6, 44) * mm});
            skPoint(sketch, "E24.94.3", {"position": v(40.47, 43.3) * mm});
            skPoint(sketch, "E24.94.4", {"position": v(40, 45.86) * mm});
            skLineSegment(sketch, "E24.94.5", {"start": v(39.66, 46.06) * mm, "end": v(39.88, 45.93) * mm});
            skLineSegment(sketch, "E24.94.6", {"start": v(39.7, 43.8) * mm, "end": v(40.35, 43.38) * mm});
            skPoint(sketch, "E24.94.7", {"position": v(42.1, 44.48) * mm});
            skLineSegment(sketch, "E24.94.8", {"start": v(39.88, 45.93) * mm, "end": v(42.22, 44.4) * mm});
            skLineSegment(sketch, "E24.94.9", {"start": v(40.58, 43.38) * mm, "end": v(42, 44.4) * mm});
            skArc(sketch, "E24.94.10", {"start": v(39.6, 44) * mm, "mid": v(39.62, 43.89) * mm, "end": v(39.7, 43.8) * mm});
            skArc(sketch, "E24.94.11", {"start": v(40.35, 43.38) * mm, "mid": v(40.46, 43.35) * mm, "end": v(40.58, 43.38) * mm});
            skArc(sketch, "E24.94.12", {"start": v(42.22, 44.4) * mm, "mid": v(42.1, 44.43) * mm, "end": v(42, 44.4) * mm});
            skArc(sketch, "E24.94.13", {"start": v(39.97, 45.72) * mm, "mid": v(39.96, 45.84) * mm, "end": v(39.88, 45.93) * mm});
            skLineSegment(sketch, "E24.95.0", {"start": v(39.68, 46.05) * mm, "end": v(39.46, 46.19) * mm});
            skPoint(sketch, "E24.95.1", {"position": v(36.85, 45.5) * mm});
            skLineSegment(sketch, "E24.95.2", {"start": v(37.13, 47.37) * mm, "end": v(36.87, 45.64) * mm});
            skPoint(sketch, "E24.95.3", {"position": v(37.77, 45) * mm});
            skPoint(sketch, "E24.95.4", {"position": v(37.15, 47.5) * mm});
            skLineSegment(sketch, "E24.95.5", {"start": v(36.8, 47.7) * mm, "end": v(37.03, 47.58) * mm});
            skLineSegment(sketch, "E24.95.6", {"start": v(36.97, 45.44) * mm, "end": v(37.65, 45.06) * mm});
            skPoint(sketch, "E24.95.7", {"position": v(39.34, 46.26) * mm});
            skLineSegment(sketch, "E24.95.8", {"start": v(37.03, 47.58) * mm, "end": v(39.46, 46.19) * mm});
            skLineSegment(sketch, "E24.95.9", {"start": v(37.88, 45.08) * mm, "end": v(39.23, 46.17) * mm});
            skArc(sketch, "E24.95.10", {"start": v(36.87, 45.64) * mm, "mid": v(36.9, 45.52) * mm, "end": v(36.97, 45.44) * mm});
            skArc(sketch, "E24.95.11", {"start": v(37.65, 45.06) * mm, "mid": v(37.77, 45.03) * mm, "end": v(37.88, 45.08) * mm});
            skArc(sketch, "E24.95.12", {"start": v(39.46, 46.19) * mm, "mid": v(39.34, 46.22) * mm, "end": v(39.23, 46.17) * mm});
            skArc(sketch, "E24.95.13", {"start": v(37.13, 47.37) * mm, "mid": v(37.11, 47.49) * mm, "end": v(37.03, 47.58) * mm});
            skLineSegment(sketch, "E24.96.0", {"start": v(36.82, 47.69) * mm, "end": v(36.6, 47.8) * mm});
            skPoint(sketch, "E24.96.1", {"position": v(34.03, 46.97) * mm});
            skLineSegment(sketch, "E24.96.2", {"start": v(34.2, 48.84) * mm, "end": v(34.04, 47.1) * mm});
            skPoint(sketch, "E24.96.3", {"position": v(34.98, 46.51) * mm});
            skPoint(sketch, "E24.96.4", {"position": v(34.2, 48.99) * mm});
            skLineSegment(sketch, "E24.96.5", {"start": v(33.84, 49.15) * mm, "end": v(34.08, 49.04) * mm});
            skLineSegment(sketch, "E24.96.6", {"start": v(34.16, 46.9) * mm, "end": v(34.86, 46.57) * mm});
            skPoint(sketch, "E24.96.7", {"position": v(36.47, 47.87) * mm});
            skLineSegment(sketch, "E24.96.8", {"start": v(34.08, 49.04) * mm, "end": v(36.6, 47.8) * mm});
            skLineSegment(sketch, "E24.96.9", {"start": v(35.08, 46.6) * mm, "end": v(36.36, 47.78) * mm});
            skArc(sketch, "E24.96.10", {"start": v(34.04, 47.1) * mm, "mid": v(34.07, 46.99) * mm, "end": v(34.16, 46.9) * mm});
            skArc(sketch, "E24.96.11", {"start": v(34.86, 46.57) * mm, "mid": v(34.97, 46.55) * mm, "end": v(35.08, 46.6) * mm});
            skArc(sketch, "E24.96.12", {"start": v(36.6, 47.8) * mm, "mid": v(36.47, 47.83) * mm, "end": v(36.36, 47.78) * mm});
            skArc(sketch, "E24.96.13", {"start": v(34.2, 48.84) * mm, "mid": v(34.17, 48.96) * mm, "end": v(34.08, 49.04) * mm});
            skLineSegment(sketch, "E24.97.0", {"start": v(33.87, 49.14) * mm, "end": v(33.63, 49.25) * mm});
            skPoint(sketch, "E24.97.1", {"position": v(31.13, 48.25) * mm});
            skLineSegment(sketch, "E24.97.2", {"start": v(31.18, 50.14) * mm, "end": v(31.13, 48.4) * mm});
            skPoint(sketch, "E24.97.3", {"position": v(32.1, 47.86) * mm});
            skPoint(sketch, "E24.97.4", {"position": v(31.18, 50.28) * mm});
            skLineSegment(sketch, "E24.97.5", {"start": v(30.8, 50.42) * mm, "end": v(31.05, 50.33) * mm});
            skLineSegment(sketch, "E24.97.6", {"start": v(31.25, 48.2) * mm, "end": v(31.97, 47.9) * mm});
            skPoint(sketch, "E24.97.7", {"position": v(33.5, 49.3) * mm});
            skLineSegment(sketch, "E24.97.8", {"start": v(31.05, 50.33) * mm, "end": v(33.63, 49.25) * mm});
            skLineSegment(sketch, "E24.97.9", {"start": v(32.2, 47.95) * mm, "end": v(33.4, 49.2) * mm});
            skArc(sketch, "E24.97.10", {"start": v(31.13, 48.4) * mm, "mid": v(31.16, 48.28) * mm, "end": v(31.25, 48.2) * mm});
            skArc(sketch, "E24.97.11", {"start": v(31.97, 47.9) * mm, "mid": v(32.1, 47.9) * mm, "end": v(32.2, 47.95) * mm});
            skArc(sketch, "E24.97.12", {"start": v(33.63, 49.25) * mm, "mid": v(33.51, 49.26) * mm, "end": v(33.4, 49.2) * mm});
            skArc(sketch, "E24.97.13", {"start": v(31.18, 50.14) * mm, "mid": v(31.14, 50.26) * mm, "end": v(31.05, 50.33) * mm});
            skLineSegment(sketch, "E24.98.0", {"start": v(30.83, 50.41) * mm, "end": v(30.59, 50.5) * mm});
            skPoint(sketch, "E24.98.1", {"position": v(28.15, 49.36) * mm});
            skLineSegment(sketch, "E24.98.2", {"start": v(28.08, 51.25) * mm, "end": v(28.14, 49.5) * mm});
            skPoint(sketch, "E24.98.3", {"position": v(29.14, 49.03) * mm});
            skPoint(sketch, "E24.98.4", {"position": v(28.08, 51.39) * mm});
            skLineSegment(sketch, "E24.98.5", {"start": v(27.7, 51.5) * mm, "end": v(27.94, 51.43) * mm});
            skLineSegment(sketch, "E24.98.6", {"start": v(28.28, 49.32) * mm, "end": v(29.02, 49.07) * mm});
            skPoint(sketch, "E24.98.7", {"position": v(30.46, 50.56) * mm});
            skLineSegment(sketch, "E24.98.8", {"start": v(27.94, 51.43) * mm, "end": v(30.59, 50.5) * mm});
            skLineSegment(sketch, "E24.98.9", {"start": v(29.23, 49.13) * mm, "end": v(30.36, 50.45) * mm});
            skArc(sketch, "E24.98.10", {"start": v(28.14, 49.5) * mm, "mid": v(28.18, 49.39) * mm, "end": v(28.28, 49.32) * mm});
            skArc(sketch, "E24.98.11", {"start": v(29.02, 49.07) * mm, "mid": v(29.13, 49.07) * mm, "end": v(29.23, 49.13) * mm});
            skArc(sketch, "E24.98.12", {"start": v(30.59, 50.5) * mm, "mid": v(30.47, 50.51) * mm, "end": v(30.36, 50.45) * mm});
            skArc(sketch, "E24.98.13", {"start": v(28.08, 51.25) * mm, "mid": v(28.04, 51.36) * mm, "end": v(27.94, 51.43) * mm});
            skLineSegment(sketch, "E24.99.0", {"start": v(27.72, 51.5) * mm, "end": v(27.47, 51.58) * mm});
            skPoint(sketch, "E24.99.1", {"position": v(25.1, 50.29) * mm});
            skLineSegment(sketch, "E24.99.2", {"start": v(24.93, 52.16) * mm, "end": v(25.1, 50.42) * mm});
            skPoint(sketch, "E24.99.3", {"position": v(26.12, 50.01) * mm});
            skPoint(sketch, "E24.99.4", {"position": v(24.91, 52.3) * mm});
            skLineSegment(sketch, "E24.99.5", {"start": v(24.53, 52.4) * mm, "end": v(24.78, 52.34) * mm});
            skLineSegment(sketch, "E24.99.6", {"start": v(25.24, 50.25) * mm, "end": v(26, 50.05) * mm});
            skPoint(sketch, "E24.99.7", {"position": v(27.34, 51.62) * mm});
            skLineSegment(sketch, "E24.99.8", {"start": v(24.78, 52.34) * mm, "end": v(27.47, 51.58) * mm});
            skLineSegment(sketch, "E24.99.9", {"start": v(26.2, 50.12) * mm, "end": v(27.25, 51.5) * mm});
            skArc(sketch, "E24.99.10", {"start": v(25.1, 50.42) * mm, "mid": v(25.14, 50.31) * mm, "end": v(25.24, 50.25) * mm});
            skArc(sketch, "E24.99.11", {"start": v(26, 50.05) * mm, "mid": v(26.1, 50.05) * mm, "end": v(26.2, 50.12) * mm});
            skArc(sketch, "E24.99.12", {"start": v(27.47, 51.58) * mm, "mid": v(27.35, 51.58) * mm, "end": v(27.25, 51.5) * mm});
            skArc(sketch, "E24.99.13", {"start": v(24.93, 52.16) * mm, "mid": v(24.88, 52.27) * mm, "end": v(24.78, 52.34) * mm});
            skLineSegment(sketch, "E24.100.0", {"start": v(24.55, 52.4) * mm, "end": v(24.3, 52.46) * mm});
            skPoint(sketch, "E24.100.1", {"position": v(22.02, 51.02) * mm});
            skLineSegment(sketch, "E24.100.2", {"start": v(21.72, 52.89) * mm, "end": v(22, 51.16) * mm});
            skPoint(sketch, "E24.100.3", {"position": v(23.05, 50.81) * mm});
            skPoint(sketch, "E24.100.4", {"position": v(21.7, 53.03) * mm});
            skLineSegment(sketch, "E24.100.5", {"start": v(21.3, 53.1) * mm, "end": v(21.56, 53.05) * mm});
            skLineSegment(sketch, "E24.100.6", {"start": v(22.15, 51) * mm, "end": v(22.91, 50.84) * mm});
            skPoint(sketch, "E24.100.7", {"position": v(24.16, 52.5) * mm});
            skLineSegment(sketch, "E24.100.8", {"start": v(21.56, 53.05) * mm, "end": v(24.3, 52.46) * mm});
            skLineSegment(sketch, "E24.100.9", {"start": v(23.12, 50.92) * mm, "end": v(24.08, 52.37) * mm});
            skArc(sketch, "E24.100.10", {"start": v(22, 51.16) * mm, "mid": v(22.05, 51.05) * mm, "end": v(22.15, 51) * mm});
            skArc(sketch, "E24.100.11", {"start": v(22.91, 50.84) * mm, "mid": v(23.03, 50.85) * mm, "end": v(23.12, 50.92) * mm});
            skArc(sketch, "E24.100.12", {"start": v(24.3, 52.46) * mm, "mid": v(24.18, 52.45) * mm, "end": v(24.08, 52.37) * mm});
            skArc(sketch, "E24.100.13", {"start": v(21.72, 52.89) * mm, "mid": v(21.67, 53) * mm, "end": v(21.56, 53.05) * mm});
            skLineSegment(sketch, "E24.101.0", {"start": v(21.33, 53.1) * mm, "end": v(21.08, 53.14) * mm});
            skPoint(sketch, "E24.101.1", {"position": v(18.89, 51.57) * mm});
            skLineSegment(sketch, "E24.101.2", {"start": v(18.48, 53.41) * mm, "end": v(18.86, 51.7) * mm});
            skPoint(sketch, "E24.101.3", {"position": v(19.93, 51.42) * mm});
            skPoint(sketch, "E24.101.4", {"position": v(18.45, 53.55) * mm});
            skLineSegment(sketch, "E24.101.5", {"start": v(18.05, 53.6) * mm, "end": v(18.3, 53.57) * mm});
            skLineSegment(sketch, "E24.101.6", {"start": v(19.02, 51.55) * mm, "end": v(19.8, 51.44) * mm});
            skPoint(sketch, "E24.101.7", {"position": v(20.94, 53.17) * mm});
            skLineSegment(sketch, "E24.101.8", {"start": v(18.3, 53.57) * mm, "end": v(21.08, 53.14) * mm});
            skLineSegment(sketch, "E24.101.9", {"start": v(20, 51.54) * mm, "end": v(20.87, 53.04) * mm});
            skArc(sketch, "E24.101.10", {"start": v(18.86, 51.7) * mm, "mid": v(18.92, 51.6) * mm, "end": v(19.02, 51.55) * mm});
            skArc(sketch, "E24.101.11", {"start": v(19.8, 51.44) * mm, "mid": v(19.9, 51.46) * mm, "end": v(20, 51.54) * mm});
            skArc(sketch, "E24.101.12", {"start": v(21.08, 53.14) * mm, "mid": v(20.96, 53.13) * mm, "end": v(20.87, 53.04) * mm});
            skArc(sketch, "E24.101.13", {"start": v(18.48, 53.41) * mm, "mid": v(18.42, 53.52) * mm, "end": v(18.3, 53.57) * mm});
            skLineSegment(sketch, "E24.102.0", {"start": v(18.08, 53.6) * mm, "end": v(17.82, 53.63) * mm});
            skPoint(sketch, "E24.102.1", {"position": v(15.73, 51.93) * mm});
            skLineSegment(sketch, "E24.102.2", {"start": v(15.21, 53.74) * mm, "end": v(15.7, 52.06) * mm});
            skPoint(sketch, "E24.102.3", {"position": v(16.78, 51.84) * mm});
            skPoint(sketch, "E24.102.4", {"position": v(15.17, 53.88) * mm});
            skLineSegment(sketch, "E24.102.5", {"start": v(14.77, 53.9) * mm, "end": v(15.03, 53.88) * mm});
            skLineSegment(sketch, "E24.102.6", {"start": v(15.87, 51.92) * mm, "end": v(16.64, 51.85) * mm});
            skPoint(sketch, "E24.102.7", {"position": v(17.68, 53.64) * mm});
            skLineSegment(sketch, "E24.102.8", {"start": v(15.03, 53.88) * mm, "end": v(17.82, 53.63) * mm});
            skLineSegment(sketch, "E24.102.9", {"start": v(16.84, 51.96) * mm, "end": v(17.62, 53.52) * mm});
            skArc(sketch, "E24.102.10", {"start": v(15.7, 52.06) * mm, "mid": v(15.76, 51.96) * mm, "end": v(15.87, 51.92) * mm});
            skArc(sketch, "E24.102.11", {"start": v(16.64, 51.85) * mm, "mid": v(16.76, 51.88) * mm, "end": v(16.84, 51.96) * mm});
            skArc(sketch, "E24.102.12", {"start": v(17.82, 53.63) * mm, "mid": v(17.7, 53.6) * mm, "end": v(17.62, 53.52) * mm});
            skArc(sketch, "E24.102.13", {"start": v(15.21, 53.74) * mm, "mid": v(15.14, 53.84) * mm, "end": v(15.03, 53.88) * mm});
            skPoint(sketch, "E24.center", {"position": v(11.48, 0) * mm});
            skSolve(sketch);
        }
        {
            var Q0;
            Q0=makeQuery(id+"F13.imprint","IMPRINT",FACE,{"disambiguationData":[TD([[makeQuery(id+"F13.imprint","IMPRINT",EDGE,{"derivedFrom":sQuery(id+"F13.wireOp",EDGE,"E16")}),1.0]])]});
            var Q1;
            {var subQ0=sQuery(id+"F13.wireOp",EDGE,"E23");var subQ1=makeQuery(id+"F8.opExtrude","CAP_EDGE",EDGE,{"disambiguationData":[OSD([sQuery(id+"F7.wireOp",EDGE,"E8")])],"isStart":true});var subQ2=makeQuery(id+"F13.imprint","INTERSECT",VERTEX,{"disambiguationData":[OD(0.0)],"derivedFrom":[subQ1,subQ0]});Q1=makeQuery(id+"F13.imprint","IMPRINT",FACE,{"disambiguationData":[TD([[makeQuery(id+"F13.imprint","IMPRINT",EDGE,{"disambiguationData":[TD([[subQ2,-1.0]])],"derivedFrom":subQ0}),1.0]])]});}
            extrude(context, id + "F14", {"entities" : qUnion([Q0, Q1]), "operationType" : NewBodyOperationType.REMOVE, "oppositeDirection" : true, "depth" : 4.5 * mm, "offsetDistance" : 25 * mm});
        }
        {
            var Q0;
            {var subQ0=sQuery(id+"F13.wireOp",EDGE,"E24.102.8");var subQ1=makeQuery(id+"F8.opExtrude","CAP_EDGE",EDGE,{"disambiguationData":[OSD([sQuery(id+"F7.wireOp",EDGE,"E8")])],"isStart":true});var subQ2=makeQuery(id+"F13.imprint","INTERSECT",VERTEX,{"disambiguationData":[OD(0.0)],"derivedFrom":[subQ1,subQ0]});Q0=makeQuery(id+"F13.imprint","IMPRINT",FACE,{"disambiguationData":[TD([[makeQuery(id+"F13.imprint","IMPRINT",EDGE,{"disambiguationData":[TD([[subQ2,-1.0]])],"derivedFrom":subQ0}),1.0]])]});}
            var Q1;
            {var subQ5=sQuery(id+"F13.wireOp",EDGE,"E24.102.2");Q1=makeQuery(id+"F13.imprint","IMPRINT",FACE,{"disambiguationData":[TD([[makeQuery(id+"F13.imprint","IMPRINT",EDGE,{"derivedFrom":subQ5}),1.0]])]});}
            extrude(context, id + "F15", {"entities" : qUnion([Q0, Q1]), "operationType" : NewBodyOperationType.REMOVE, "oppositeDirection" : true, "depth" : 4.5 * mm, "offsetDistance" : 25 * mm});
        }
        {
            var Q0;
            {var subQ7=sQuery(id+"F13.wireOp",EDGE,"E24.101.2");Q0=makeQuery(id+"F13.imprint","IMPRINT",FACE,{"disambiguationData":[TD([[makeQuery(id+"F13.imprint","IMPRINT",EDGE,{"derivedFrom":subQ7}),1.0]])]});}
            var Q1;
            {var subQ0=sQuery(id+"F13.wireOp",EDGE,"E24.101.8");var subQ1=makeQuery(id+"F8.opExtrude","CAP_EDGE",EDGE,{"disambiguationData":[OSD([sQuery(id+"F7.wireOp",EDGE,"E8")])],"isStart":true});var subQ2=makeQuery(id+"F13.imprint","INTERSECT",VERTEX,{"disambiguationData":[OD(0.0)],"derivedFrom":[subQ1,subQ0]});Q1=makeQuery(id+"F13.imprint","IMPRINT",FACE,{"disambiguationData":[TD([[makeQuery(id+"F13.imprint","IMPRINT",EDGE,{"disambiguationData":[TD([[subQ2,-1.0]])],"derivedFrom":subQ0}),1.0]])]});}
            extrude(context, id + "F16", {"entities" : qUnion([Q0, Q1]), "operationType" : NewBodyOperationType.REMOVE, "oppositeDirection" : true, "depth" : 4.5 * mm, "offsetDistance" : 25 * mm});
        }
        {
            var Q0;
            {var subQ5=sQuery(id+"F13.wireOp",EDGE,"E24.100.2");Q0=makeQuery(id+"F13.imprint","IMPRINT",FACE,{"disambiguationData":[TD([[makeQuery(id+"F13.imprint","IMPRINT",EDGE,{"derivedFrom":subQ5}),1.0]])]});}
            var Q1;
            {var subQ0=sQuery(id+"F13.wireOp",EDGE,"E24.100.8");var subQ1=makeQuery(id+"F8.opExtrude","CAP_EDGE",EDGE,{"disambiguationData":[OSD([sQuery(id+"F7.wireOp",EDGE,"E8")])],"isStart":true});var subQ2=makeQuery(id+"F13.imprint","INTERSECT",VERTEX,{"disambiguationData":[OD(0.0)],"derivedFrom":[subQ1,subQ0]});Q1=makeQuery(id+"F13.imprint","IMPRINT",FACE,{"disambiguationData":[TD([[makeQuery(id+"F13.imprint","IMPRINT",EDGE,{"disambiguationData":[TD([[subQ2,-1.0]])],"derivedFrom":subQ0}),1.0]])]});}
            extrude(context, id + "F17", {"entities" : qUnion([Q0, Q1]), "operationType" : NewBodyOperationType.REMOVE, "oppositeDirection" : true, "depth" : 4.5 * mm, "offsetDistance" : 25 * mm});
        }
        {
            var Q0;
            {var subQ7=sQuery(id+"F13.wireOp",EDGE,"E24.99.2");Q0=makeQuery(id+"F13.imprint","IMPRINT",FACE,{"disambiguationData":[TD([[makeQuery(id+"F13.imprint","IMPRINT",EDGE,{"derivedFrom":subQ7}),1.0]])]});}
            var Q1;
            {var subQ0=sQuery(id+"F13.wireOp",EDGE,"E24.99.8");var subQ1=makeQuery(id+"F8.opExtrude","CAP_EDGE",EDGE,{"disambiguationData":[OSD([sQuery(id+"F7.wireOp",EDGE,"E8")])],"isStart":true});var subQ2=makeQuery(id+"F13.imprint","INTERSECT",VERTEX,{"disambiguationData":[OD(0.0)],"derivedFrom":[subQ1,subQ0]});Q1=makeQuery(id+"F13.imprint","IMPRINT",FACE,{"disambiguationData":[TD([[makeQuery(id+"F13.imprint","IMPRINT",EDGE,{"disambiguationData":[TD([[subQ2,-1.0]])],"derivedFrom":subQ0}),1.0]])]});}
            extrude(context, id + "F18", {"entities" : qUnion([Q0, Q1]), "operationType" : NewBodyOperationType.REMOVE, "oppositeDirection" : true, "depth" : 4.5 * mm, "offsetDistance" : 25 * mm});
        }
        {
            var Q0;
            {var subQ7=sQuery(id+"F13.wireOp",EDGE,"E24.98.2");Q0=makeQuery(id+"F13.imprint","IMPRINT",FACE,{"disambiguationData":[TD([[makeQuery(id+"F13.imprint","IMPRINT",EDGE,{"derivedFrom":subQ7}),1.0]])]});}
            var Q1;
            {var subQ0=sQuery(id+"F13.wireOp",EDGE,"E24.98.8");var subQ1=makeQuery(id+"F8.opExtrude","CAP_EDGE",EDGE,{"disambiguationData":[OSD([sQuery(id+"F7.wireOp",EDGE,"E8")])],"isStart":true});var subQ2=makeQuery(id+"F13.imprint","INTERSECT",VERTEX,{"disambiguationData":[OD(0.0)],"derivedFrom":[subQ1,subQ0]});Q1=makeQuery(id+"F13.imprint","IMPRINT",FACE,{"disambiguationData":[TD([[makeQuery(id+"F13.imprint","IMPRINT",EDGE,{"disambiguationData":[TD([[subQ2,-1.0]])],"derivedFrom":subQ0}),1.0]])]});}
            extrude(context, id + "F19", {"entities" : qUnion([Q0, Q1]), "operationType" : NewBodyOperationType.REMOVE, "oppositeDirection" : true, "depth" : 4.5 * mm, "offsetDistance" : 25 * mm});
        }
        {
            var Q0;
            {var subQ5=sQuery(id+"F13.wireOp",EDGE,"E24.97.2");Q0=makeQuery(id+"F13.imprint","IMPRINT",FACE,{"disambiguationData":[TD([[makeQuery(id+"F13.imprint","IMPRINT",EDGE,{"derivedFrom":subQ5}),1.0]])]});}
            var Q1;
            {var subQ0=sQuery(id+"F13.wireOp",EDGE,"E24.97.8");var subQ1=makeQuery(id+"F8.opExtrude","CAP_EDGE",EDGE,{"disambiguationData":[OSD([sQuery(id+"F7.wireOp",EDGE,"E8")])],"isStart":true});var subQ2=makeQuery(id+"F13.imprint","INTERSECT",VERTEX,{"disambiguationData":[OD(0.0)],"derivedFrom":[subQ1,subQ0]});Q1=makeQuery(id+"F13.imprint","IMPRINT",FACE,{"disambiguationData":[TD([[makeQuery(id+"F13.imprint","IMPRINT",EDGE,{"disambiguationData":[TD([[subQ2,-1.0]])],"derivedFrom":subQ0}),1.0]])]});}
            extrude(context, id + "F20", {"entities" : qUnion([Q0, Q1]), "operationType" : NewBodyOperationType.REMOVE, "oppositeDirection" : true, "depth" : 4.5 * mm, "offsetDistance" : 25 * mm});
        }
        {
            var Q0;
            {var subQ7=sQuery(id+"F13.wireOp",EDGE,"E24.96.2");Q0=makeQuery(id+"F13.imprint","IMPRINT",FACE,{"disambiguationData":[TD([[makeQuery(id+"F13.imprint","IMPRINT",EDGE,{"derivedFrom":subQ7}),1.0]])]});}
            var Q1;
            {var subQ0=sQuery(id+"F13.wireOp",EDGE,"E24.96.8");var subQ1=makeQuery(id+"F8.opExtrude","CAP_EDGE",EDGE,{"disambiguationData":[OSD([sQuery(id+"F7.wireOp",EDGE,"E8")])],"isStart":true});var subQ2=makeQuery(id+"F13.imprint","INTERSECT",VERTEX,{"disambiguationData":[OD(0.0)],"derivedFrom":[subQ1,subQ0]});Q1=makeQuery(id+"F13.imprint","IMPRINT",FACE,{"disambiguationData":[TD([[makeQuery(id+"F13.imprint","IMPRINT",EDGE,{"disambiguationData":[TD([[subQ2,-1.0]])],"derivedFrom":subQ0}),1.0]])]});}
            extrude(context, id + "F21", {"entities" : qUnion([Q0, Q1]), "operationType" : NewBodyOperationType.REMOVE, "oppositeDirection" : true, "depth" : 4.5 * mm, "offsetDistance" : 25 * mm});
        }
        {
            var Q0;
            {var subQ5=sQuery(id+"F13.wireOp",EDGE,"E24.95.2");Q0=makeQuery(id+"F13.imprint","IMPRINT",FACE,{"disambiguationData":[TD([[makeQuery(id+"F13.imprint","IMPRINT",EDGE,{"derivedFrom":subQ5}),1.0]])]});}
            var Q1;
            {var subQ0=sQuery(id+"F13.wireOp",EDGE,"E24.95.8");var subQ1=makeQuery(id+"F8.opExtrude","CAP_EDGE",EDGE,{"disambiguationData":[OSD([sQuery(id+"F7.wireOp",EDGE,"E8")])],"isStart":true});var subQ2=makeQuery(id+"F13.imprint","INTERSECT",VERTEX,{"disambiguationData":[OD(0.0)],"derivedFrom":[subQ1,subQ0]});Q1=makeQuery(id+"F13.imprint","IMPRINT",FACE,{"disambiguationData":[TD([[makeQuery(id+"F13.imprint","IMPRINT",EDGE,{"disambiguationData":[TD([[subQ2,-1.0]])],"derivedFrom":subQ0}),1.0]])]});}
            extrude(context, id + "F22", {"entities" : qUnion([Q0, Q1]), "operationType" : NewBodyOperationType.REMOVE, "oppositeDirection" : true, "depth" : 4.5 * mm, "offsetDistance" : 25 * mm});
        }
        {
            var Q0;
            {var subQ0=sQuery(id+"F13.wireOp",EDGE,"E24.94.8");var subQ1=makeQuery(id+"F8.opExtrude","CAP_EDGE",EDGE,{"disambiguationData":[OSD([sQuery(id+"F7.wireOp",EDGE,"E8")])],"isStart":true});var subQ2=makeQuery(id+"F13.imprint","INTERSECT",VERTEX,{"disambiguationData":[OD(0.0)],"derivedFrom":[subQ1,subQ0]});Q0=makeQuery(id+"F13.imprint","IMPRINT",FACE,{"disambiguationData":[TD([[makeQuery(id+"F13.imprint","IMPRINT",EDGE,{"disambiguationData":[TD([[subQ2,-1.0]])],"derivedFrom":subQ0}),1.0]])]});}
            var Q1;
            {var subQ5=sQuery(id+"F13.wireOp",EDGE,"E24.94.2");Q1=makeQuery(id+"F13.imprint","IMPRINT",FACE,{"disambiguationData":[TD([[makeQuery(id+"F13.imprint","IMPRINT",EDGE,{"derivedFrom":subQ5}),1.0]])]});}
            extrude(context, id + "F23", {"entities" : qUnion([Q0, Q1]), "operationType" : NewBodyOperationType.REMOVE, "oppositeDirection" : true, "depth" : 4.5 * mm, "offsetDistance" : 25 * mm});
        }
        {
            var Q0;
            {var subQ7=sQuery(id+"F13.wireOp",EDGE,"E24.93.2");Q0=makeQuery(id+"F13.imprint","IMPRINT",FACE,{"disambiguationData":[TD([[makeQuery(id+"F13.imprint","IMPRINT",EDGE,{"derivedFrom":subQ7}),1.0]])]});}
            var Q1;
            {var subQ0=sQuery(id+"F13.wireOp",EDGE,"E24.93.8");var subQ1=makeQuery(id+"F8.opExtrude","CAP_EDGE",EDGE,{"disambiguationData":[OSD([sQuery(id+"F7.wireOp",EDGE,"E8")])],"isStart":true});var subQ2=makeQuery(id+"F13.imprint","INTERSECT",VERTEX,{"disambiguationData":[OD(0.0)],"derivedFrom":[subQ1,subQ0]});Q1=makeQuery(id+"F13.imprint","IMPRINT",FACE,{"disambiguationData":[TD([[makeQuery(id+"F13.imprint","IMPRINT",EDGE,{"disambiguationData":[TD([[subQ2,-1.0]])],"derivedFrom":subQ0}),1.0]])]});}
            extrude(context, id + "F24", {"entities" : qUnion([Q0, Q1]), "operationType" : NewBodyOperationType.REMOVE, "oppositeDirection" : true, "depth" : 4.5 * mm, "offsetDistance" : 25 * mm});
        }
        {
            var Q0;
            {var subQ5=sQuery(id+"F13.wireOp",EDGE,"E24.92.2");Q0=makeQuery(id+"F13.imprint","IMPRINT",FACE,{"disambiguationData":[TD([[makeQuery(id+"F13.imprint","IMPRINT",EDGE,{"derivedFrom":subQ5}),1.0]])]});}
            var Q1;
            {var subQ0=sQuery(id+"F13.wireOp",EDGE,"E24.92.8");var subQ1=makeQuery(id+"F8.opExtrude","CAP_EDGE",EDGE,{"disambiguationData":[OSD([sQuery(id+"F7.wireOp",EDGE,"E8")])],"isStart":true});var subQ2=makeQuery(id+"F13.imprint","INTERSECT",VERTEX,{"disambiguationData":[OD(0.0)],"derivedFrom":[subQ1,subQ0]});Q1=makeQuery(id+"F13.imprint","IMPRINT",FACE,{"disambiguationData":[TD([[makeQuery(id+"F13.imprint","IMPRINT",EDGE,{"disambiguationData":[TD([[subQ2,-1.0]])],"derivedFrom":subQ0}),1.0]])]});}
            extrude(context, id + "F25", {"entities" : qUnion([Q0, Q1]), "operationType" : NewBodyOperationType.REMOVE, "oppositeDirection" : true, "depth" : 4.5 * mm, "offsetDistance" : 25 * mm});
        }
        {
            var Q0;
            {var subQ7=sQuery(id+"F13.wireOp",EDGE,"E24.91.2");Q0=makeQuery(id+"F13.imprint","IMPRINT",FACE,{"disambiguationData":[TD([[makeQuery(id+"F13.imprint","IMPRINT",EDGE,{"derivedFrom":subQ7}),1.0]])]});}
            var Q1;
            {var subQ0=sQuery(id+"F13.wireOp",EDGE,"E24.91.8");var subQ1=makeQuery(id+"F8.opExtrude","CAP_EDGE",EDGE,{"disambiguationData":[OSD([sQuery(id+"F7.wireOp",EDGE,"E8")])],"isStart":true});var subQ2=makeQuery(id+"F13.imprint","INTERSECT",VERTEX,{"disambiguationData":[OD(0.0)],"derivedFrom":[subQ1,subQ0]});Q1=makeQuery(id+"F13.imprint","IMPRINT",FACE,{"disambiguationData":[TD([[makeQuery(id+"F13.imprint","IMPRINT",EDGE,{"disambiguationData":[TD([[subQ2,-1.0]])],"derivedFrom":subQ0}),1.0]])]});}
            extrude(context, id + "F26", {"entities" : qUnion([Q0, Q1]), "operationType" : NewBodyOperationType.REMOVE, "oppositeDirection" : true, "depth" : 4.5 * mm, "offsetDistance" : 25 * mm});
        }
        {
            var Q0;
            {var subQ7=sQuery(id+"F13.wireOp",EDGE,"E24.90.2");Q0=makeQuery(id+"F13.imprint","IMPRINT",FACE,{"disambiguationData":[TD([[makeQuery(id+"F13.imprint","IMPRINT",EDGE,{"derivedFrom":subQ7}),1.0]])]});}
            var Q1;
            {var subQ0=sQuery(id+"F13.wireOp",EDGE,"E24.90.8");var subQ1=makeQuery(id+"F8.opExtrude","CAP_EDGE",EDGE,{"disambiguationData":[OSD([sQuery(id+"F7.wireOp",EDGE,"E8")])],"isStart":true});var subQ2=makeQuery(id+"F13.imprint","INTERSECT",VERTEX,{"disambiguationData":[OD(0.0)],"derivedFrom":[subQ1,subQ0]});Q1=makeQuery(id+"F13.imprint","IMPRINT",FACE,{"disambiguationData":[TD([[makeQuery(id+"F13.imprint","IMPRINT",EDGE,{"disambiguationData":[TD([[subQ2,-1.0]])],"derivedFrom":subQ0}),1.0]])]});}
            extrude(context, id + "F27", {"entities" : qUnion([Q0, Q1]), "operationType" : NewBodyOperationType.REMOVE, "oppositeDirection" : true, "depth" : 4.5 * mm, "offsetDistance" : 25 * mm});
        }
        {
            var Q0;
            {var subQ5=sQuery(id+"F13.wireOp",EDGE,"E24.89.2");Q0=makeQuery(id+"F13.imprint","IMPRINT",FACE,{"disambiguationData":[TD([[makeQuery(id+"F13.imprint","IMPRINT",EDGE,{"derivedFrom":subQ5}),1.0]])]});}
            var Q1;
            {var subQ0=sQuery(id+"F13.wireOp",EDGE,"E24.89.8");var subQ1=makeQuery(id+"F8.opExtrude","CAP_EDGE",EDGE,{"disambiguationData":[OSD([sQuery(id+"F7.wireOp",EDGE,"E8")])],"isStart":true});var subQ2=makeQuery(id+"F13.imprint","INTERSECT",VERTEX,{"disambiguationData":[OD(0.0)],"derivedFrom":[subQ1,subQ0]});Q1=makeQuery(id+"F13.imprint","IMPRINT",FACE,{"disambiguationData":[TD([[makeQuery(id+"F13.imprint","IMPRINT",EDGE,{"disambiguationData":[TD([[subQ2,-1.0]])],"derivedFrom":subQ0}),1.0]])]});}
            extrude(context, id + "F28", {"entities" : qUnion([Q0, Q1]), "operationType" : NewBodyOperationType.REMOVE, "oppositeDirection" : true, "depth" : 4.5 * mm, "offsetDistance" : 25 * mm});
        }
        {
            var Q0;
            {var subQ7=sQuery(id+"F13.wireOp",EDGE,"E24.88.2");Q0=makeQuery(id+"F13.imprint","IMPRINT",FACE,{"disambiguationData":[TD([[makeQuery(id+"F13.imprint","IMPRINT",EDGE,{"derivedFrom":subQ7}),1.0]])]});}
            var Q1;
            {var subQ0=sQuery(id+"F13.wireOp",EDGE,"E24.88.8");var subQ1=makeQuery(id+"F8.opExtrude","CAP_EDGE",EDGE,{"disambiguationData":[OSD([sQuery(id+"F7.wireOp",EDGE,"E8")])],"isStart":true});var subQ2=makeQuery(id+"F13.imprint","INTERSECT",VERTEX,{"disambiguationData":[OD(0.0)],"derivedFrom":[subQ1,subQ0]});Q1=makeQuery(id+"F13.imprint","IMPRINT",FACE,{"disambiguationData":[TD([[makeQuery(id+"F13.imprint","IMPRINT",EDGE,{"disambiguationData":[TD([[subQ2,-1.0]])],"derivedFrom":subQ0}),1.0]])]});}
            extrude(context, id + "F29", {"entities" : qUnion([Q0, Q1]), "operationType" : NewBodyOperationType.REMOVE, "oppositeDirection" : true, "depth" : 4.5 * mm, "offsetDistance" : 25 * mm});
        }
        {
            var Q0;
            {var subQ7=sQuery(id+"F13.wireOp",EDGE,"E24.87.2");Q0=makeQuery(id+"F13.imprint","IMPRINT",FACE,{"disambiguationData":[TD([[makeQuery(id+"F13.imprint","IMPRINT",EDGE,{"derivedFrom":subQ7}),1.0]])]});}
            var Q1;
            {var subQ0=sQuery(id+"F13.wireOp",EDGE,"E24.87.8");var subQ1=makeQuery(id+"F8.opExtrude","CAP_EDGE",EDGE,{"disambiguationData":[OSD([sQuery(id+"F7.wireOp",EDGE,"E8")])],"isStart":true});var subQ2=makeQuery(id+"F13.imprint","INTERSECT",VERTEX,{"disambiguationData":[OD(0.0)],"derivedFrom":[subQ1,subQ0]});Q1=makeQuery(id+"F13.imprint","IMPRINT",FACE,{"disambiguationData":[TD([[makeQuery(id+"F13.imprint","IMPRINT",EDGE,{"disambiguationData":[TD([[subQ2,-1.0]])],"derivedFrom":subQ0}),1.0]])]});}
            extrude(context, id + "F30", {"entities" : qUnion([Q0, Q1]), "operationType" : NewBodyOperationType.REMOVE, "oppositeDirection" : true, "depth" : 4.5 * mm, "offsetDistance" : 25 * mm});
        }
        {
            var Q0;
            {var subQ5=sQuery(id+"F13.wireOp",EDGE,"E24.86.2");Q0=makeQuery(id+"F13.imprint","IMPRINT",FACE,{"disambiguationData":[TD([[makeQuery(id+"F13.imprint","IMPRINT",EDGE,{"derivedFrom":subQ5}),1.0]])]});}
            var Q1;
            {var subQ0=sQuery(id+"F13.wireOp",EDGE,"E24.86.8");var subQ1=makeQuery(id+"F8.opExtrude","CAP_EDGE",EDGE,{"disambiguationData":[OSD([sQuery(id+"F7.wireOp",EDGE,"E8")])],"isStart":true});var subQ2=makeQuery(id+"F13.imprint","INTERSECT",VERTEX,{"disambiguationData":[OD(0.0)],"derivedFrom":[subQ1,subQ0]});Q1=makeQuery(id+"F13.imprint","IMPRINT",FACE,{"disambiguationData":[TD([[makeQuery(id+"F13.imprint","IMPRINT",EDGE,{"disambiguationData":[TD([[subQ2,-1.0]])],"derivedFrom":subQ0}),1.0]])]});}
            extrude(context, id + "F31", {"entities" : qUnion([Q0, Q1]), "operationType" : NewBodyOperationType.REMOVE, "oppositeDirection" : true, "depth" : 4.5 * mm, "offsetDistance" : 25 * mm});
        }
        {
            var Q0;
            {var subQ7=sQuery(id+"F13.wireOp",EDGE,"E24.85.2");Q0=makeQuery(id+"F13.imprint","IMPRINT",FACE,{"disambiguationData":[TD([[makeQuery(id+"F13.imprint","IMPRINT",EDGE,{"derivedFrom":subQ7}),1.0]])]});}
            var Q1;
            {var subQ0=sQuery(id+"F13.wireOp",EDGE,"E24.85.8");var subQ1=makeQuery(id+"F8.opExtrude","CAP_EDGE",EDGE,{"disambiguationData":[OSD([sQuery(id+"F7.wireOp",EDGE,"E8")])],"isStart":true});var subQ2=makeQuery(id+"F13.imprint","INTERSECT",VERTEX,{"disambiguationData":[OD(0.0)],"derivedFrom":[subQ1,subQ0]});Q1=makeQuery(id+"F13.imprint","IMPRINT",FACE,{"disambiguationData":[TD([[makeQuery(id+"F13.imprint","IMPRINT",EDGE,{"disambiguationData":[TD([[subQ2,-1.0]])],"derivedFrom":subQ0}),1.0]])]});}
            extrude(context, id + "F32", {"entities" : qUnion([Q0, Q1]), "operationType" : NewBodyOperationType.REMOVE, "oppositeDirection" : true, "depth" : 4.5 * mm, "offsetDistance" : 25 * mm});
        }
        {
            var Q0;
            {var subQ5=sQuery(id+"F13.wireOp",EDGE,"E24.84.2");Q0=makeQuery(id+"F13.imprint","IMPRINT",FACE,{"disambiguationData":[TD([[makeQuery(id+"F13.imprint","IMPRINT",EDGE,{"derivedFrom":subQ5}),1.0]])]});}
            var Q1;
            {var subQ0=sQuery(id+"F13.wireOp",EDGE,"E24.84.8");var subQ1=makeQuery(id+"F8.opExtrude","CAP_EDGE",EDGE,{"disambiguationData":[OSD([sQuery(id+"F7.wireOp",EDGE,"E8")])],"isStart":true});var subQ2=makeQuery(id+"F13.imprint","INTERSECT",VERTEX,{"disambiguationData":[OD(0.0)],"derivedFrom":[subQ1,subQ0]});Q1=makeQuery(id+"F13.imprint","IMPRINT",FACE,{"disambiguationData":[TD([[makeQuery(id+"F13.imprint","IMPRINT",EDGE,{"disambiguationData":[TD([[subQ2,-1.0]])],"derivedFrom":subQ0}),1.0]])]});}
            extrude(context, id + "F33", {"entities" : qUnion([Q0, Q1]), "operationType" : NewBodyOperationType.REMOVE, "oppositeDirection" : true, "depth" : 4.5 * mm, "offsetDistance" : 25 * mm});
        }
        {
            var Q0;
            {var subQ0=sQuery(id+"F13.wireOp",EDGE,"E24.83.8");var subQ1=makeQuery(id+"F8.opExtrude","CAP_EDGE",EDGE,{"disambiguationData":[OSD([sQuery(id+"F7.wireOp",EDGE,"E8")])],"isStart":true});var subQ2=makeQuery(id+"F13.imprint","INTERSECT",VERTEX,{"disambiguationData":[OD(0.0)],"derivedFrom":[subQ1,subQ0]});Q0=makeQuery(id+"F13.imprint","IMPRINT",FACE,{"disambiguationData":[TD([[makeQuery(id+"F13.imprint","IMPRINT",EDGE,{"disambiguationData":[TD([[subQ2,-1.0]])],"derivedFrom":subQ0}),1.0]])]});}
            var Q1;
            {var subQ5=sQuery(id+"F13.wireOp",EDGE,"E24.83.2");Q1=makeQuery(id+"F13.imprint","IMPRINT",FACE,{"disambiguationData":[TD([[makeQuery(id+"F13.imprint","IMPRINT",EDGE,{"derivedFrom":subQ5}),1.0]])]});}
            extrude(context, id + "F34", {"entities" : qUnion([Q0, Q1]), "operationType" : NewBodyOperationType.REMOVE, "oppositeDirection" : true, "depth" : 4.5 * mm, "offsetDistance" : 25 * mm});
        }
        {
            var Q0;
            {var subQ7=sQuery(id+"F13.wireOp",EDGE,"E24.82.2");Q0=makeQuery(id+"F13.imprint","IMPRINT",FACE,{"disambiguationData":[TD([[makeQuery(id+"F13.imprint","IMPRINT",EDGE,{"derivedFrom":subQ7}),1.0]])]});}
            var Q1;
            {var subQ0=sQuery(id+"F13.wireOp",EDGE,"E24.82.8");var subQ1=makeQuery(id+"F8.opExtrude","CAP_EDGE",EDGE,{"disambiguationData":[OSD([sQuery(id+"F7.wireOp",EDGE,"E8")])],"isStart":true});var subQ2=makeQuery(id+"F13.imprint","INTERSECT",VERTEX,{"disambiguationData":[OD(0.0)],"derivedFrom":[subQ1,subQ0]});Q1=makeQuery(id+"F13.imprint","IMPRINT",FACE,{"disambiguationData":[TD([[makeQuery(id+"F13.imprint","IMPRINT",EDGE,{"disambiguationData":[TD([[subQ2,-1.0]])],"derivedFrom":subQ0}),1.0]])]});}
            extrude(context, id + "F35", {"entities" : qUnion([Q0, Q1]), "operationType" : NewBodyOperationType.REMOVE, "oppositeDirection" : true, "depth" : 4.5 * mm, "offsetDistance" : 25 * mm});
        }
        {
            var Q0;
            {var subQ0=sQuery(id+"F13.wireOp",EDGE,"E24.81.8");var subQ1=makeQuery(id+"F8.opExtrude","CAP_EDGE",EDGE,{"disambiguationData":[OSD([sQuery(id+"F7.wireOp",EDGE,"E8")])],"isStart":true});var subQ2=makeQuery(id+"F13.imprint","INTERSECT",VERTEX,{"disambiguationData":[OD(0.0)],"derivedFrom":[subQ1,subQ0]});Q0=makeQuery(id+"F13.imprint","IMPRINT",FACE,{"disambiguationData":[TD([[makeQuery(id+"F13.imprint","IMPRINT",EDGE,{"disambiguationData":[TD([[subQ2,-1.0]])],"derivedFrom":subQ0}),1.0]])]});}
            var Q1;
            {var subQ5=sQuery(id+"F13.wireOp",EDGE,"E24.81.2");Q1=makeQuery(id+"F13.imprint","IMPRINT",FACE,{"disambiguationData":[TD([[makeQuery(id+"F13.imprint","IMPRINT",EDGE,{"derivedFrom":subQ5}),1.0]])]});}
            extrude(context, id + "F36", {"entities" : qUnion([Q0, Q1]), "operationType" : NewBodyOperationType.REMOVE, "oppositeDirection" : true, "depth" : 4.5 * mm, "offsetDistance" : 25 * mm});
        }
        {
            var Q0;
            {var subQ7=sQuery(id+"F13.wireOp",EDGE,"E24.80.2");Q0=makeQuery(id+"F13.imprint","IMPRINT",FACE,{"disambiguationData":[TD([[makeQuery(id+"F13.imprint","IMPRINT",EDGE,{"derivedFrom":subQ7}),1.0]])]});}
            var Q1;
            {var subQ0=sQuery(id+"F13.wireOp",EDGE,"E24.80.8");var subQ1=makeQuery(id+"F8.opExtrude","CAP_EDGE",EDGE,{"disambiguationData":[OSD([sQuery(id+"F7.wireOp",EDGE,"E8")])],"isStart":true});var subQ2=makeQuery(id+"F13.imprint","INTERSECT",VERTEX,{"disambiguationData":[OD(0.0)],"derivedFrom":[subQ1,subQ0]});Q1=makeQuery(id+"F13.imprint","IMPRINT",FACE,{"disambiguationData":[TD([[makeQuery(id+"F13.imprint","IMPRINT",EDGE,{"disambiguationData":[TD([[subQ2,-1.0]])],"derivedFrom":subQ0}),1.0]])]});}
            extrude(context, id + "F37", {"entities" : qUnion([Q0, Q1]), "operationType" : NewBodyOperationType.REMOVE, "oppositeDirection" : true, "depth" : 4.5 * mm, "offsetDistance" : 25 * mm});
        }
        {
            var Q0;
            {var subQ7=sQuery(id+"F13.wireOp",EDGE,"E24.79.2");Q0=makeQuery(id+"F13.imprint","IMPRINT",FACE,{"disambiguationData":[TD([[makeQuery(id+"F13.imprint","IMPRINT",EDGE,{"derivedFrom":subQ7}),1.0]])]});}
            var Q1;
            {var subQ0=sQuery(id+"F13.wireOp",EDGE,"E24.79.8");var subQ1=makeQuery(id+"F8.opExtrude","CAP_EDGE",EDGE,{"disambiguationData":[OSD([sQuery(id+"F7.wireOp",EDGE,"E8")])],"isStart":true});var subQ2=makeQuery(id+"F13.imprint","INTERSECT",VERTEX,{"disambiguationData":[OD(0.0)],"derivedFrom":[subQ1,subQ0]});Q1=makeQuery(id+"F13.imprint","IMPRINT",FACE,{"disambiguationData":[TD([[makeQuery(id+"F13.imprint","IMPRINT",EDGE,{"disambiguationData":[TD([[subQ2,-1.0]])],"derivedFrom":subQ0}),1.0]])]});}
            extrude(context, id + "F38", {"entities" : qUnion([Q0, Q1]), "operationType" : NewBodyOperationType.REMOVE, "oppositeDirection" : true, "depth" : 4.5 * mm, "offsetDistance" : 25 * mm});
        }
        {
            var Q0;
            {var subQ5=sQuery(id+"F13.wireOp",EDGE,"E24.78.2");Q0=makeQuery(id+"F13.imprint","IMPRINT",FACE,{"disambiguationData":[TD([[makeQuery(id+"F13.imprint","IMPRINT",EDGE,{"derivedFrom":subQ5}),1.0]])]});}
            var Q1;
            {var subQ0=sQuery(id+"F13.wireOp",EDGE,"E24.78.8");var subQ1=makeQuery(id+"F8.opExtrude","CAP_EDGE",EDGE,{"disambiguationData":[OSD([sQuery(id+"F7.wireOp",EDGE,"E8")])],"isStart":true});var subQ2=makeQuery(id+"F13.imprint","INTERSECT",VERTEX,{"disambiguationData":[OD(0.0)],"derivedFrom":[subQ1,subQ0]});Q1=makeQuery(id+"F13.imprint","IMPRINT",FACE,{"disambiguationData":[TD([[makeQuery(id+"F13.imprint","IMPRINT",EDGE,{"disambiguationData":[TD([[subQ2,-1.0]])],"derivedFrom":subQ0}),1.0]])]});}
            extrude(context, id + "F39", {"entities" : qUnion([Q0, Q1]), "operationType" : NewBodyOperationType.REMOVE, "oppositeDirection" : true, "depth" : 4.5 * mm, "offsetDistance" : 25 * mm});
        }
        {
            var Q0;
            {var subQ7=sQuery(id+"F13.wireOp",EDGE,"E24.77.2");Q0=makeQuery(id+"F13.imprint","IMPRINT",FACE,{"disambiguationData":[TD([[makeQuery(id+"F13.imprint","IMPRINT",EDGE,{"derivedFrom":subQ7}),1.0]])]});}
            var Q1;
            {var subQ0=sQuery(id+"F13.wireOp",EDGE,"E24.77.8");var subQ1=makeQuery(id+"F8.opExtrude","CAP_EDGE",EDGE,{"disambiguationData":[OSD([sQuery(id+"F7.wireOp",EDGE,"E8")])],"isStart":true});var subQ2=makeQuery(id+"F13.imprint","INTERSECT",VERTEX,{"disambiguationData":[OD(0.0)],"derivedFrom":[subQ1,subQ0]});Q1=makeQuery(id+"F13.imprint","IMPRINT",FACE,{"disambiguationData":[TD([[makeQuery(id+"F13.imprint","IMPRINT",EDGE,{"disambiguationData":[TD([[subQ2,-1.0]])],"derivedFrom":subQ0}),1.0]])]});}
            extrude(context, id + "F40", {"entities" : qUnion([Q0, Q1]), "operationType" : NewBodyOperationType.REMOVE, "oppositeDirection" : true, "depth" : 4.5 * mm, "offsetDistance" : 25 * mm});
        }
        {
            var Q0;
            {var subQ7=sQuery(id+"F13.wireOp",EDGE,"E24.76.2");Q0=makeQuery(id+"F13.imprint","IMPRINT",FACE,{"disambiguationData":[TD([[makeQuery(id+"F13.imprint","IMPRINT",EDGE,{"derivedFrom":subQ7}),1.0]])]});}
            var Q1;
            {var subQ0=sQuery(id+"F13.wireOp",EDGE,"E24.76.8");var subQ1=makeQuery(id+"F8.opExtrude","CAP_EDGE",EDGE,{"disambiguationData":[OSD([sQuery(id+"F7.wireOp",EDGE,"E8")])],"isStart":true});var subQ2=makeQuery(id+"F13.imprint","INTERSECT",VERTEX,{"disambiguationData":[OD(0.0)],"derivedFrom":[subQ1,subQ0]});Q1=makeQuery(id+"F13.imprint","IMPRINT",FACE,{"disambiguationData":[TD([[makeQuery(id+"F13.imprint","IMPRINT",EDGE,{"disambiguationData":[TD([[subQ2,-1.0]])],"derivedFrom":subQ0}),1.0]])]});}
            extrude(context, id + "F41", {"entities" : qUnion([Q0, Q1]), "operationType" : NewBodyOperationType.REMOVE, "oppositeDirection" : true, "depth" : 4.5 * mm, "offsetDistance" : 25 * mm});
        }
        {
            var Q0;
            {var subQ5=sQuery(id+"F13.wireOp",EDGE,"E24.75.2");Q0=makeQuery(id+"F13.imprint","IMPRINT",FACE,{"disambiguationData":[TD([[makeQuery(id+"F13.imprint","IMPRINT",EDGE,{"derivedFrom":subQ5}),1.0]])]});}
            var Q1;
            {var subQ0=sQuery(id+"F13.wireOp",EDGE,"E24.75.8");var subQ1=makeQuery(id+"F8.opExtrude","CAP_EDGE",EDGE,{"disambiguationData":[OSD([sQuery(id+"F7.wireOp",EDGE,"E8")])],"isStart":true});var subQ2=makeQuery(id+"F13.imprint","INTERSECT",VERTEX,{"disambiguationData":[OD(0.0)],"derivedFrom":[subQ1,subQ0]});Q1=makeQuery(id+"F13.imprint","IMPRINT",FACE,{"disambiguationData":[TD([[makeQuery(id+"F13.imprint","IMPRINT",EDGE,{"disambiguationData":[TD([[subQ2,-1.0]])],"derivedFrom":subQ0}),1.0]])]});}
            extrude(context, id + "F42", {"entities" : qUnion([Q0, Q1]), "operationType" : NewBodyOperationType.REMOVE, "oppositeDirection" : true, "depth" : 4.5 * mm, "offsetDistance" : 25 * mm});
        }
        {
            var Q0;
            {var subQ7=sQuery(id+"F13.wireOp",EDGE,"E24.74.2");Q0=makeQuery(id+"F13.imprint","IMPRINT",FACE,{"disambiguationData":[TD([[makeQuery(id+"F13.imprint","IMPRINT",EDGE,{"derivedFrom":subQ7}),1.0]])]});}
            var Q1;
            {var subQ0=sQuery(id+"F13.wireOp",EDGE,"E24.74.8");var subQ1=makeQuery(id+"F8.opExtrude","CAP_EDGE",EDGE,{"disambiguationData":[OSD([sQuery(id+"F7.wireOp",EDGE,"E8")])],"isStart":true});var subQ2=makeQuery(id+"F13.imprint","INTERSECT",VERTEX,{"disambiguationData":[OD(0.0)],"derivedFrom":[subQ1,subQ0]});Q1=makeQuery(id+"F13.imprint","IMPRINT",FACE,{"disambiguationData":[TD([[makeQuery(id+"F13.imprint","IMPRINT",EDGE,{"disambiguationData":[TD([[subQ2,-1.0]])],"derivedFrom":subQ0}),1.0]])]});}
            extrude(context, id + "F43", {"entities" : qUnion([Q0, Q1]), "operationType" : NewBodyOperationType.REMOVE, "oppositeDirection" : true, "depth" : 4.5 * mm, "offsetDistance" : 25 * mm});
        }
        {
            var Q0;
            {var subQ5=sQuery(id+"F13.wireOp",EDGE,"E24.73.2");Q0=makeQuery(id+"F13.imprint","IMPRINT",FACE,{"disambiguationData":[TD([[makeQuery(id+"F13.imprint","IMPRINT",EDGE,{"derivedFrom":subQ5}),1.0]])]});}
            var Q1;
            {var subQ0=sQuery(id+"F13.wireOp",EDGE,"E24.73.8");var subQ1=makeQuery(id+"F8.opExtrude","CAP_EDGE",EDGE,{"disambiguationData":[OSD([sQuery(id+"F7.wireOp",EDGE,"E8")])],"isStart":true});var subQ2=makeQuery(id+"F13.imprint","INTERSECT",VERTEX,{"disambiguationData":[OD(0.0)],"derivedFrom":[subQ1,subQ0]});Q1=makeQuery(id+"F13.imprint","IMPRINT",FACE,{"disambiguationData":[TD([[makeQuery(id+"F13.imprint","IMPRINT",EDGE,{"disambiguationData":[TD([[subQ2,-1.0]])],"derivedFrom":subQ0}),1.0]])]});}
            extrude(context, id + "F44", {"entities" : qUnion([Q0, Q1]), "operationType" : NewBodyOperationType.REMOVE, "oppositeDirection" : true, "depth" : 4.5 * mm, "offsetDistance" : 25 * mm});
        }
        {
            var Q0;
            {var subQ5=sQuery(id+"F13.wireOp",EDGE,"E24.72.2");Q0=makeQuery(id+"F13.imprint","IMPRINT",FACE,{"disambiguationData":[TD([[makeQuery(id+"F13.imprint","IMPRINT",EDGE,{"derivedFrom":subQ5}),1.0]])]});}
            var Q1;
            {var subQ0=sQuery(id+"F13.wireOp",EDGE,"E24.72.8");var subQ1=makeQuery(id+"F8.opExtrude","CAP_EDGE",EDGE,{"disambiguationData":[OSD([sQuery(id+"F7.wireOp",EDGE,"E8")])],"isStart":true});var subQ2=makeQuery(id+"F13.imprint","INTERSECT",VERTEX,{"disambiguationData":[OD(0.0)],"derivedFrom":[subQ1,subQ0]});Q1=makeQuery(id+"F13.imprint","IMPRINT",FACE,{"disambiguationData":[TD([[makeQuery(id+"F13.imprint","IMPRINT",EDGE,{"disambiguationData":[TD([[subQ2,-1.0]])],"derivedFrom":subQ0}),1.0]])]});}
            extrude(context, id + "F45", {"entities" : qUnion([Q0, Q1]), "operationType" : NewBodyOperationType.REMOVE, "oppositeDirection" : true, "depth" : 4.5 * mm, "offsetDistance" : 25 * mm});
        }
        {
            var Q0;
            {var subQ7=sQuery(id+"F13.wireOp",EDGE,"E24.71.2");Q0=makeQuery(id+"F13.imprint","IMPRINT",FACE,{"disambiguationData":[TD([[makeQuery(id+"F13.imprint","IMPRINT",EDGE,{"derivedFrom":subQ7}),1.0]])]});}
            var Q1;
            {var subQ0=sQuery(id+"F13.wireOp",EDGE,"E24.71.8");var subQ1=makeQuery(id+"F8.opExtrude","CAP_EDGE",EDGE,{"disambiguationData":[OSD([sQuery(id+"F7.wireOp",EDGE,"E8")])],"isStart":true});var subQ2=makeQuery(id+"F13.imprint","INTERSECT",VERTEX,{"disambiguationData":[OD(0.0)],"derivedFrom":[subQ1,subQ0]});Q1=makeQuery(id+"F13.imprint","IMPRINT",FACE,{"disambiguationData":[TD([[makeQuery(id+"F13.imprint","IMPRINT",EDGE,{"disambiguationData":[TD([[subQ2,-1.0]])],"derivedFrom":subQ0}),1.0]])]});}
            extrude(context, id + "F46", {"entities" : qUnion([Q0, Q1]), "operationType" : NewBodyOperationType.REMOVE, "oppositeDirection" : true, "depth" : 4.5 * mm, "offsetDistance" : 25 * mm});
        }
        {
            var Q0;
            {var subQ5=sQuery(id+"F13.wireOp",EDGE,"E24.70.2");Q0=makeQuery(id+"F13.imprint","IMPRINT",FACE,{"disambiguationData":[TD([[makeQuery(id+"F13.imprint","IMPRINT",EDGE,{"derivedFrom":subQ5}),1.0]])]});}
            var Q1;
            {var subQ0=sQuery(id+"F13.wireOp",EDGE,"E24.70.8");var subQ1=makeQuery(id+"F8.opExtrude","CAP_EDGE",EDGE,{"disambiguationData":[OSD([sQuery(id+"F7.wireOp",EDGE,"E8")])],"isStart":true});var subQ2=makeQuery(id+"F13.imprint","INTERSECT",VERTEX,{"disambiguationData":[OD(0.0)],"derivedFrom":[subQ1,subQ0]});Q1=makeQuery(id+"F13.imprint","IMPRINT",FACE,{"disambiguationData":[TD([[makeQuery(id+"F13.imprint","IMPRINT",EDGE,{"disambiguationData":[TD([[subQ2,-1.0]])],"derivedFrom":subQ0}),1.0]])]});}
            extrude(context, id + "F47", {"entities" : qUnion([Q0, Q1]), "operationType" : NewBodyOperationType.REMOVE, "oppositeDirection" : true, "depth" : 25 * mm, "offsetDistance" : 25 * mm});
        }
        {
            var Q0;
            {var subQ7=sQuery(id+"F13.wireOp",EDGE,"E24.69.2");Q0=makeQuery(id+"F13.imprint","IMPRINT",FACE,{"disambiguationData":[TD([[makeQuery(id+"F13.imprint","IMPRINT",EDGE,{"derivedFrom":subQ7}),1.0]])]});}
            var Q1;
            {var subQ0=sQuery(id+"F13.wireOp",EDGE,"E24.69.8");var subQ1=makeQuery(id+"F8.opExtrude","CAP_EDGE",EDGE,{"disambiguationData":[OSD([sQuery(id+"F7.wireOp",EDGE,"E8")])],"isStart":true});var subQ2=makeQuery(id+"F13.imprint","INTERSECT",VERTEX,{"disambiguationData":[OD(0.0)],"derivedFrom":[subQ1,subQ0]});Q1=makeQuery(id+"F13.imprint","IMPRINT",FACE,{"disambiguationData":[TD([[makeQuery(id+"F13.imprint","IMPRINT",EDGE,{"disambiguationData":[TD([[subQ2,-1.0]])],"derivedFrom":subQ0}),1.0]])]});}
            extrude(context, id + "F48", {"entities" : qUnion([Q0, Q1]), "operationType" : NewBodyOperationType.REMOVE, "oppositeDirection" : true, "depth" : 4.5 * mm, "offsetDistance" : 25 * mm});
        }
        {
            var Q0;
            {var subQ7=sQuery(id+"F13.wireOp",EDGE,"E24.68.2");Q0=makeQuery(id+"F13.imprint","IMPRINT",FACE,{"disambiguationData":[TD([[makeQuery(id+"F13.imprint","IMPRINT",EDGE,{"derivedFrom":subQ7}),1.0]])]});}
            var Q1;
            {var subQ0=sQuery(id+"F13.wireOp",EDGE,"E24.68.8");var subQ1=makeQuery(id+"F8.opExtrude","CAP_EDGE",EDGE,{"disambiguationData":[OSD([sQuery(id+"F7.wireOp",EDGE,"E8")])],"isStart":true});var subQ2=makeQuery(id+"F13.imprint","INTERSECT",VERTEX,{"disambiguationData":[OD(0.0)],"derivedFrom":[subQ1,subQ0]});Q1=makeQuery(id+"F13.imprint","IMPRINT",FACE,{"disambiguationData":[TD([[makeQuery(id+"F13.imprint","IMPRINT",EDGE,{"disambiguationData":[TD([[subQ2,-1.0]])],"derivedFrom":subQ0}),1.0]])]});}
            extrude(context, id + "F49", {"entities" : qUnion([Q0, Q1]), "operationType" : NewBodyOperationType.REMOVE, "oppositeDirection" : true, "depth" : 4.5 * mm, "offsetDistance" : 25 * mm});
        }
        {
            var Q0;
            {var subQ5=sQuery(id+"F13.wireOp",EDGE,"E24.67.2");Q0=makeQuery(id+"F13.imprint","IMPRINT",FACE,{"disambiguationData":[TD([[makeQuery(id+"F13.imprint","IMPRINT",EDGE,{"derivedFrom":subQ5}),1.0]])]});}
            var Q1;
            {var subQ0=sQuery(id+"F13.wireOp",EDGE,"E24.67.8");var subQ1=makeQuery(id+"F8.opExtrude","CAP_EDGE",EDGE,{"disambiguationData":[OSD([sQuery(id+"F7.wireOp",EDGE,"E8")])],"isStart":true});var subQ2=makeQuery(id+"F13.imprint","INTERSECT",VERTEX,{"disambiguationData":[OD(0.0)],"derivedFrom":[subQ1,subQ0]});Q1=makeQuery(id+"F13.imprint","IMPRINT",FACE,{"disambiguationData":[TD([[makeQuery(id+"F13.imprint","IMPRINT",EDGE,{"disambiguationData":[TD([[subQ2,-1.0]])],"derivedFrom":subQ0}),1.0]])]});}
            extrude(context, id + "F50", {"entities" : qUnion([Q0, Q1]), "operationType" : NewBodyOperationType.REMOVE, "oppositeDirection" : true, "depth" : 4.5 * mm, "offsetDistance" : 25 * mm});
        }
        {
            var Q0;
            {var subQ7=sQuery(id+"F13.wireOp",EDGE,"E24.66.2");Q0=makeQuery(id+"F13.imprint","IMPRINT",FACE,{"disambiguationData":[TD([[makeQuery(id+"F13.imprint","IMPRINT",EDGE,{"derivedFrom":subQ7}),1.0]])]});}
            var Q1;
            {var subQ0=sQuery(id+"F13.wireOp",EDGE,"E24.66.8");var subQ1=makeQuery(id+"F8.opExtrude","CAP_EDGE",EDGE,{"disambiguationData":[OSD([sQuery(id+"F7.wireOp",EDGE,"E8")])],"isStart":true});var subQ2=makeQuery(id+"F13.imprint","INTERSECT",VERTEX,{"disambiguationData":[OD(0.0)],"derivedFrom":[subQ1,subQ0]});Q1=makeQuery(id+"F13.imprint","IMPRINT",FACE,{"disambiguationData":[TD([[makeQuery(id+"F13.imprint","IMPRINT",EDGE,{"disambiguationData":[TD([[subQ2,-1.0]])],"derivedFrom":subQ0}),1.0]])]});}
            extrude(context, id + "F51", {"entities" : qUnion([Q0, Q1]), "operationType" : NewBodyOperationType.REMOVE, "oppositeDirection" : true, "depth" : 4.5 * mm, "offsetDistance" : 25 * mm});
        }
        {
            var Q0;
            {var subQ7=sQuery(id+"F13.wireOp",EDGE,"E24.65.2");Q0=makeQuery(id+"F13.imprint","IMPRINT",FACE,{"disambiguationData":[TD([[makeQuery(id+"F13.imprint","IMPRINT",EDGE,{"derivedFrom":subQ7}),1.0]])]});}
            var Q1;
            {var subQ0=sQuery(id+"F13.wireOp",EDGE,"E24.65.8");var subQ1=makeQuery(id+"F8.opExtrude","CAP_EDGE",EDGE,{"disambiguationData":[OSD([sQuery(id+"F7.wireOp",EDGE,"E8")])],"isStart":true});var subQ2=makeQuery(id+"F13.imprint","INTERSECT",VERTEX,{"disambiguationData":[OD(0.0)],"derivedFrom":[subQ1,subQ0]});Q1=makeQuery(id+"F13.imprint","IMPRINT",FACE,{"disambiguationData":[TD([[makeQuery(id+"F13.imprint","IMPRINT",EDGE,{"disambiguationData":[TD([[subQ2,-1.0]])],"derivedFrom":subQ0}),1.0]])]});}
            extrude(context, id + "F52", {"entities" : qUnion([Q0, Q1]), "operationType" : NewBodyOperationType.REMOVE, "oppositeDirection" : true, "depth" : 4.5 * mm, "offsetDistance" : 25 * mm});
        }
        {
            var Q0;
            {var subQ5=sQuery(id+"F13.wireOp",EDGE,"E24.64.2");Q0=makeQuery(id+"F13.imprint","IMPRINT",FACE,{"disambiguationData":[TD([[makeQuery(id+"F13.imprint","IMPRINT",EDGE,{"derivedFrom":subQ5}),1.0]])]});}
            var Q1;
            {var subQ0=sQuery(id+"F13.wireOp",EDGE,"E24.64.8");var subQ1=makeQuery(id+"F8.opExtrude","CAP_EDGE",EDGE,{"disambiguationData":[OSD([sQuery(id+"F7.wireOp",EDGE,"E8")])],"isStart":true});var subQ2=makeQuery(id+"F13.imprint","INTERSECT",VERTEX,{"disambiguationData":[OD(0.0)],"derivedFrom":[subQ1,subQ0]});Q1=makeQuery(id+"F13.imprint","IMPRINT",FACE,{"disambiguationData":[TD([[makeQuery(id+"F13.imprint","IMPRINT",EDGE,{"disambiguationData":[TD([[subQ2,-1.0]])],"derivedFrom":subQ0}),1.0]])]});}
            extrude(context, id + "F53", {"entities" : qUnion([Q0, Q1]), "operationType" : NewBodyOperationType.REMOVE, "oppositeDirection" : true, "depth" : 4.5 * mm, "offsetDistance" : 25 * mm});
        }
        {
            var Q0;
            {var subQ7=sQuery(id+"F13.wireOp",EDGE,"E24.63.2");Q0=makeQuery(id+"F13.imprint","IMPRINT",FACE,{"disambiguationData":[TD([[makeQuery(id+"F13.imprint","IMPRINT",EDGE,{"derivedFrom":subQ7}),1.0]])]});}
            var Q1;
            {var subQ0=sQuery(id+"F13.wireOp",EDGE,"E24.63.8");var subQ1=makeQuery(id+"F8.opExtrude","CAP_EDGE",EDGE,{"disambiguationData":[OSD([sQuery(id+"F7.wireOp",EDGE,"E8")])],"isStart":true});var subQ2=makeQuery(id+"F13.imprint","INTERSECT",VERTEX,{"disambiguationData":[OD(0.0)],"derivedFrom":[subQ1,subQ0]});Q1=makeQuery(id+"F13.imprint","IMPRINT",FACE,{"disambiguationData":[TD([[makeQuery(id+"F13.imprint","IMPRINT",EDGE,{"disambiguationData":[TD([[subQ2,-1.0]])],"derivedFrom":subQ0}),1.0]])]});}
            extrude(context, id + "F54", {"entities" : qUnion([Q0, Q1]), "operationType" : NewBodyOperationType.REMOVE, "oppositeDirection" : true, "depth" : 4.5 * mm, "offsetDistance" : 25 * mm});
        }
        {
            var Q0;
            {var subQ5=sQuery(id+"F13.wireOp",EDGE,"E24.62.2");Q0=makeQuery(id+"F13.imprint","IMPRINT",FACE,{"disambiguationData":[TD([[makeQuery(id+"F13.imprint","IMPRINT",EDGE,{"derivedFrom":subQ5}),1.0]])]});}
            var Q1;
            {var subQ0=sQuery(id+"F13.wireOp",EDGE,"E24.62.8");var subQ1=makeQuery(id+"F8.opExtrude","CAP_EDGE",EDGE,{"disambiguationData":[OSD([sQuery(id+"F7.wireOp",EDGE,"E8")])],"isStart":true});var subQ2=makeQuery(id+"F13.imprint","INTERSECT",VERTEX,{"disambiguationData":[OD(0.0)],"derivedFrom":[subQ1,subQ0]});Q1=makeQuery(id+"F13.imprint","IMPRINT",FACE,{"disambiguationData":[TD([[makeQuery(id+"F13.imprint","IMPRINT",EDGE,{"disambiguationData":[TD([[subQ2,-1.0]])],"derivedFrom":subQ0}),1.0]])]});}
            extrude(context, id + "F55", {"entities" : qUnion([Q0, Q1]), "operationType" : NewBodyOperationType.REMOVE, "oppositeDirection" : true, "depth" : 4.5 * mm, "offsetDistance" : 25 * mm});
        }
        {
            var Q0;
            {var subQ5=sQuery(id+"F13.wireOp",EDGE,"E24.61.2");Q0=makeQuery(id+"F13.imprint","IMPRINT",FACE,{"disambiguationData":[TD([[makeQuery(id+"F13.imprint","IMPRINT",EDGE,{"derivedFrom":subQ5}),1.0]])]});}
            var Q1;
            {var subQ0=sQuery(id+"F13.wireOp",EDGE,"E24.61.8");var subQ1=makeQuery(id+"F8.opExtrude","CAP_EDGE",EDGE,{"disambiguationData":[OSD([sQuery(id+"F7.wireOp",EDGE,"E8")])],"isStart":true});var subQ2=makeQuery(id+"F13.imprint","INTERSECT",VERTEX,{"disambiguationData":[OD(0.0)],"derivedFrom":[subQ1,subQ0]});Q1=makeQuery(id+"F13.imprint","IMPRINT",FACE,{"disambiguationData":[TD([[makeQuery(id+"F13.imprint","IMPRINT",EDGE,{"disambiguationData":[TD([[subQ2,-1.0]])],"derivedFrom":subQ0}),1.0]])]});}
            extrude(context, id + "F56", {"entities" : qUnion([Q0, Q1]), "operationType" : NewBodyOperationType.REMOVE, "oppositeDirection" : true, "depth" : 4.5 * mm, "offsetDistance" : 25 * mm});
        }
        {
            var Q0;
            {var subQ7=sQuery(id+"F13.wireOp",EDGE,"E24.60.2");Q0=makeQuery(id+"F13.imprint","IMPRINT",FACE,{"disambiguationData":[TD([[makeQuery(id+"F13.imprint","IMPRINT",EDGE,{"derivedFrom":subQ7}),1.0]])]});}
            var Q1;
            {var subQ0=sQuery(id+"F13.wireOp",EDGE,"E24.60.8");var subQ1=makeQuery(id+"F8.opExtrude","CAP_EDGE",EDGE,{"disambiguationData":[OSD([sQuery(id+"F7.wireOp",EDGE,"E8")])],"isStart":true});var subQ2=makeQuery(id+"F13.imprint","INTERSECT",VERTEX,{"disambiguationData":[OD(0.0)],"derivedFrom":[subQ1,subQ0]});Q1=makeQuery(id+"F13.imprint","IMPRINT",FACE,{"disambiguationData":[TD([[makeQuery(id+"F13.imprint","IMPRINT",EDGE,{"disambiguationData":[TD([[subQ2,-1.0]])],"derivedFrom":subQ0}),1.0]])]});}
            extrude(context, id + "F57", {"entities" : qUnion([Q0, Q1]), "operationType" : NewBodyOperationType.REMOVE, "oppositeDirection" : true, "depth" : 4.5 * mm, "offsetDistance" : 25 * mm});
        }
        {
            var Q0;
            {var subQ5=sQuery(id+"F13.wireOp",EDGE,"E24.59.2");Q0=makeQuery(id+"F13.imprint","IMPRINT",FACE,{"disambiguationData":[TD([[makeQuery(id+"F13.imprint","IMPRINT",EDGE,{"derivedFrom":subQ5}),1.0]])]});}
            var Q1;
            {var subQ0=sQuery(id+"F13.wireOp",EDGE,"E24.59.8");var subQ1=makeQuery(id+"F8.opExtrude","CAP_EDGE",EDGE,{"disambiguationData":[OSD([sQuery(id+"F7.wireOp",EDGE,"E8")])],"isStart":true});var subQ2=makeQuery(id+"F13.imprint","INTERSECT",VERTEX,{"disambiguationData":[OD(0.0)],"derivedFrom":[subQ1,subQ0]});Q1=makeQuery(id+"F13.imprint","IMPRINT",FACE,{"disambiguationData":[TD([[makeQuery(id+"F13.imprint","IMPRINT",EDGE,{"disambiguationData":[TD([[subQ2,-1.0]])],"derivedFrom":subQ0}),1.0]])]});}
            extrude(context, id + "F58", {"entities" : qUnion([Q0, Q1]), "operationType" : NewBodyOperationType.REMOVE, "oppositeDirection" : true, "depth" : 4.5 * mm, "offsetDistance" : 25 * mm});
        }
        {
            var Q0;
            {var subQ7=sQuery(id+"F13.wireOp",EDGE,"E24.58.2");Q0=makeQuery(id+"F13.imprint","IMPRINT",FACE,{"disambiguationData":[TD([[makeQuery(id+"F13.imprint","IMPRINT",EDGE,{"derivedFrom":subQ7}),1.0]])]});}
            var Q1;
            {var subQ0=sQuery(id+"F13.wireOp",EDGE,"E24.58.8");var subQ1=makeQuery(id+"F8.opExtrude","CAP_EDGE",EDGE,{"disambiguationData":[OSD([sQuery(id+"F7.wireOp",EDGE,"E8")])],"isStart":true});var subQ2=makeQuery(id+"F13.imprint","INTERSECT",VERTEX,{"disambiguationData":[OD(0.0)],"derivedFrom":[subQ1,subQ0]});Q1=makeQuery(id+"F13.imprint","IMPRINT",FACE,{"disambiguationData":[TD([[makeQuery(id+"F13.imprint","IMPRINT",EDGE,{"disambiguationData":[TD([[subQ2,-1.0]])],"derivedFrom":subQ0}),1.0]])]});}
            extrude(context, id + "F59", {"entities" : qUnion([Q0, Q1]), "operationType" : NewBodyOperationType.REMOVE, "oppositeDirection" : true, "depth" : 4.5 * mm, "offsetDistance" : 25 * mm});
        }
        {
            var Q0;
            {var subQ7=sQuery(id+"F13.wireOp",EDGE,"E24.57.2");Q0=makeQuery(id+"F13.imprint","IMPRINT",FACE,{"disambiguationData":[TD([[makeQuery(id+"F13.imprint","IMPRINT",EDGE,{"derivedFrom":subQ7}),1.0]])]});}
            var Q1;
            {var subQ0=sQuery(id+"F13.wireOp",EDGE,"E24.57.8");var subQ1=makeQuery(id+"F8.opExtrude","CAP_EDGE",EDGE,{"disambiguationData":[OSD([sQuery(id+"F7.wireOp",EDGE,"E8")])],"isStart":true});var subQ2=makeQuery(id+"F13.imprint","INTERSECT",VERTEX,{"disambiguationData":[OD(0.0)],"derivedFrom":[subQ1,subQ0]});Q1=makeQuery(id+"F13.imprint","IMPRINT",FACE,{"disambiguationData":[TD([[makeQuery(id+"F13.imprint","IMPRINT",EDGE,{"disambiguationData":[TD([[subQ2,-1.0]])],"derivedFrom":subQ0}),1.0]])]});}
            extrude(context, id + "F60", {"entities" : qUnion([Q0, Q1]), "operationType" : NewBodyOperationType.REMOVE, "oppositeDirection" : true, "depth" : 4.5 * mm, "offsetDistance" : 25 * mm});
        }
        {
            var Q0;
            {var subQ5=sQuery(id+"F13.wireOp",EDGE,"E24.56.2");Q0=makeQuery(id+"F13.imprint","IMPRINT",FACE,{"disambiguationData":[TD([[makeQuery(id+"F13.imprint","IMPRINT",EDGE,{"derivedFrom":subQ5}),1.0]])]});}
            var Q1;
            {var subQ0=sQuery(id+"F13.wireOp",EDGE,"E24.56.8");var subQ1=makeQuery(id+"F8.opExtrude","CAP_EDGE",EDGE,{"disambiguationData":[OSD([sQuery(id+"F7.wireOp",EDGE,"E8")])],"isStart":true});var subQ2=makeQuery(id+"F13.imprint","INTERSECT",VERTEX,{"disambiguationData":[OD(0.0)],"derivedFrom":[subQ1,subQ0]});Q1=makeQuery(id+"F13.imprint","IMPRINT",FACE,{"disambiguationData":[TD([[makeQuery(id+"F13.imprint","IMPRINT",EDGE,{"disambiguationData":[TD([[subQ2,-1.0]])],"derivedFrom":subQ0}),1.0]])]});}
            extrude(context, id + "F61", {"entities" : qUnion([Q0, Q1]), "operationType" : NewBodyOperationType.REMOVE, "oppositeDirection" : true, "depth" : 4.5 * mm, "offsetDistance" : 25 * mm});
        }
        {
            var Q0;
            {var subQ7=sQuery(id+"F13.wireOp",EDGE,"E24.55.2");Q0=makeQuery(id+"F13.imprint","IMPRINT",FACE,{"disambiguationData":[TD([[makeQuery(id+"F13.imprint","IMPRINT",EDGE,{"derivedFrom":subQ7}),1.0]])]});}
            var Q1;
            {var subQ0=sQuery(id+"F13.wireOp",EDGE,"E24.55.8");var subQ1=makeQuery(id+"F8.opExtrude","CAP_EDGE",EDGE,{"disambiguationData":[OSD([sQuery(id+"F7.wireOp",EDGE,"E8")])],"isStart":true});var subQ2=makeQuery(id+"F13.imprint","INTERSECT",VERTEX,{"disambiguationData":[OD(0.0)],"derivedFrom":[subQ1,subQ0]});Q1=makeQuery(id+"F13.imprint","IMPRINT",FACE,{"disambiguationData":[TD([[makeQuery(id+"F13.imprint","IMPRINT",EDGE,{"disambiguationData":[TD([[subQ2,-1.0]])],"derivedFrom":subQ0}),1.0]])]});}
            extrude(context, id + "F62", {"entities" : qUnion([Q0, Q1]), "operationType" : NewBodyOperationType.REMOVE, "oppositeDirection" : true, "depth" : 4.5 * mm, "offsetDistance" : 25 * mm});
        }
        {
            var Q0;
            {var subQ7=sQuery(id+"F13.wireOp",EDGE,"E24.54.2");Q0=makeQuery(id+"F13.imprint","IMPRINT",FACE,{"disambiguationData":[TD([[makeQuery(id+"F13.imprint","IMPRINT",EDGE,{"derivedFrom":subQ7}),1.0]])]});}
            var Q1;
            {var subQ0=sQuery(id+"F13.wireOp",EDGE,"E24.54.8");var subQ1=makeQuery(id+"F8.opExtrude","CAP_EDGE",EDGE,{"disambiguationData":[OSD([sQuery(id+"F7.wireOp",EDGE,"E8")])],"isStart":true});var subQ2=makeQuery(id+"F13.imprint","INTERSECT",VERTEX,{"disambiguationData":[OD(0.0)],"derivedFrom":[subQ1,subQ0]});Q1=makeQuery(id+"F13.imprint","IMPRINT",FACE,{"disambiguationData":[TD([[makeQuery(id+"F13.imprint","IMPRINT",EDGE,{"disambiguationData":[TD([[subQ2,-1.0]])],"derivedFrom":subQ0}),1.0]])]});}
            extrude(context, id + "F63", {"entities" : qUnion([Q0, Q1]), "operationType" : NewBodyOperationType.REMOVE, "oppositeDirection" : true, "depth" : 4.5 * mm, "offsetDistance" : 25 * mm});
        }
        {
            var Q0;
            {var subQ5=sQuery(id+"F13.wireOp",EDGE,"E24.53.2");Q0=makeQuery(id+"F13.imprint","IMPRINT",FACE,{"disambiguationData":[TD([[makeQuery(id+"F13.imprint","IMPRINT",EDGE,{"derivedFrom":subQ5}),1.0]])]});}
            var Q1;
            {var subQ0=sQuery(id+"F13.wireOp",EDGE,"E24.53.8");var subQ1=makeQuery(id+"F8.opExtrude","CAP_EDGE",EDGE,{"disambiguationData":[OSD([sQuery(id+"F7.wireOp",EDGE,"E8")])],"isStart":true});var subQ2=makeQuery(id+"F13.imprint","INTERSECT",VERTEX,{"disambiguationData":[OD(0.0)],"derivedFrom":[subQ1,subQ0]});Q1=makeQuery(id+"F13.imprint","IMPRINT",FACE,{"disambiguationData":[TD([[makeQuery(id+"F13.imprint","IMPRINT",EDGE,{"disambiguationData":[TD([[subQ2,-1.0]])],"derivedFrom":subQ0}),1.0]])]});}
            extrude(context, id + "F64", {"entities" : qUnion([Q0, Q1]), "operationType" : NewBodyOperationType.REMOVE, "oppositeDirection" : true, "depth" : 4.5 * mm, "offsetDistance" : 25 * mm});
        }
        {
            var Q0;
            {var subQ7=sQuery(id+"F13.wireOp",EDGE,"E24.52.2");Q0=makeQuery(id+"F13.imprint","IMPRINT",FACE,{"disambiguationData":[TD([[makeQuery(id+"F13.imprint","IMPRINT",EDGE,{"derivedFrom":subQ7}),1.0]])]});}
            var Q1;
            {var subQ0=sQuery(id+"F13.wireOp",EDGE,"E24.52.8");var subQ1=makeQuery(id+"F8.opExtrude","CAP_EDGE",EDGE,{"disambiguationData":[OSD([sQuery(id+"F7.wireOp",EDGE,"E8")])],"isStart":true});var subQ2=makeQuery(id+"F13.imprint","INTERSECT",VERTEX,{"disambiguationData":[OD(0.0)],"derivedFrom":[subQ1,subQ0]});Q1=makeQuery(id+"F13.imprint","IMPRINT",FACE,{"disambiguationData":[TD([[makeQuery(id+"F13.imprint","IMPRINT",EDGE,{"disambiguationData":[TD([[subQ2,-1.0]])],"derivedFrom":subQ0}),1.0]])]});}
            extrude(context, id + "F65", {"entities" : qUnion([Q0, Q1]), "operationType" : NewBodyOperationType.REMOVE, "oppositeDirection" : true, "depth" : 4.5 * mm, "offsetDistance" : 25 * mm});
        }
        {
            var Q0;
            {var subQ5=sQuery(id+"F13.wireOp",EDGE,"E24.51.2");Q0=makeQuery(id+"F13.imprint","IMPRINT",FACE,{"disambiguationData":[TD([[makeQuery(id+"F13.imprint","IMPRINT",EDGE,{"derivedFrom":subQ5}),1.0]])]});}
            var Q1;
            {var subQ0=sQuery(id+"F13.wireOp",EDGE,"E24.51.8");var subQ1=makeQuery(id+"F8.opExtrude","CAP_EDGE",EDGE,{"disambiguationData":[OSD([sQuery(id+"F7.wireOp",EDGE,"E8")])],"isStart":true});var subQ2=makeQuery(id+"F13.imprint","INTERSECT",VERTEX,{"disambiguationData":[OD(0.0)],"derivedFrom":[subQ1,subQ0]});Q1=makeQuery(id+"F13.imprint","IMPRINT",FACE,{"disambiguationData":[TD([[makeQuery(id+"F13.imprint","IMPRINT",EDGE,{"disambiguationData":[TD([[subQ2,-1.0]])],"derivedFrom":subQ0}),1.0]])]});}
            extrude(context, id + "F66", {"entities" : qUnion([Q0, Q1]), "operationType" : NewBodyOperationType.REMOVE, "oppositeDirection" : true, "depth" : 4.5 * mm, "offsetDistance" : 25 * mm});
        }
        {
            var Q0;
            {var subQ5=sQuery(id+"F13.wireOp",EDGE,"E24.50.2");Q0=makeQuery(id+"F13.imprint","IMPRINT",FACE,{"disambiguationData":[TD([[makeQuery(id+"F13.imprint","IMPRINT",EDGE,{"derivedFrom":subQ5}),1.0]])]});}
            var Q1;
            {var subQ0=sQuery(id+"F13.wireOp",EDGE,"E24.50.8");var subQ1=makeQuery(id+"F8.opExtrude","CAP_EDGE",EDGE,{"disambiguationData":[OSD([sQuery(id+"F7.wireOp",EDGE,"E8")])],"isStart":true});var subQ2=makeQuery(id+"F13.imprint","INTERSECT",VERTEX,{"disambiguationData":[OD(0.0)],"derivedFrom":[subQ1,subQ0]});Q1=makeQuery(id+"F13.imprint","IMPRINT",FACE,{"disambiguationData":[TD([[makeQuery(id+"F13.imprint","IMPRINT",EDGE,{"disambiguationData":[TD([[subQ2,-1.0]])],"derivedFrom":subQ0}),1.0]])]});}
            extrude(context, id + "F67", {"entities" : qUnion([Q0, Q1]), "operationType" : NewBodyOperationType.REMOVE, "oppositeDirection" : true, "depth" : 4.5 * mm, "offsetDistance" : 25 * mm});
        }
        {
            var Q0;
            {var subQ7=sQuery(id+"F13.wireOp",EDGE,"E24.49.2");Q0=makeQuery(id+"F13.imprint","IMPRINT",FACE,{"disambiguationData":[TD([[makeQuery(id+"F13.imprint","IMPRINT",EDGE,{"derivedFrom":subQ7}),1.0]])]});}
            var Q1;
            {var subQ0=sQuery(id+"F13.wireOp",EDGE,"E24.49.8");var subQ1=makeQuery(id+"F8.opExtrude","CAP_EDGE",EDGE,{"disambiguationData":[OSD([sQuery(id+"F7.wireOp",EDGE,"E8")])],"isStart":true});var subQ2=makeQuery(id+"F13.imprint","INTERSECT",VERTEX,{"disambiguationData":[OD(0.0)],"derivedFrom":[subQ1,subQ0]});Q1=makeQuery(id+"F13.imprint","IMPRINT",FACE,{"disambiguationData":[TD([[makeQuery(id+"F13.imprint","IMPRINT",EDGE,{"disambiguationData":[TD([[subQ2,-1.0]])],"derivedFrom":subQ0}),1.0]])]});}
            extrude(context, id + "F68", {"entities" : qUnion([Q0, Q1]), "operationType" : NewBodyOperationType.REMOVE, "oppositeDirection" : true, "depth" : 4.5 * mm, "offsetDistance" : 25 * mm});
        }
        {
            var Q0;
            {var subQ5=sQuery(id+"F13.wireOp",EDGE,"E24.48.2");Q0=makeQuery(id+"F13.imprint","IMPRINT",FACE,{"disambiguationData":[TD([[makeQuery(id+"F13.imprint","IMPRINT",EDGE,{"derivedFrom":subQ5}),1.0]])]});}
            var Q1;
            {var subQ0=sQuery(id+"F13.wireOp",EDGE,"E24.48.8");var subQ1=makeQuery(id+"F8.opExtrude","CAP_EDGE",EDGE,{"disambiguationData":[OSD([sQuery(id+"F7.wireOp",EDGE,"E8")])],"isStart":true});var subQ2=makeQuery(id+"F13.imprint","INTERSECT",VERTEX,{"disambiguationData":[OD(0.0)],"derivedFrom":[subQ1,subQ0]});Q1=makeQuery(id+"F13.imprint","IMPRINT",FACE,{"disambiguationData":[TD([[makeQuery(id+"F13.imprint","IMPRINT",EDGE,{"disambiguationData":[TD([[subQ2,-1.0]])],"derivedFrom":subQ0}),1.0]])]});}
            extrude(context, id + "F69", {"entities" : qUnion([Q0, Q1]), "operationType" : NewBodyOperationType.REMOVE, "oppositeDirection" : true, "depth" : 4.5 * mm, "offsetDistance" : 25 * mm});
        }
        {
            var Q0;
            {var subQ0=sQuery(id+"F13.wireOp",EDGE,"E24.47.8");var subQ1=makeQuery(id+"F8.opExtrude","CAP_EDGE",EDGE,{"disambiguationData":[OSD([sQuery(id+"F7.wireOp",EDGE,"E8")])],"isStart":true});var subQ2=makeQuery(id+"F13.imprint","INTERSECT",VERTEX,{"disambiguationData":[OD(0.0)],"derivedFrom":[subQ1,subQ0]});Q0=makeQuery(id+"F13.imprint","IMPRINT",FACE,{"disambiguationData":[TD([[makeQuery(id+"F13.imprint","IMPRINT",EDGE,{"disambiguationData":[TD([[subQ2,-1.0]])],"derivedFrom":subQ0}),1.0]])]});}
            var Q1;
            {var subQ7=sQuery(id+"F13.wireOp",EDGE,"E24.47.2");Q1=makeQuery(id+"F13.imprint","IMPRINT",FACE,{"disambiguationData":[TD([[makeQuery(id+"F13.imprint","IMPRINT",EDGE,{"derivedFrom":subQ7}),1.0]])]});}
            extrude(context, id + "F70", {"entities" : qUnion([Q0, Q1]), "operationType" : NewBodyOperationType.REMOVE, "oppositeDirection" : true, "depth" : 4.5 * mm, "offsetDistance" : 25 * mm});
        }
        {
            var Q0;
            {var subQ7=sQuery(id+"F13.wireOp",EDGE,"E24.46.2");Q0=makeQuery(id+"F13.imprint","IMPRINT",FACE,{"disambiguationData":[TD([[makeQuery(id+"F13.imprint","IMPRINT",EDGE,{"derivedFrom":subQ7}),1.0]])]});}
            var Q1;
            {var subQ0=sQuery(id+"F13.wireOp",EDGE,"E24.46.8");var subQ1=makeQuery(id+"F8.opExtrude","CAP_EDGE",EDGE,{"disambiguationData":[OSD([sQuery(id+"F7.wireOp",EDGE,"E8")])],"isStart":true});var subQ2=makeQuery(id+"F13.imprint","INTERSECT",VERTEX,{"disambiguationData":[OD(0.0)],"derivedFrom":[subQ1,subQ0]});Q1=makeQuery(id+"F13.imprint","IMPRINT",FACE,{"disambiguationData":[TD([[makeQuery(id+"F13.imprint","IMPRINT",EDGE,{"disambiguationData":[TD([[subQ2,-1.0]])],"derivedFrom":subQ0}),1.0]])]});}
            extrude(context, id + "F71", {"entities" : qUnion([Q0, Q1]), "operationType" : NewBodyOperationType.REMOVE, "oppositeDirection" : true, "depth" : 4.5 * mm, "offsetDistance" : 25 * mm});
        }
        {
            var Q0;
            {var subQ0=sQuery(id+"F7.wireOp",EDGE,"E8");var subQ2=makeQuery(id+"F14.boolean.opBoolean","COPY",FACE,{"derivedFrom":makeQuery(id+"F14.opExtrude","SWEPT_FACE",FACE,{"disambiguationData":[OSD([sQuery(id+"F13.wireOp",EDGE,"E19.filletArc")])]})});Q0=makeQuery(id+"F71.boolean.opBoolean","SPLIT",EDGE,{"disambiguationData":[TD([subQ2])],"derivedFrom":makeQuery(id+"F70.boolean.opBoolean","SPLIT",EDGE,{"disambiguationData":[TD([subQ2])],"derivedFrom":makeQuery(id+"F69.boolean.opBoolean","SPLIT",EDGE,{"disambiguationData":[TD([subQ2])],"derivedFrom":makeQuery(id+"F68.boolean.opBoolean","SPLIT",EDGE,{"disambiguationData":[TD([subQ2])],"derivedFrom":makeQuery(id+"F67.boolean.opBoolean","SPLIT",EDGE,{"disambiguationData":[TD([subQ2])],"derivedFrom":makeQuery(id+"F66.boolean.opBoolean","SPLIT",EDGE,{"disambiguationData":[TD([subQ2])],"derivedFrom":makeQuery(id+"F65.boolean.opBoolean","SPLIT",EDGE,{"disambiguationData":[TD([subQ2])],"derivedFrom":makeQuery(id+"F64.boolean.opBoolean","SPLIT",EDGE,{"disambiguationData":[TD([subQ2])],"derivedFrom":makeQuery(id+"F63.boolean.opBoolean","SPLIT",EDGE,{"disambiguationData":[TD([subQ2])],"derivedFrom":makeQuery(id+"F62.boolean.opBoolean","SPLIT",EDGE,{"disambiguationData":[TD([subQ2])],"derivedFrom":makeQuery(id+"F61.boolean.opBoolean","SPLIT",EDGE,{"disambiguationData":[TD([subQ2])],"derivedFrom":makeQuery(id+"F60.boolean.opBoolean","SPLIT",EDGE,{"disambiguationData":[TD([subQ2])],"derivedFrom":makeQuery(id+"F59.boolean.opBoolean","SPLIT",EDGE,{"disambiguationData":[TD([subQ2])],"derivedFrom":makeQuery(id+"F58.boolean.opBoolean","SPLIT",EDGE,{"disambiguationData":[TD([subQ2])],"derivedFrom":makeQuery(id+"F57.boolean.opBoolean","SPLIT",EDGE,{"disambiguationData":[TD([subQ2])],"derivedFrom":makeQuery(id+"F56.boolean.opBoolean","SPLIT",EDGE,{"disambiguationData":[TD([subQ2])],"derivedFrom":makeQuery(id+"F55.boolean.opBoolean","SPLIT",EDGE,{"disambiguationData":[TD([subQ2])],"derivedFrom":makeQuery(id+"F54.boolean.opBoolean","SPLIT",EDGE,{"disambiguationData":[TD([subQ2])],"derivedFrom":makeQuery(id+"F53.boolean.opBoolean","SPLIT",EDGE,{"disambiguationData":[TD([subQ2])],"derivedFrom":makeQuery(id+"F52.boolean.opBoolean","SPLIT",EDGE,{"disambiguationData":[TD([subQ2])],"derivedFrom":makeQuery(id+"F51.boolean.opBoolean","SPLIT",EDGE,{"disambiguationData":[TD([subQ2])],"derivedFrom":makeQuery(id+"F50.boolean.opBoolean","SPLIT",EDGE,{"disambiguationData":[TD([subQ2])],"derivedFrom":makeQuery(id+"F49.boolean.opBoolean","SPLIT",EDGE,{"disambiguationData":[TD([subQ2])],"derivedFrom":makeQuery(id+"F48.boolean.opBoolean","SPLIT",EDGE,{"disambiguationData":[TD([subQ2])],"derivedFrom":makeQuery(id+"F47.boolean.opBoolean","SPLIT",EDGE,{"disambiguationData":[TD([subQ2])],"derivedFrom":makeQuery(id+"F46.boolean.opBoolean","SPLIT",EDGE,{"disambiguationData":[TD([subQ2])],"derivedFrom":makeQuery(id+"F45.boolean.opBoolean","SPLIT",EDGE,{"disambiguationData":[TD([subQ2])],"derivedFrom":makeQuery(id+"F44.boolean.opBoolean","SPLIT",EDGE,{"disambiguationData":[TD([subQ2])],"derivedFrom":makeQuery(id+"F43.boolean.opBoolean","SPLIT",EDGE,{"disambiguationData":[TD([subQ2])],"derivedFrom":makeQuery(id+"F42.boolean.opBoolean","SPLIT",EDGE,{"disambiguationData":[TD([subQ2])],"derivedFrom":makeQuery(id+"F41.boolean.opBoolean","SPLIT",EDGE,{"disambiguationData":[TD([subQ2])],"derivedFrom":makeQuery(id+"F40.boolean.opBoolean","SPLIT",EDGE,{"disambiguationData":[TD([subQ2])],"derivedFrom":makeQuery(id+"F39.boolean.opBoolean","SPLIT",EDGE,{"disambiguationData":[TD([subQ2])],"derivedFrom":makeQuery(id+"F38.boolean.opBoolean","SPLIT",EDGE,{"disambiguationData":[TD([subQ2])],"derivedFrom":makeQuery(id+"F37.boolean.opBoolean","SPLIT",EDGE,{"disambiguationData":[TD([subQ2])],"derivedFrom":makeQuery(id+"F36.boolean.opBoolean","SPLIT",EDGE,{"disambiguationData":[TD([subQ2])],"derivedFrom":makeQuery(id+"F35.boolean.opBoolean","SPLIT",EDGE,{"disambiguationData":[TD([subQ2])],"derivedFrom":makeQuery(id+"F34.boolean.opBoolean","SPLIT",EDGE,{"disambiguationData":[TD([subQ2])],"derivedFrom":makeQuery(id+"F33.boolean.opBoolean","SPLIT",EDGE,{"disambiguationData":[TD([subQ2])],"derivedFrom":makeQuery(id+"F32.boolean.opBoolean","SPLIT",EDGE,{"disambiguationData":[TD([subQ2])],"derivedFrom":makeQuery(id+"F31.boolean.opBoolean","SPLIT",EDGE,{"disambiguationData":[TD([subQ2])],"derivedFrom":makeQuery(id+"F30.boolean.opBoolean","SPLIT",EDGE,{"disambiguationData":[TD([subQ2])],"derivedFrom":makeQuery(id+"F29.boolean.opBoolean","SPLIT",EDGE,{"disambiguationData":[TD([subQ2])],"derivedFrom":makeQuery(id+"F28.boolean.opBoolean","SPLIT",EDGE,{"disambiguationData":[TD([subQ2])],"derivedFrom":makeQuery(id+"F27.boolean.opBoolean","SPLIT",EDGE,{"disambiguationData":[TD([subQ2])],"derivedFrom":makeQuery(id+"F26.boolean.opBoolean","SPLIT",EDGE,{"disambiguationData":[TD([subQ2])],"derivedFrom":makeQuery(id+"F25.boolean.opBoolean","SPLIT",EDGE,{"disambiguationData":[TD([subQ2])],"derivedFrom":makeQuery(id+"F24.boolean.opBoolean","SPLIT",EDGE,{"disambiguationData":[TD([subQ2])],"derivedFrom":makeQuery(id+"F23.boolean.opBoolean","SPLIT",EDGE,{"disambiguationData":[TD([subQ2])],"derivedFrom":makeQuery(id+"F22.boolean.opBoolean","SPLIT",EDGE,{"disambiguationData":[TD([subQ2])],"derivedFrom":makeQuery(id+"F21.boolean.opBoolean","SPLIT",EDGE,{"disambiguationData":[TD([subQ2])],"derivedFrom":makeQuery(id+"F20.boolean.opBoolean","SPLIT",EDGE,{"disambiguationData":[TD([subQ2])],"derivedFrom":makeQuery(id+"F19.boolean.opBoolean","SPLIT",EDGE,{"disambiguationData":[TD([subQ2])],"derivedFrom":makeQuery(id+"F18.boolean.opBoolean","SPLIT",EDGE,{"disambiguationData":[TD([subQ2])],"derivedFrom":makeQuery(id+"F17.boolean.opBoolean","SPLIT",EDGE,{"disambiguationData":[TD([subQ2])],"derivedFrom":makeQuery(id+"F16.boolean.opBoolean","SPLIT",EDGE,{"disambiguationData":[TD([subQ2])],"derivedFrom":makeQuery(id+"F15.boolean.opBoolean","SPLIT",EDGE,{"disambiguationData":[TD([subQ2])],"derivedFrom":makeQuery(id+"F8.opExtrude","CAP_EDGE",EDGE,{"disambiguationData":[OSD([subQ0])],"isStart":false})})})})})})})})})})})})})})})})})})})})})})})})})})})})})})})})})})})})})})})})})})})})})})})})})})})})})})})})})});}
            chamfer(context, id + "F72", {"entities" : qUnion([Q0]), "chamferType" : ChamferType.TWO_OFFSETS, "width1" : 2.5 * mm, "oppositeDirection" : false, "width2" : 1.8 * mm, "tangentPropagation" : true});
        }
        {
            var Q0;
            Q0=makeQuery(id+"F11.opExtrude","CAP_FACE",FACE,{"disambiguationData":[OSD([sQuery(id+"F9.wireOp",EDGE,"E10"),sQuery(id+"F9.wireOp",EDGE,"E11")])],"isStart":false});
            var sketch = newSketch(context, id + "F73", { "sketchPlane" : qUnion([Q0])});
            skCircle(sketch, "E25", {"center": v(11.48, 0) * mm, "radius": 51 * mm});
            skSolve(sketch);
        }
        {
            var Q0;
            Q0=makeQuery(id+"F73.imprint","IMPRINT",FACE,{"disambiguationData":[TD([[makeQuery(id+"F73.imprint","IMPRINT",EDGE,{"derivedFrom":sQuery(id+"F73.wireOp",EDGE,"E25")}),1.0]])]});
            extrude(context, id + "F74", {"entities" : qUnion([Q0]), "operationType" : NewBodyOperationType.ADD, "oppositeDirection" : true, "depth" : 2 * mm, "offsetDistance" : 25 * mm});
        }
        {
            var Q0;
            {var subQ0=sQuery(id+"F9.wireOp",EDGE,"E11");var subQ1=sQuery(id+"F9.wireOp",EDGE,"E10");Q0=makeQuery(id+"F74.boolean.opBoolean","MERGE",FACE,{"derivedFrom":[makeQuery(id+"F11.opExtrude","CAP_FACE",FACE,{"disambiguationData":[OSD([subQ1,subQ0])],"isStart":false}),makeQuery(id+"F74.opExtrude","CAP_FACE",FACE,{"disambiguationData":[OSD([subQ1,subQ0,sQuery(id+"F73.wireOp",EDGE,"E25")])],"isStart":true})]});}
            var sketch = newSketch(context, id + "F75", { "sketchPlane" : qUnion([Q0])});
            skLineSegment(sketch, "E26", {"start": v(11.48, 0) * mm, "end": v(-38.52, 0) * mm});
            skLineSegment(sketch, "E27", {"start": v(11.48, 0) * mm, "end": v(2.62, 50.23) * mm});
            skLineSegment(sketch, "E28", {"start": v(11.48, 0) * mm, "end": v(20.34, 50.23) * mm});
            skLineSegment(sketch, "E29", {"start": v(11.48, 0) * mm, "end": v(61.7, -8.86) * mm});
            skLineSegment(sketch, "E30", {"start": v(11.48, 0) * mm, "end": v(36.98, -44.17) * mm});
            skLineSegment(sketch, "E31", {"start": v(11.48, 0) * mm, "end": v(-38.74, -8.86) * mm});
            skLineSegment(sketch, "E32", {"start": v(11.48, 0) * mm, "end": v(-14.02, -44.17) * mm});
            skCircle(sketch, "E33", {"center": v(11.48, 0) * mm, "radius": 50 * mm});
            skCircle(sketch, "E34", {"center": v(11.48, 0) * mm, "radius": 51 * mm});
            skSolve(sketch);
        }
        {
            var Q0;
            {var subQ2=sQuery(id+"F75.wireOp",EDGE,"E27");var subQ6=sQuery(id+"F75.wireOp",EDGE,"E34");var subQ8=makeQuery(id+"F75.imprint","INTERSECT",VERTEX,{"derivedFrom":[subQ2,subQ6]});Q0=makeQuery(id+"F75.imprint","IMPRINT",FACE,{"disambiguationData":[TD([[makeQuery(id+"F75.imprint","IMPRINT",EDGE,{"disambiguationData":[TD([[subQ8,1.0]])],"derivedFrom":subQ2}),1.0]])]});}
            var Q1;
            {var subQ0=sQuery(id+"F75.wireOp",EDGE,"E34");var subQ1=sQuery(id+"F75.wireOp",EDGE,"E28");var subQ2=makeQuery(id+"F75.imprint","INTERSECT",VERTEX,{"derivedFrom":[subQ1,subQ0]});Q1=makeQuery(id+"F75.imprint","IMPRINT",FACE,{"disambiguationData":[TD([[makeQuery(id+"F75.imprint","IMPRINT",EDGE,{"disambiguationData":[TD([[subQ2,1.0]])],"derivedFrom":subQ1}),-1.0]])]});}
            var Q2;
            {var subQ0=sQuery(id+"F75.wireOp",EDGE,"E34");var subQ1=sQuery(id+"F75.wireOp",EDGE,"E30");var subQ2=makeQuery(id+"F75.imprint","INTERSECT",VERTEX,{"derivedFrom":[subQ1,subQ0]});Q2=makeQuery(id+"F75.imprint","IMPRINT",FACE,{"disambiguationData":[TD([[makeQuery(id+"F75.imprint","IMPRINT",EDGE,{"disambiguationData":[TD([[subQ2,1.0]])],"derivedFrom":subQ1}),-1.0]])]});}
            extrude(context, id + "F76", {"entities" : qUnion([Q0, Q1, Q2]), "operationType" : NewBodyOperationType.REMOVE, "oppositeDirection" : true, "depth" : 2 * mm, "offsetDistance" : 25 * mm});
        }
        {
            var Q0;
            {var subQ0=makeQuery(id+"F14.boolean.opBoolean","COPY",FACE,{"derivedFrom":makeQuery(id+"F14.opExtrude","SWEPT_FACE",FACE,{"disambiguationData":[OSD([sQuery(id+"F13.wireOp",EDGE,"E19.filletArc")])]})});var subQ1=sQuery(id+"F7.wireOp",EDGE,"E8");Q0=makeQuery(id+"F71.boolean.opBoolean","SPLIT",FACE,{"disambiguationData":[TD([subQ0])],"derivedFrom":makeQuery(id+"F70.boolean.opBoolean","SPLIT",FACE,{"disambiguationData":[TD([subQ0])],"derivedFrom":makeQuery(id+"F69.boolean.opBoolean","SPLIT",FACE,{"disambiguationData":[TD([subQ0])],"derivedFrom":makeQuery(id+"F68.boolean.opBoolean","SPLIT",FACE,{"disambiguationData":[TD([subQ0])],"derivedFrom":makeQuery(id+"F67.boolean.opBoolean","SPLIT",FACE,{"disambiguationData":[TD([subQ0])],"derivedFrom":makeQuery(id+"F66.boolean.opBoolean","SPLIT",FACE,{"disambiguationData":[TD([subQ0])],"derivedFrom":makeQuery(id+"F65.boolean.opBoolean","SPLIT",FACE,{"disambiguationData":[TD([subQ0])],"derivedFrom":makeQuery(id+"F64.boolean.opBoolean","SPLIT",FACE,{"disambiguationData":[TD([subQ0])],"derivedFrom":makeQuery(id+"F63.boolean.opBoolean","SPLIT",FACE,{"disambiguationData":[TD([subQ0])],"derivedFrom":makeQuery(id+"F62.boolean.opBoolean","SPLIT",FACE,{"disambiguationData":[TD([subQ0])],"derivedFrom":makeQuery(id+"F61.boolean.opBoolean","SPLIT",FACE,{"disambiguationData":[TD([subQ0])],"derivedFrom":makeQuery(id+"F60.boolean.opBoolean","SPLIT",FACE,{"disambiguationData":[TD([subQ0])],"derivedFrom":makeQuery(id+"F59.boolean.opBoolean","SPLIT",FACE,{"disambiguationData":[TD([subQ0])],"derivedFrom":makeQuery(id+"F58.boolean.opBoolean","SPLIT",FACE,{"disambiguationData":[TD([subQ0])],"derivedFrom":makeQuery(id+"F57.boolean.opBoolean","SPLIT",FACE,{"disambiguationData":[TD([subQ0])],"derivedFrom":makeQuery(id+"F56.boolean.opBoolean","SPLIT",FACE,{"disambiguationData":[TD([subQ0])],"derivedFrom":makeQuery(id+"F55.boolean.opBoolean","SPLIT",FACE,{"disambiguationData":[TD([subQ0])],"derivedFrom":makeQuery(id+"F54.boolean.opBoolean","SPLIT",FACE,{"disambiguationData":[TD([subQ0])],"derivedFrom":makeQuery(id+"F53.boolean.opBoolean","SPLIT",FACE,{"disambiguationData":[TD([subQ0])],"derivedFrom":makeQuery(id+"F52.boolean.opBoolean","SPLIT",FACE,{"disambiguationData":[TD([subQ0])],"derivedFrom":makeQuery(id+"F51.boolean.opBoolean","SPLIT",FACE,{"disambiguationData":[TD([subQ0])],"derivedFrom":makeQuery(id+"F50.boolean.opBoolean","SPLIT",FACE,{"disambiguationData":[TD([subQ0])],"derivedFrom":makeQuery(id+"F49.boolean.opBoolean","SPLIT",FACE,{"disambiguationData":[TD([subQ0])],"derivedFrom":makeQuery(id+"F48.boolean.opBoolean","SPLIT",FACE,{"disambiguationData":[TD([subQ0])],"derivedFrom":makeQuery(id+"F47.boolean.opBoolean","SPLIT",FACE,{"disambiguationData":[TD([subQ0])],"derivedFrom":makeQuery(id+"F46.boolean.opBoolean","SPLIT",FACE,{"disambiguationData":[TD([subQ0])],"derivedFrom":makeQuery(id+"F45.boolean.opBoolean","SPLIT",FACE,{"disambiguationData":[TD([subQ0])],"derivedFrom":makeQuery(id+"F44.boolean.opBoolean","SPLIT",FACE,{"disambiguationData":[TD([subQ0])],"derivedFrom":makeQuery(id+"F43.boolean.opBoolean","SPLIT",FACE,{"disambiguationData":[TD([subQ0])],"derivedFrom":makeQuery(id+"F42.boolean.opBoolean","SPLIT",FACE,{"disambiguationData":[TD([subQ0])],"derivedFrom":makeQuery(id+"F41.boolean.opBoolean","SPLIT",FACE,{"disambiguationData":[TD([subQ0])],"derivedFrom":makeQuery(id+"F40.boolean.opBoolean","SPLIT",FACE,{"disambiguationData":[TD([subQ0])],"derivedFrom":makeQuery(id+"F39.boolean.opBoolean","SPLIT",FACE,{"disambiguationData":[TD([subQ0])],"derivedFrom":makeQuery(id+"F38.boolean.opBoolean","SPLIT",FACE,{"disambiguationData":[TD([subQ0])],"derivedFrom":makeQuery(id+"F37.boolean.opBoolean","SPLIT",FACE,{"disambiguationData":[TD([subQ0])],"derivedFrom":makeQuery(id+"F36.boolean.opBoolean","SPLIT",FACE,{"disambiguationData":[TD([subQ0])],"derivedFrom":makeQuery(id+"F35.boolean.opBoolean","SPLIT",FACE,{"disambiguationData":[TD([subQ0])],"derivedFrom":makeQuery(id+"F34.boolean.opBoolean","SPLIT",FACE,{"disambiguationData":[TD([subQ0])],"derivedFrom":makeQuery(id+"F33.boolean.opBoolean","SPLIT",FACE,{"disambiguationData":[TD([subQ0])],"derivedFrom":makeQuery(id+"F32.boolean.opBoolean","SPLIT",FACE,{"disambiguationData":[TD([subQ0])],"derivedFrom":makeQuery(id+"F31.boolean.opBoolean","SPLIT",FACE,{"disambiguationData":[TD([subQ0])],"derivedFrom":makeQuery(id+"F30.boolean.opBoolean","SPLIT",FACE,{"disambiguationData":[TD([subQ0])],"derivedFrom":makeQuery(id+"F29.boolean.opBoolean","SPLIT",FACE,{"disambiguationData":[TD([subQ0])],"derivedFrom":makeQuery(id+"F28.boolean.opBoolean","SPLIT",FACE,{"disambiguationData":[TD([subQ0])],"derivedFrom":makeQuery(id+"F27.boolean.opBoolean","SPLIT",FACE,{"disambiguationData":[TD([subQ0])],"derivedFrom":makeQuery(id+"F26.boolean.opBoolean","SPLIT",FACE,{"disambiguationData":[TD([subQ0])],"derivedFrom":makeQuery(id+"F25.boolean.opBoolean","SPLIT",FACE,{"disambiguationData":[TD([subQ0])],"derivedFrom":makeQuery(id+"F24.boolean.opBoolean","SPLIT",FACE,{"disambiguationData":[TD([subQ0])],"derivedFrom":makeQuery(id+"F23.boolean.opBoolean","SPLIT",FACE,{"disambiguationData":[TD([subQ0])],"derivedFrom":makeQuery(id+"F22.boolean.opBoolean","SPLIT",FACE,{"disambiguationData":[TD([subQ0])],"derivedFrom":makeQuery(id+"F21.boolean.opBoolean","SPLIT",FACE,{"disambiguationData":[TD([subQ0])],"derivedFrom":makeQuery(id+"F20.boolean.opBoolean","SPLIT",FACE,{"disambiguationData":[TD([subQ0])],"derivedFrom":makeQuery(id+"F19.boolean.opBoolean","SPLIT",FACE,{"disambiguationData":[TD([subQ0])],"derivedFrom":makeQuery(id+"F18.boolean.opBoolean","SPLIT",FACE,{"disambiguationData":[TD([subQ0])],"derivedFrom":makeQuery(id+"F17.boolean.opBoolean","SPLIT",FACE,{"disambiguationData":[TD([subQ0])],"derivedFrom":makeQuery(id+"F16.boolean.opBoolean","SPLIT",FACE,{"disambiguationData":[TD([subQ0])],"derivedFrom":makeQuery(id+"F15.boolean.opBoolean","SPLIT",FACE,{"disambiguationData":[TD([subQ0])],"derivedFrom":makeQuery(id+"F8.opExtrude","SWEPT_FACE",FACE,{"disambiguationData":[OSD([subQ1])]})})})})})})})})})})})})})})})})})})})})})})})})})})})})})})})})})})})})})})})})})})})})})})})})})})})})})})})})})});}
            cPlane(context, id + "F77", {"entities" : qUnion([Q0]), "cplaneType" : CPlaneType.LINE_ANGLE, "offset" : 25 * mm, "angle" : 0 * degree, "width" : 150 * mm, "height" : 150 * mm});
        }
        {
            var Q0;
            Q0=qCreatedBy(id+"F77.planeOp",FACE);
            var sketch = newSketch(context, id + "F78", { "sketchPlane" : qUnion([Q0])});
            skLineSegment(sketch, "E35", {"start": v(0, 0) * mm, "end": v(0, 30) * mm});
            skLineSegment(sketch, "E36", {"start": v(0, 30) * mm, "end": v(46.2, 10.87) * mm});
            skLineSegment(sketch, "E37", {"start": v(46.2, 10.87) * mm, "end": v(47.12, 10.48) * mm});
            skLineSegment(sketch, "E38", {"start": v(47.12, 10.48) * mm, "end": v(47.88, 12.33) * mm});
            skLineSegment(sketch, "E39", {"start": v(47.88, 12.33) * mm, "end": v(46.2, 10.87) * mm});
            skSolve(sketch);
        }
        {
            var Q0;
            Q0=makeQuery(id+"F78.imprint","IMPRINT",FACE,{"disambiguationData":[TD([[makeQuery(id+"F78.imprint","IMPRINT",EDGE,{"derivedFrom":sQuery(id+"F78.wireOp",EDGE,"E37")}),1.0]])]});
            var Q1;
            {var subQ0=makeQuery(id+"F14.boolean.opBoolean","COPY",FACE,{"derivedFrom":makeQuery(id+"F14.opExtrude","SWEPT_FACE",FACE,{"disambiguationData":[OSD([sQuery(id+"F13.wireOp",EDGE,"E19.filletArc")])]})});var subQ1=sQuery(id+"F7.wireOp",EDGE,"E8");Q1=makeQuery(id+"F71.boolean.opBoolean","SPLIT",FACE,{"disambiguationData":[TD([subQ0])],"derivedFrom":makeQuery(id+"F70.boolean.opBoolean","SPLIT",FACE,{"disambiguationData":[TD([subQ0])],"derivedFrom":makeQuery(id+"F69.boolean.opBoolean","SPLIT",FACE,{"disambiguationData":[TD([subQ0])],"derivedFrom":makeQuery(id+"F68.boolean.opBoolean","SPLIT",FACE,{"disambiguationData":[TD([subQ0])],"derivedFrom":makeQuery(id+"F67.boolean.opBoolean","SPLIT",FACE,{"disambiguationData":[TD([subQ0])],"derivedFrom":makeQuery(id+"F66.boolean.opBoolean","SPLIT",FACE,{"disambiguationData":[TD([subQ0])],"derivedFrom":makeQuery(id+"F65.boolean.opBoolean","SPLIT",FACE,{"disambiguationData":[TD([subQ0])],"derivedFrom":makeQuery(id+"F64.boolean.opBoolean","SPLIT",FACE,{"disambiguationData":[TD([subQ0])],"derivedFrom":makeQuery(id+"F63.boolean.opBoolean","SPLIT",FACE,{"disambiguationData":[TD([subQ0])],"derivedFrom":makeQuery(id+"F62.boolean.opBoolean","SPLIT",FACE,{"disambiguationData":[TD([subQ0])],"derivedFrom":makeQuery(id+"F61.boolean.opBoolean","SPLIT",FACE,{"disambiguationData":[TD([subQ0])],"derivedFrom":makeQuery(id+"F60.boolean.opBoolean","SPLIT",FACE,{"disambiguationData":[TD([subQ0])],"derivedFrom":makeQuery(id+"F59.boolean.opBoolean","SPLIT",FACE,{"disambiguationData":[TD([subQ0])],"derivedFrom":makeQuery(id+"F58.boolean.opBoolean","SPLIT",FACE,{"disambiguationData":[TD([subQ0])],"derivedFrom":makeQuery(id+"F57.boolean.opBoolean","SPLIT",FACE,{"disambiguationData":[TD([subQ0])],"derivedFrom":makeQuery(id+"F56.boolean.opBoolean","SPLIT",FACE,{"disambiguationData":[TD([subQ0])],"derivedFrom":makeQuery(id+"F55.boolean.opBoolean","SPLIT",FACE,{"disambiguationData":[TD([subQ0])],"derivedFrom":makeQuery(id+"F54.boolean.opBoolean","SPLIT",FACE,{"disambiguationData":[TD([subQ0])],"derivedFrom":makeQuery(id+"F53.boolean.opBoolean","SPLIT",FACE,{"disambiguationData":[TD([subQ0])],"derivedFrom":makeQuery(id+"F52.boolean.opBoolean","SPLIT",FACE,{"disambiguationData":[TD([subQ0])],"derivedFrom":makeQuery(id+"F51.boolean.opBoolean","SPLIT",FACE,{"disambiguationData":[TD([subQ0])],"derivedFrom":makeQuery(id+"F50.boolean.opBoolean","SPLIT",FACE,{"disambiguationData":[TD([subQ0])],"derivedFrom":makeQuery(id+"F49.boolean.opBoolean","SPLIT",FACE,{"disambiguationData":[TD([subQ0])],"derivedFrom":makeQuery(id+"F48.boolean.opBoolean","SPLIT",FACE,{"disambiguationData":[TD([subQ0])],"derivedFrom":makeQuery(id+"F47.boolean.opBoolean","SPLIT",FACE,{"disambiguationData":[TD([subQ0])],"derivedFrom":makeQuery(id+"F46.boolean.opBoolean","SPLIT",FACE,{"disambiguationData":[TD([subQ0])],"derivedFrom":makeQuery(id+"F45.boolean.opBoolean","SPLIT",FACE,{"disambiguationData":[TD([subQ0])],"derivedFrom":makeQuery(id+"F44.boolean.opBoolean","SPLIT",FACE,{"disambiguationData":[TD([subQ0])],"derivedFrom":makeQuery(id+"F43.boolean.opBoolean","SPLIT",FACE,{"disambiguationData":[TD([subQ0])],"derivedFrom":makeQuery(id+"F42.boolean.opBoolean","SPLIT",FACE,{"disambiguationData":[TD([subQ0])],"derivedFrom":makeQuery(id+"F41.boolean.opBoolean","SPLIT",FACE,{"disambiguationData":[TD([subQ0])],"derivedFrom":makeQuery(id+"F40.boolean.opBoolean","SPLIT",FACE,{"disambiguationData":[TD([subQ0])],"derivedFrom":makeQuery(id+"F39.boolean.opBoolean","SPLIT",FACE,{"disambiguationData":[TD([subQ0])],"derivedFrom":makeQuery(id+"F38.boolean.opBoolean","SPLIT",FACE,{"disambiguationData":[TD([subQ0])],"derivedFrom":makeQuery(id+"F37.boolean.opBoolean","SPLIT",FACE,{"disambiguationData":[TD([subQ0])],"derivedFrom":makeQuery(id+"F36.boolean.opBoolean","SPLIT",FACE,{"disambiguationData":[TD([subQ0])],"derivedFrom":makeQuery(id+"F35.boolean.opBoolean","SPLIT",FACE,{"disambiguationData":[TD([subQ0])],"derivedFrom":makeQuery(id+"F34.boolean.opBoolean","SPLIT",FACE,{"disambiguationData":[TD([subQ0])],"derivedFrom":makeQuery(id+"F33.boolean.opBoolean","SPLIT",FACE,{"disambiguationData":[TD([subQ0])],"derivedFrom":makeQuery(id+"F32.boolean.opBoolean","SPLIT",FACE,{"disambiguationData":[TD([subQ0])],"derivedFrom":makeQuery(id+"F31.boolean.opBoolean","SPLIT",FACE,{"disambiguationData":[TD([subQ0])],"derivedFrom":makeQuery(id+"F30.boolean.opBoolean","SPLIT",FACE,{"disambiguationData":[TD([subQ0])],"derivedFrom":makeQuery(id+"F29.boolean.opBoolean","SPLIT",FACE,{"disambiguationData":[TD([subQ0])],"derivedFrom":makeQuery(id+"F28.boolean.opBoolean","SPLIT",FACE,{"disambiguationData":[TD([subQ0])],"derivedFrom":makeQuery(id+"F27.boolean.opBoolean","SPLIT",FACE,{"disambiguationData":[TD([subQ0])],"derivedFrom":makeQuery(id+"F26.boolean.opBoolean","SPLIT",FACE,{"disambiguationData":[TD([subQ0])],"derivedFrom":makeQuery(id+"F25.boolean.opBoolean","SPLIT",FACE,{"disambiguationData":[TD([subQ0])],"derivedFrom":makeQuery(id+"F24.boolean.opBoolean","SPLIT",FACE,{"disambiguationData":[TD([subQ0])],"derivedFrom":makeQuery(id+"F23.boolean.opBoolean","SPLIT",FACE,{"disambiguationData":[TD([subQ0])],"derivedFrom":makeQuery(id+"F22.boolean.opBoolean","SPLIT",FACE,{"disambiguationData":[TD([subQ0])],"derivedFrom":makeQuery(id+"F21.boolean.opBoolean","SPLIT",FACE,{"disambiguationData":[TD([subQ0])],"derivedFrom":makeQuery(id+"F20.boolean.opBoolean","SPLIT",FACE,{"disambiguationData":[TD([subQ0])],"derivedFrom":makeQuery(id+"F19.boolean.opBoolean","SPLIT",FACE,{"disambiguationData":[TD([subQ0])],"derivedFrom":makeQuery(id+"F18.boolean.opBoolean","SPLIT",FACE,{"disambiguationData":[TD([subQ0])],"derivedFrom":makeQuery(id+"F17.boolean.opBoolean","SPLIT",FACE,{"disambiguationData":[TD([subQ0])],"derivedFrom":makeQuery(id+"F16.boolean.opBoolean","SPLIT",FACE,{"disambiguationData":[TD([subQ0])],"derivedFrom":makeQuery(id+"F15.boolean.opBoolean","SPLIT",FACE,{"disambiguationData":[TD([subQ0])],"derivedFrom":makeQuery(id+"F8.opExtrude","SWEPT_FACE",FACE,{"disambiguationData":[OSD([subQ1])]})})})})})})})})})})})})})})})})})})})})})})})})})})})})})})})})})})})})})})})})})})})})})})})})})})})})})})})})})});}
            revolve(context, id + "F79", {"operationType" : NewBodyOperationType.REMOVE, "surfaceOperationType" : NewSurfaceOperationType.NEW, "entities" : qUnion([Q0]), "axis" : qUnion([Q1]), "revolveType" : RevolveType.FULL, "oppositeDirection" : true});
        }
    });
